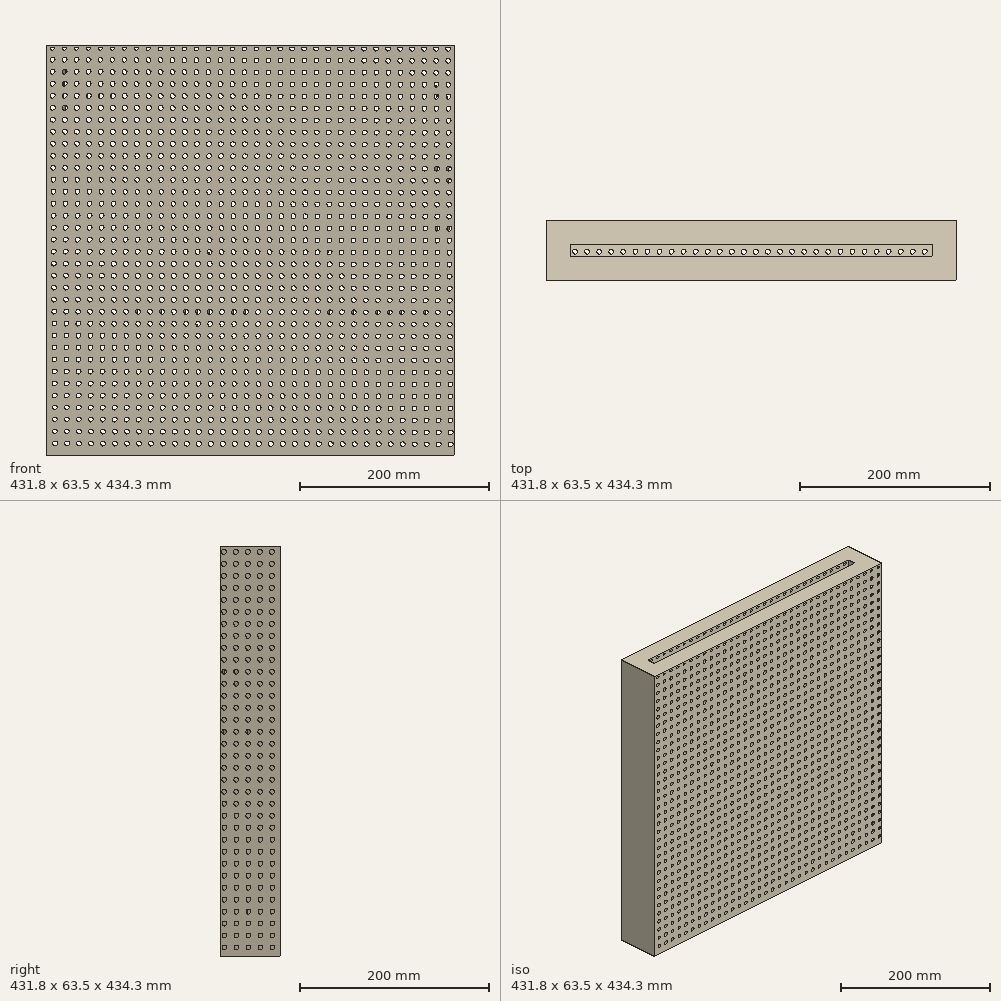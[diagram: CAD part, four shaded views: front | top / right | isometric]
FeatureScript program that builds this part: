
annotation { "Feature Type Name" : "Feature", "Feature Type Description" : "" }
export const myFeature = defineFeature(function(context is Context, id is Id, definition is map)
    precondition{}
    {
        {
            var Q0;
            Q0=qCreatedBy(makeId("Top.planeOp"),FACE);
            var sketch = newSketch(context, id + "F0", { "sketchPlane" : qUnion([Q0])});
            skLineSegment(sketch, "E0", {"start": v(-190.5, 6.35) * mm, "end": v(0, 6.35) * mm});
            skLineSegment(sketch, "E1", {"start": v(0, 6.35) * mm, "end": v(190.5, 6.35) * mm});
            skLineSegment(sketch, "E2", {"start": v(190.5, 6.35) * mm, "end": v(190.5, 0) * mm});
            skLineSegment(sketch, "E3", {"start": v(190.5, 0) * mm, "end": v(190.5, -6.35) * mm});
            skLineSegment(sketch, "E4", {"start": v(190.5, -6.35) * mm, "end": v(-190.5, -6.35) * mm});
            skLineSegment(sketch, "E5", {"start": v(-190.5, -6.35) * mm, "end": v(-190.5, 6.35) * mm});
            skLineSegment(sketch, "E6.0", {"start": v(-215.9, -31.75) * mm, "end": v(-215.9, 31.75) * mm});
            skLineSegment(sketch, "E6.1", {"start": v(0, 31.75) * mm, "end": v(215.9, 31.75) * mm});
            skLineSegment(sketch, "E6.2", {"start": v(215.9, 31.75) * mm, "end": v(215.9, -10.38) * mm});
            skLineSegment(sketch, "E6.3", {"start": v(-215.9, 31.75) * mm, "end": v(0, 31.75) * mm});
            skLineSegment(sketch, "E6.4", {"start": v(215.9, -10.38) * mm, "end": v(215.9, -31.75) * mm});
            skLineSegment(sketch, "E6.5", {"start": v(215.9, -31.75) * mm, "end": v(-215.9, -31.75) * mm});
            skSolve(sketch);
        }
        {
            var Q0;
            Q0 = qSketchRegion(id + "F0", true);
            extrude(context, id + "F1", {"entities" : qUnion([Q0]), "depth" : 431.8 * mm, "offsetDistance" : 25.4 * mm});
        }
        {
            var Q0;
            Q0=makeQuery(id+"F1.opExtrude","SWEPT_FACE",FACE,{"disambiguationData":[OSD([sQuery(id+"F0.wireOp",EDGE,"E6.1"),sQuery(id+"F0.wireOp",EDGE,"E6.3")])]});
            var sketch = newSketch(context, id + "F2", { "sketchPlane" : qUnion([Q0])});
            skCircle(sketch, "E7", {"center": v(209.68, 431.8) * mm, "radius": 2.54 * mm});
            skCircle(sketch, "E8.0.1.0", {"center": v(209.6, 419.1) * mm, "radius": 2.54 * mm});
            skCircle(sketch, "E8.0.2.0", {"center": v(209.51, 406.4) * mm, "radius": 2.54 * mm});
            skCircle(sketch, "E8.0.3.0", {"center": v(209.43, 393.7) * mm, "radius": 2.54 * mm});
            skCircle(sketch, "E8.0.4.0", {"center": v(209.34, 381) * mm, "radius": 2.54 * mm});
            skCircle(sketch, "E8.0.5.0", {"center": v(209.26, 368.3) * mm, "radius": 2.54 * mm});
            skCircle(sketch, "E8.0.6.0", {"center": v(209.17, 355.6) * mm, "radius": 2.54 * mm});
            skCircle(sketch, "E8.0.7.0", {"center": v(209.1, 342.9) * mm, "radius": 2.54 * mm});
            skCircle(sketch, "E8.0.8.0", {"center": v(209, 330.2) * mm, "radius": 2.54 * mm});
            skCircle(sketch, "E8.0.9.0", {"center": v(208.92, 317.5) * mm, "radius": 2.54 * mm});
            skCircle(sketch, "E8.0.10.0", {"center": v(208.84, 304.8) * mm, "radius": 2.54 * mm});
            skCircle(sketch, "E8.0.11.0", {"center": v(208.75, 292.1) * mm, "radius": 2.54 * mm});
            skCircle(sketch, "E8.0.12.0", {"center": v(208.67, 279.4) * mm, "radius": 2.54 * mm});
            skCircle(sketch, "E8.0.13.0", {"center": v(208.59, 266.7) * mm, "radius": 2.54 * mm});
            skCircle(sketch, "E8.0.14.0", {"center": v(208.5, 254) * mm, "radius": 2.54 * mm});
            skCircle(sketch, "E8.0.15.0", {"center": v(208.42, 241.3) * mm, "radius": 2.54 * mm});
            skCircle(sketch, "E8.0.16.0", {"center": v(208.33, 228.6) * mm, "radius": 2.54 * mm});
            skCircle(sketch, "E8.0.17.0", {"center": v(208.25, 215.9) * mm, "radius": 2.54 * mm});
            skCircle(sketch, "E8.0.18.0", {"center": v(208.17, 203.2) * mm, "radius": 2.54 * mm});
            skCircle(sketch, "E8.0.19.0", {"center": v(208.08, 190.5) * mm, "radius": 2.54 * mm});
            skCircle(sketch, "E8.0.20.0", {"center": v(208, 177.8) * mm, "radius": 2.54 * mm});
            skCircle(sketch, "E8.0.21.0", {"center": v(207.91, 165.1) * mm, "radius": 2.54 * mm});
            skCircle(sketch, "E8.0.22.0", {"center": v(207.83, 152.4) * mm, "radius": 2.54 * mm});
            skCircle(sketch, "E8.0.23.0", {"center": v(207.75, 139.7) * mm, "radius": 2.54 * mm});
            skCircle(sketch, "E8.0.24.0", {"center": v(207.66, 127) * mm, "radius": 2.54 * mm});
            skCircle(sketch, "E8.0.25.0", {"center": v(207.58, 114.3) * mm, "radius": 2.54 * mm});
            skCircle(sketch, "E8.0.26.0", {"center": v(207.5, 101.6) * mm, "radius": 2.54 * mm});
            skCircle(sketch, "E8.0.27.0", {"center": v(207.4, 88.9) * mm, "radius": 2.54 * mm});
            skCircle(sketch, "E8.0.28.0", {"center": v(207.33, 76.2) * mm, "radius": 2.54 * mm});
            skCircle(sketch, "E8.0.29.0", {"center": v(207.24, 63.5) * mm, "radius": 2.54 * mm});
            skCircle(sketch, "E8.0.30.0", {"center": v(207.16, 50.8) * mm, "radius": 2.54 * mm});
            skCircle(sketch, "E8.0.31.0", {"center": v(207.07, 38.1) * mm, "radius": 2.54 * mm});
            skCircle(sketch, "E8.0.32.0", {"center": v(206.99, 25.4) * mm, "radius": 2.54 * mm});
            skCircle(sketch, "E8.1.0.0", {"center": v(196.98, 431.77) * mm, "radius": 2.54 * mm});
            skCircle(sketch, "E8.1.1.0", {"center": v(196.9, 419.07) * mm, "radius": 2.54 * mm});
            skCircle(sketch, "E8.1.2.0", {"center": v(196.81, 406.37) * mm, "radius": 2.54 * mm});
            skCircle(sketch, "E8.1.3.0", {"center": v(196.73, 393.67) * mm, "radius": 2.54 * mm});
            skCircle(sketch, "E8.1.4.0", {"center": v(196.64, 380.97) * mm, "radius": 2.54 * mm});
            skCircle(sketch, "E8.1.5.0", {"center": v(196.56, 368.27) * mm, "radius": 2.54 * mm});
            skCircle(sketch, "E8.1.6.0", {"center": v(196.47, 355.57) * mm, "radius": 2.54 * mm});
            skCircle(sketch, "E8.1.7.0", {"center": v(196.4, 342.87) * mm, "radius": 2.54 * mm});
            skCircle(sketch, "E8.1.8.0", {"center": v(196.3, 330.17) * mm, "radius": 2.54 * mm});
            skCircle(sketch, "E8.1.9.0", {"center": v(196.22, 317.47) * mm, "radius": 2.54 * mm});
            skCircle(sketch, "E8.1.10.0", {"center": v(196.14, 304.77) * mm, "radius": 2.54 * mm});
            skCircle(sketch, "E8.1.11.0", {"center": v(196.05, 292.07) * mm, "radius": 2.54 * mm});
            skCircle(sketch, "E8.1.12.0", {"center": v(195.97, 279.37) * mm, "radius": 2.54 * mm});
            skCircle(sketch, "E8.1.13.0", {"center": v(195.89, 266.67) * mm, "radius": 2.54 * mm});
            skCircle(sketch, "E8.1.14.0", {"center": v(195.8, 253.97) * mm, "radius": 2.54 * mm});
            skCircle(sketch, "E8.1.15.0", {"center": v(195.72, 241.27) * mm, "radius": 2.54 * mm});
            skCircle(sketch, "E8.1.16.0", {"center": v(195.63, 228.57) * mm, "radius": 2.54 * mm});
            skCircle(sketch, "E8.1.17.0", {"center": v(195.55, 215.87) * mm, "radius": 2.54 * mm});
            skCircle(sketch, "E8.1.18.0", {"center": v(195.47, 203.17) * mm, "radius": 2.54 * mm});
            skCircle(sketch, "E8.1.19.0", {"center": v(195.38, 190.47) * mm, "radius": 2.54 * mm});
            skCircle(sketch, "E8.1.20.0", {"center": v(195.3, 177.77) * mm, "radius": 2.54 * mm});
            skCircle(sketch, "E8.1.21.0", {"center": v(195.21, 165.07) * mm, "radius": 2.54 * mm});
            skCircle(sketch, "E8.1.22.0", {"center": v(195.13, 152.37) * mm, "radius": 2.54 * mm});
            skCircle(sketch, "E8.1.23.0", {"center": v(195.05, 139.67) * mm, "radius": 2.54 * mm});
            skCircle(sketch, "E8.1.24.0", {"center": v(194.96, 126.98) * mm, "radius": 2.54 * mm});
            skCircle(sketch, "E8.1.25.0", {"center": v(194.88, 114.28) * mm, "radius": 2.54 * mm});
            skCircle(sketch, "E8.1.26.0", {"center": v(194.8, 101.58) * mm, "radius": 2.54 * mm});
            skCircle(sketch, "E8.1.27.0", {"center": v(194.7, 88.88) * mm, "radius": 2.54 * mm});
            skCircle(sketch, "E8.1.28.0", {"center": v(194.63, 76.18) * mm, "radius": 2.54 * mm});
            skCircle(sketch, "E8.1.29.0", {"center": v(194.54, 63.48) * mm, "radius": 2.54 * mm});
            skCircle(sketch, "E8.1.30.0", {"center": v(194.46, 50.78) * mm, "radius": 2.54 * mm});
            skCircle(sketch, "E8.1.31.0", {"center": v(194.37, 38.08) * mm, "radius": 2.54 * mm});
            skCircle(sketch, "E8.1.32.0", {"center": v(194.29, 25.38) * mm, "radius": 2.54 * mm});
            skCircle(sketch, "E8.2.0.0", {"center": v(184.28, 431.74) * mm, "radius": 2.54 * mm});
            skCircle(sketch, "E8.2.1.0", {"center": v(184.2, 419.04) * mm, "radius": 2.54 * mm});
            skCircle(sketch, "E8.2.2.0", {"center": v(184.11, 406.34) * mm, "radius": 2.54 * mm});
            skCircle(sketch, "E8.2.3.0", {"center": v(184.03, 393.64) * mm, "radius": 2.54 * mm});
            skCircle(sketch, "E8.2.4.0", {"center": v(183.94, 380.94) * mm, "radius": 2.54 * mm});
            skCircle(sketch, "E8.2.5.0", {"center": v(183.86, 368.24) * mm, "radius": 2.54 * mm});
            skCircle(sketch, "E8.2.6.0", {"center": v(183.77, 355.54) * mm, "radius": 2.54 * mm});
            skCircle(sketch, "E8.2.7.0", {"center": v(183.7, 342.84) * mm, "radius": 2.54 * mm});
            skCircle(sketch, "E8.2.8.0", {"center": v(183.6, 330.14) * mm, "radius": 2.54 * mm});
            skCircle(sketch, "E8.2.9.0", {"center": v(183.52, 317.44) * mm, "radius": 2.54 * mm});
            skCircle(sketch, "E8.2.10.0", {"center": v(183.44, 304.74) * mm, "radius": 2.54 * mm});
            skCircle(sketch, "E8.2.11.0", {"center": v(183.35, 292.04) * mm, "radius": 2.54 * mm});
            skCircle(sketch, "E8.2.12.0", {"center": v(183.27, 279.34) * mm, "radius": 2.54 * mm});
            skCircle(sketch, "E8.2.13.0", {"center": v(183.19, 266.64) * mm, "radius": 2.54 * mm});
            skCircle(sketch, "E8.2.14.0", {"center": v(183.1, 253.94) * mm, "radius": 2.54 * mm});
            skCircle(sketch, "E8.2.15.0", {"center": v(183.02, 241.24) * mm, "radius": 2.54 * mm});
            skCircle(sketch, "E8.2.16.0", {"center": v(182.93, 228.54) * mm, "radius": 2.54 * mm});
            skCircle(sketch, "E8.2.17.0", {"center": v(182.85, 215.84) * mm, "radius": 2.54 * mm});
            skCircle(sketch, "E8.2.18.0", {"center": v(182.77, 203.14) * mm, "radius": 2.54 * mm});
            skCircle(sketch, "E8.2.19.0", {"center": v(182.68, 190.44) * mm, "radius": 2.54 * mm});
            skCircle(sketch, "E8.2.20.0", {"center": v(182.6, 177.74) * mm, "radius": 2.54 * mm});
            skCircle(sketch, "E8.2.21.0", {"center": v(182.51, 165.04) * mm, "radius": 2.54 * mm});
            skCircle(sketch, "E8.2.22.0", {"center": v(182.43, 152.34) * mm, "radius": 2.54 * mm});
            skCircle(sketch, "E8.2.23.0", {"center": v(182.35, 139.64) * mm, "radius": 2.54 * mm});
            skCircle(sketch, "E8.2.24.0", {"center": v(182.26, 126.94) * mm, "radius": 2.54 * mm});
            skCircle(sketch, "E8.2.25.0", {"center": v(182.18, 114.24) * mm, "radius": 2.54 * mm});
            skCircle(sketch, "E8.2.26.0", {"center": v(182.1, 101.54) * mm, "radius": 2.54 * mm});
            skCircle(sketch, "E8.2.27.0", {"center": v(182, 88.84) * mm, "radius": 2.54 * mm});
            skCircle(sketch, "E8.2.28.0", {"center": v(181.93, 76.14) * mm, "radius": 2.54 * mm});
            skCircle(sketch, "E8.2.29.0", {"center": v(181.84, 63.45) * mm, "radius": 2.54 * mm});
            skCircle(sketch, "E8.2.30.0", {"center": v(181.76, 50.75) * mm, "radius": 2.54 * mm});
            skCircle(sketch, "E8.2.31.0", {"center": v(181.67, 38.05) * mm, "radius": 2.54 * mm});
            skCircle(sketch, "E8.2.32.0", {"center": v(181.59, 25.35) * mm, "radius": 2.54 * mm});
            skCircle(sketch, "E8.3.0.0", {"center": v(171.58, 431.7) * mm, "radius": 2.54 * mm});
            skCircle(sketch, "E8.3.1.0", {"center": v(171.5, 419) * mm, "radius": 2.54 * mm});
            skCircle(sketch, "E8.3.2.0", {"center": v(171.41, 406.3) * mm, "radius": 2.54 * mm});
            skCircle(sketch, "E8.3.3.0", {"center": v(171.33, 393.6) * mm, "radius": 2.54 * mm});
            skCircle(sketch, "E8.3.4.0", {"center": v(171.24, 380.9) * mm, "radius": 2.54 * mm});
            skCircle(sketch, "E8.3.5.0", {"center": v(171.16, 368.2) * mm, "radius": 2.54 * mm});
            skCircle(sketch, "E8.3.6.0", {"center": v(171.07, 355.5) * mm, "radius": 2.54 * mm});
            skCircle(sketch, "E8.3.7.0", {"center": v(171, 342.8) * mm, "radius": 2.54 * mm});
            skCircle(sketch, "E8.3.8.0", {"center": v(170.9, 330.1) * mm, "radius": 2.54 * mm});
            skCircle(sketch, "E8.3.9.0", {"center": v(170.82, 317.4) * mm, "radius": 2.54 * mm});
            skCircle(sketch, "E8.3.10.0", {"center": v(170.74, 304.7) * mm, "radius": 2.54 * mm});
            skCircle(sketch, "E8.3.11.0", {"center": v(170.65, 292) * mm, "radius": 2.54 * mm});
            skCircle(sketch, "E8.3.12.0", {"center": v(170.57, 279.3) * mm, "radius": 2.54 * mm});
            skCircle(sketch, "E8.3.13.0", {"center": v(170.49, 266.6) * mm, "radius": 2.54 * mm});
            skCircle(sketch, "E8.3.14.0", {"center": v(170.4, 253.9) * mm, "radius": 2.54 * mm});
            skCircle(sketch, "E8.3.15.0", {"center": v(170.32, 241.2) * mm, "radius": 2.54 * mm});
            skCircle(sketch, "E8.3.16.0", {"center": v(170.23, 228.51) * mm, "radius": 2.54 * mm});
            skCircle(sketch, "E8.3.17.0", {"center": v(170.15, 215.81) * mm, "radius": 2.54 * mm});
            skCircle(sketch, "E8.3.18.0", {"center": v(170.07, 203.11) * mm, "radius": 2.54 * mm});
            skCircle(sketch, "E8.3.19.0", {"center": v(169.98, 190.41) * mm, "radius": 2.54 * mm});
            skCircle(sketch, "E8.3.20.0", {"center": v(169.9, 177.71) * mm, "radius": 2.54 * mm});
            skCircle(sketch, "E8.3.21.0", {"center": v(169.81, 165.01) * mm, "radius": 2.54 * mm});
            skCircle(sketch, "E8.3.22.0", {"center": v(169.73, 152.31) * mm, "radius": 2.54 * mm});
            skCircle(sketch, "E8.3.23.0", {"center": v(169.65, 139.61) * mm, "radius": 2.54 * mm});
            skCircle(sketch, "E8.3.24.0", {"center": v(169.56, 126.91) * mm, "radius": 2.54 * mm});
            skCircle(sketch, "E8.3.25.0", {"center": v(169.48, 114.21) * mm, "radius": 2.54 * mm});
            skCircle(sketch, "E8.3.26.0", {"center": v(169.4, 101.51) * mm, "radius": 2.54 * mm});
            skCircle(sketch, "E8.3.27.0", {"center": v(169.3, 88.81) * mm, "radius": 2.54 * mm});
            skCircle(sketch, "E8.3.28.0", {"center": v(169.23, 76.11) * mm, "radius": 2.54 * mm});
            skCircle(sketch, "E8.3.29.0", {"center": v(169.14, 63.41) * mm, "radius": 2.54 * mm});
            skCircle(sketch, "E8.3.30.0", {"center": v(169.06, 50.71) * mm, "radius": 2.54 * mm});
            skCircle(sketch, "E8.3.31.0", {"center": v(168.97, 38.01) * mm, "radius": 2.54 * mm});
            skCircle(sketch, "E8.3.32.0", {"center": v(168.89, 25.31) * mm, "radius": 2.54 * mm});
            skCircle(sketch, "E8.4.0.0", {"center": v(158.88, 431.67) * mm, "radius": 2.54 * mm});
            skCircle(sketch, "E8.4.1.0", {"center": v(158.8, 418.97) * mm, "radius": 2.54 * mm});
            skCircle(sketch, "E8.4.2.0", {"center": v(158.71, 406.27) * mm, "radius": 2.54 * mm});
            skCircle(sketch, "E8.4.3.0", {"center": v(158.63, 393.58) * mm, "radius": 2.54 * mm});
            skCircle(sketch, "E8.4.4.0", {"center": v(158.54, 380.88) * mm, "radius": 2.54 * mm});
            skCircle(sketch, "E8.4.5.0", {"center": v(158.46, 368.18) * mm, "radius": 2.54 * mm});
            skCircle(sketch, "E8.4.6.0", {"center": v(158.37, 355.48) * mm, "radius": 2.54 * mm});
            skCircle(sketch, "E8.4.7.0", {"center": v(158.3, 342.78) * mm, "radius": 2.54 * mm});
            skCircle(sketch, "E8.4.8.0", {"center": v(158.2, 330.08) * mm, "radius": 2.54 * mm});
            skCircle(sketch, "E8.4.9.0", {"center": v(158.12, 317.38) * mm, "radius": 2.54 * mm});
            skCircle(sketch, "E8.4.10.0", {"center": v(158.04, 304.68) * mm, "radius": 2.54 * mm});
            skCircle(sketch, "E8.4.11.0", {"center": v(157.95, 291.98) * mm, "radius": 2.54 * mm});
            skCircle(sketch, "E8.4.12.0", {"center": v(157.87, 279.28) * mm, "radius": 2.54 * mm});
            skCircle(sketch, "E8.4.13.0", {"center": v(157.79, 266.58) * mm, "radius": 2.54 * mm});
            skCircle(sketch, "E8.4.14.0", {"center": v(157.7, 253.88) * mm, "radius": 2.54 * mm});
            skCircle(sketch, "E8.4.15.0", {"center": v(157.62, 241.18) * mm, "radius": 2.54 * mm});
            skCircle(sketch, "E8.4.16.0", {"center": v(157.53, 228.48) * mm, "radius": 2.54 * mm});
            skCircle(sketch, "E8.4.17.0", {"center": v(157.45, 215.78) * mm, "radius": 2.54 * mm});
            skCircle(sketch, "E8.4.18.0", {"center": v(157.37, 203.08) * mm, "radius": 2.54 * mm});
            skCircle(sketch, "E8.4.19.0", {"center": v(157.28, 190.38) * mm, "radius": 2.54 * mm});
            skCircle(sketch, "E8.4.20.0", {"center": v(157.2, 177.68) * mm, "radius": 2.54 * mm});
            skCircle(sketch, "E8.4.21.0", {"center": v(157.11, 164.98) * mm, "radius": 2.54 * mm});
            skCircle(sketch, "E8.4.22.0", {"center": v(157.03, 152.28) * mm, "radius": 2.54 * mm});
            skCircle(sketch, "E8.4.23.0", {"center": v(156.95, 139.58) * mm, "radius": 2.54 * mm});
            skCircle(sketch, "E8.4.24.0", {"center": v(156.86, 126.88) * mm, "radius": 2.54 * mm});
            skCircle(sketch, "E8.4.25.0", {"center": v(156.78, 114.18) * mm, "radius": 2.54 * mm});
            skCircle(sketch, "E8.4.26.0", {"center": v(156.7, 101.48) * mm, "radius": 2.54 * mm});
            skCircle(sketch, "E8.4.27.0", {"center": v(156.6, 88.78) * mm, "radius": 2.54 * mm});
            skCircle(sketch, "E8.4.28.0", {"center": v(156.53, 76.08) * mm, "radius": 2.54 * mm});
            skCircle(sketch, "E8.4.29.0", {"center": v(156.44, 63.38) * mm, "radius": 2.54 * mm});
            skCircle(sketch, "E8.4.30.0", {"center": v(156.36, 50.68) * mm, "radius": 2.54 * mm});
            skCircle(sketch, "E8.4.31.0", {"center": v(156.27, 37.98) * mm, "radius": 2.54 * mm});
            skCircle(sketch, "E8.4.32.0", {"center": v(156.19, 25.28) * mm, "radius": 2.54 * mm});
            skCircle(sketch, "E8.5.0.0", {"center": v(146.18, 431.64) * mm, "radius": 2.54 * mm});
            skCircle(sketch, "E8.5.1.0", {"center": v(146.1, 418.94) * mm, "radius": 2.54 * mm});
            skCircle(sketch, "E8.5.2.0", {"center": v(146.01, 406.24) * mm, "radius": 2.54 * mm});
            skCircle(sketch, "E8.5.3.0", {"center": v(145.93, 393.54) * mm, "radius": 2.54 * mm});
            skCircle(sketch, "E8.5.4.0", {"center": v(145.84, 380.84) * mm, "radius": 2.54 * mm});
            skCircle(sketch, "E8.5.5.0", {"center": v(145.76, 368.14) * mm, "radius": 2.54 * mm});
            skCircle(sketch, "E8.5.6.0", {"center": v(145.67, 355.44) * mm, "radius": 2.54 * mm});
            skCircle(sketch, "E8.5.7.0", {"center": v(145.6, 342.74) * mm, "radius": 2.54 * mm});
            skCircle(sketch, "E8.5.8.0", {"center": v(145.5, 330.05) * mm, "radius": 2.54 * mm});
            skCircle(sketch, "E8.5.9.0", {"center": v(145.42, 317.35) * mm, "radius": 2.54 * mm});
            skCircle(sketch, "E8.5.10.0", {"center": v(145.34, 304.65) * mm, "radius": 2.54 * mm});
            skCircle(sketch, "E8.5.11.0", {"center": v(145.25, 291.95) * mm, "radius": 2.54 * mm});
            skCircle(sketch, "E8.5.12.0", {"center": v(145.17, 279.25) * mm, "radius": 2.54 * mm});
            skCircle(sketch, "E8.5.13.0", {"center": v(145.09, 266.55) * mm, "radius": 2.54 * mm});
            skCircle(sketch, "E8.5.14.0", {"center": v(145, 253.85) * mm, "radius": 2.54 * mm});
            skCircle(sketch, "E8.5.15.0", {"center": v(144.92, 241.15) * mm, "radius": 2.54 * mm});
            skCircle(sketch, "E8.5.16.0", {"center": v(144.83, 228.45) * mm, "radius": 2.54 * mm});
            skCircle(sketch, "E8.5.17.0", {"center": v(144.75, 215.75) * mm, "radius": 2.54 * mm});
            skCircle(sketch, "E8.5.18.0", {"center": v(144.67, 203.05) * mm, "radius": 2.54 * mm});
            skCircle(sketch, "E8.5.19.0", {"center": v(144.58, 190.35) * mm, "radius": 2.54 * mm});
            skCircle(sketch, "E8.5.20.0", {"center": v(144.5, 177.65) * mm, "radius": 2.54 * mm});
            skCircle(sketch, "E8.5.21.0", {"center": v(144.41, 164.95) * mm, "radius": 2.54 * mm});
            skCircle(sketch, "E8.5.22.0", {"center": v(144.33, 152.25) * mm, "radius": 2.54 * mm});
            skCircle(sketch, "E8.5.23.0", {"center": v(144.25, 139.55) * mm, "radius": 2.54 * mm});
            skCircle(sketch, "E8.5.24.0", {"center": v(144.16, 126.85) * mm, "radius": 2.54 * mm});
            skCircle(sketch, "E8.5.25.0", {"center": v(144.08, 114.15) * mm, "radius": 2.54 * mm});
            skCircle(sketch, "E8.5.26.0", {"center": v(144, 101.45) * mm, "radius": 2.54 * mm});
            skCircle(sketch, "E8.5.27.0", {"center": v(143.9, 88.75) * mm, "radius": 2.54 * mm});
            skCircle(sketch, "E8.5.28.0", {"center": v(143.83, 76.05) * mm, "radius": 2.54 * mm});
            skCircle(sketch, "E8.5.29.0", {"center": v(143.74, 63.35) * mm, "radius": 2.54 * mm});
            skCircle(sketch, "E8.5.30.0", {"center": v(143.66, 50.65) * mm, "radius": 2.54 * mm});
            skCircle(sketch, "E8.5.31.0", {"center": v(143.57, 37.95) * mm, "radius": 2.54 * mm});
            skCircle(sketch, "E8.5.32.0", {"center": v(143.49, 25.25) * mm, "radius": 2.54 * mm});
            skCircle(sketch, "E8.6.0.0", {"center": v(133.48, 431.61) * mm, "radius": 2.54 * mm});
            skCircle(sketch, "E8.6.1.0", {"center": v(133.4, 418.91) * mm, "radius": 2.54 * mm});
            skCircle(sketch, "E8.6.2.0", {"center": v(133.31, 406.21) * mm, "radius": 2.54 * mm});
            skCircle(sketch, "E8.6.3.0", {"center": v(133.23, 393.51) * mm, "radius": 2.54 * mm});
            skCircle(sketch, "E8.6.4.0", {"center": v(133.14, 380.81) * mm, "radius": 2.54 * mm});
            skCircle(sketch, "E8.6.5.0", {"center": v(133.06, 368.11) * mm, "radius": 2.54 * mm});
            skCircle(sketch, "E8.6.6.0", {"center": v(132.97, 355.41) * mm, "radius": 2.54 * mm});
            skCircle(sketch, "E8.6.7.0", {"center": v(132.9, 342.71) * mm, "radius": 2.54 * mm});
            skCircle(sketch, "E8.6.8.0", {"center": v(132.8, 330.01) * mm, "radius": 2.54 * mm});
            skCircle(sketch, "E8.6.9.0", {"center": v(132.72, 317.31) * mm, "radius": 2.54 * mm});
            skCircle(sketch, "E8.6.10.0", {"center": v(132.64, 304.61) * mm, "radius": 2.54 * mm});
            skCircle(sketch, "E8.6.11.0", {"center": v(132.55, 291.91) * mm, "radius": 2.54 * mm});
            skCircle(sketch, "E8.6.12.0", {"center": v(132.47, 279.21) * mm, "radius": 2.54 * mm});
            skCircle(sketch, "E8.6.13.0", {"center": v(132.39, 266.52) * mm, "radius": 2.54 * mm});
            skCircle(sketch, "E8.6.14.0", {"center": v(132.3, 253.82) * mm, "radius": 2.54 * mm});
            skCircle(sketch, "E8.6.15.0", {"center": v(132.22, 241.12) * mm, "radius": 2.54 * mm});
            skCircle(sketch, "E8.6.16.0", {"center": v(132.13, 228.42) * mm, "radius": 2.54 * mm});
            skCircle(sketch, "E8.6.17.0", {"center": v(132.05, 215.72) * mm, "radius": 2.54 * mm});
            skCircle(sketch, "E8.6.18.0", {"center": v(131.97, 203.02) * mm, "radius": 2.54 * mm});
            skCircle(sketch, "E8.6.19.0", {"center": v(131.88, 190.32) * mm, "radius": 2.54 * mm});
            skCircle(sketch, "E8.6.20.0", {"center": v(131.8, 177.62) * mm, "radius": 2.54 * mm});
            skCircle(sketch, "E8.6.21.0", {"center": v(131.71, 164.92) * mm, "radius": 2.54 * mm});
            skCircle(sketch, "E8.6.22.0", {"center": v(131.63, 152.22) * mm, "radius": 2.54 * mm});
            skCircle(sketch, "E8.6.23.0", {"center": v(131.55, 139.52) * mm, "radius": 2.54 * mm});
            skCircle(sketch, "E8.6.24.0", {"center": v(131.46, 126.82) * mm, "radius": 2.54 * mm});
            skCircle(sketch, "E8.6.25.0", {"center": v(131.38, 114.12) * mm, "radius": 2.54 * mm});
            skCircle(sketch, "E8.6.26.0", {"center": v(131.3, 101.42) * mm, "radius": 2.54 * mm});
            skCircle(sketch, "E8.6.27.0", {"center": v(131.2, 88.72) * mm, "radius": 2.54 * mm});
            skCircle(sketch, "E8.6.28.0", {"center": v(131.13, 76.02) * mm, "radius": 2.54 * mm});
            skCircle(sketch, "E8.6.29.0", {"center": v(131.04, 63.32) * mm, "radius": 2.54 * mm});
            skCircle(sketch, "E8.6.30.0", {"center": v(130.96, 50.62) * mm, "radius": 2.54 * mm});
            skCircle(sketch, "E8.6.31.0", {"center": v(130.87, 37.92) * mm, "radius": 2.54 * mm});
            skCircle(sketch, "E8.6.32.0", {"center": v(130.79, 25.22) * mm, "radius": 2.54 * mm});
            skCircle(sketch, "E8.7.0.0", {"center": v(120.78, 431.58) * mm, "radius": 2.54 * mm});
            skCircle(sketch, "E8.7.1.0", {"center": v(120.7, 418.88) * mm, "radius": 2.54 * mm});
            skCircle(sketch, "E8.7.2.0", {"center": v(120.61, 406.18) * mm, "radius": 2.54 * mm});
            skCircle(sketch, "E8.7.3.0", {"center": v(120.53, 393.48) * mm, "radius": 2.54 * mm});
            skCircle(sketch, "E8.7.4.0", {"center": v(120.44, 380.78) * mm, "radius": 2.54 * mm});
            skCircle(sketch, "E8.7.5.0", {"center": v(120.36, 368.08) * mm, "radius": 2.54 * mm});
            skCircle(sketch, "E8.7.6.0", {"center": v(120.27, 355.38) * mm, "radius": 2.54 * mm});
            skCircle(sketch, "E8.7.7.0", {"center": v(120.2, 342.68) * mm, "radius": 2.54 * mm});
            skCircle(sketch, "E8.7.8.0", {"center": v(120.1, 329.98) * mm, "radius": 2.54 * mm});
            skCircle(sketch, "E8.7.9.0", {"center": v(120.02, 317.28) * mm, "radius": 2.54 * mm});
            skCircle(sketch, "E8.7.10.0", {"center": v(119.94, 304.58) * mm, "radius": 2.54 * mm});
            skCircle(sketch, "E8.7.11.0", {"center": v(119.85, 291.88) * mm, "radius": 2.54 * mm});
            skCircle(sketch, "E8.7.12.0", {"center": v(119.77, 279.18) * mm, "radius": 2.54 * mm});
            skCircle(sketch, "E8.7.13.0", {"center": v(119.69, 266.48) * mm, "radius": 2.54 * mm});
            skCircle(sketch, "E8.7.14.0", {"center": v(119.6, 253.78) * mm, "radius": 2.54 * mm});
            skCircle(sketch, "E8.7.15.0", {"center": v(119.52, 241.08) * mm, "radius": 2.54 * mm});
            skCircle(sketch, "E8.7.16.0", {"center": v(119.43, 228.38) * mm, "radius": 2.54 * mm});
            skCircle(sketch, "E8.7.17.0", {"center": v(119.35, 215.68) * mm, "radius": 2.54 * mm});
            skCircle(sketch, "E8.7.18.0", {"center": v(119.27, 202.99) * mm, "radius": 2.54 * mm});
            skCircle(sketch, "E8.7.19.0", {"center": v(119.18, 190.29) * mm, "radius": 2.54 * mm});
            skCircle(sketch, "E8.7.20.0", {"center": v(119.1, 177.59) * mm, "radius": 2.54 * mm});
            skCircle(sketch, "E8.7.21.0", {"center": v(119.01, 164.89) * mm, "radius": 2.54 * mm});
            skCircle(sketch, "E8.7.22.0", {"center": v(118.93, 152.19) * mm, "radius": 2.54 * mm});
            skCircle(sketch, "E8.7.23.0", {"center": v(118.85, 139.49) * mm, "radius": 2.54 * mm});
            skCircle(sketch, "E8.7.24.0", {"center": v(118.76, 126.79) * mm, "radius": 2.54 * mm});
            skCircle(sketch, "E8.7.25.0", {"center": v(118.68, 114.09) * mm, "radius": 2.54 * mm});
            skCircle(sketch, "E8.7.26.0", {"center": v(118.6, 101.39) * mm, "radius": 2.54 * mm});
            skCircle(sketch, "E8.7.27.0", {"center": v(118.5, 88.69) * mm, "radius": 2.54 * mm});
            skCircle(sketch, "E8.7.28.0", {"center": v(118.43, 75.99) * mm, "radius": 2.54 * mm});
            skCircle(sketch, "E8.7.29.0", {"center": v(118.34, 63.29) * mm, "radius": 2.54 * mm});
            skCircle(sketch, "E8.7.30.0", {"center": v(118.26, 50.59) * mm, "radius": 2.54 * mm});
            skCircle(sketch, "E8.7.31.0", {"center": v(118.17, 37.89) * mm, "radius": 2.54 * mm});
            skCircle(sketch, "E8.7.32.0", {"center": v(118.09, 25.19) * mm, "radius": 2.54 * mm});
            skCircle(sketch, "E8.8.0.0", {"center": v(108.08, 431.55) * mm, "radius": 2.54 * mm});
            skCircle(sketch, "E8.8.1.0", {"center": v(108, 418.85) * mm, "radius": 2.54 * mm});
            skCircle(sketch, "E8.8.2.0", {"center": v(107.91, 406.15) * mm, "radius": 2.54 * mm});
            skCircle(sketch, "E8.8.3.0", {"center": v(107.83, 393.45) * mm, "radius": 2.54 * mm});
            skCircle(sketch, "E8.8.4.0", {"center": v(107.74, 380.75) * mm, "radius": 2.54 * mm});
            skCircle(sketch, "E8.8.5.0", {"center": v(107.66, 368.05) * mm, "radius": 2.54 * mm});
            skCircle(sketch, "E8.8.6.0", {"center": v(107.57, 355.35) * mm, "radius": 2.54 * mm});
            skCircle(sketch, "E8.8.7.0", {"center": v(107.5, 342.65) * mm, "radius": 2.54 * mm});
            skCircle(sketch, "E8.8.8.0", {"center": v(107.4, 329.95) * mm, "radius": 2.54 * mm});
            skCircle(sketch, "E8.8.9.0", {"center": v(107.32, 317.25) * mm, "radius": 2.54 * mm});
            skCircle(sketch, "E8.8.10.0", {"center": v(107.24, 304.55) * mm, "radius": 2.54 * mm});
            skCircle(sketch, "E8.8.11.0", {"center": v(107.15, 291.85) * mm, "radius": 2.54 * mm});
            skCircle(sketch, "E8.8.12.0", {"center": v(107.07, 279.15) * mm, "radius": 2.54 * mm});
            skCircle(sketch, "E8.8.13.0", {"center": v(106.99, 266.45) * mm, "radius": 2.54 * mm});
            skCircle(sketch, "E8.8.14.0", {"center": v(106.9, 253.75) * mm, "radius": 2.54 * mm});
            skCircle(sketch, "E8.8.15.0", {"center": v(106.82, 241.05) * mm, "radius": 2.54 * mm});
            skCircle(sketch, "E8.8.16.0", {"center": v(106.73, 228.35) * mm, "radius": 2.54 * mm});
            skCircle(sketch, "E8.8.17.0", {"center": v(106.65, 215.65) * mm, "radius": 2.54 * mm});
            skCircle(sketch, "E8.8.18.0", {"center": v(106.57, 202.95) * mm, "radius": 2.54 * mm});
            skCircle(sketch, "E8.8.19.0", {"center": v(106.48, 190.25) * mm, "radius": 2.54 * mm});
            skCircle(sketch, "E8.8.20.0", {"center": v(106.4, 177.55) * mm, "radius": 2.54 * mm});
            skCircle(sketch, "E8.8.21.0", {"center": v(106.31, 164.85) * mm, "radius": 2.54 * mm});
            skCircle(sketch, "E8.8.22.0", {"center": v(106.23, 152.15) * mm, "radius": 2.54 * mm});
            skCircle(sketch, "E8.8.23.0", {"center": v(106.15, 139.46) * mm, "radius": 2.54 * mm});
            skCircle(sketch, "E8.8.24.0", {"center": v(106.06, 126.76) * mm, "radius": 2.54 * mm});
            skCircle(sketch, "E8.8.25.0", {"center": v(105.98, 114.06) * mm, "radius": 2.54 * mm});
            skCircle(sketch, "E8.8.26.0", {"center": v(105.9, 101.36) * mm, "radius": 2.54 * mm});
            skCircle(sketch, "E8.8.27.0", {"center": v(105.8, 88.66) * mm, "radius": 2.54 * mm});
            skCircle(sketch, "E8.8.28.0", {"center": v(105.73, 75.96) * mm, "radius": 2.54 * mm});
            skCircle(sketch, "E8.8.29.0", {"center": v(105.64, 63.26) * mm, "radius": 2.54 * mm});
            skCircle(sketch, "E8.8.30.0", {"center": v(105.56, 50.56) * mm, "radius": 2.54 * mm});
            skCircle(sketch, "E8.8.31.0", {"center": v(105.47, 37.86) * mm, "radius": 2.54 * mm});
            skCircle(sketch, "E8.8.32.0", {"center": v(105.39, 25.16) * mm, "radius": 2.54 * mm});
            skCircle(sketch, "E8.9.0.0", {"center": v(95.38, 431.52) * mm, "radius": 2.54 * mm});
            skCircle(sketch, "E8.9.1.0", {"center": v(95.3, 418.82) * mm, "radius": 2.54 * mm});
            skCircle(sketch, "E8.9.2.0", {"center": v(95.21, 406.12) * mm, "radius": 2.54 * mm});
            skCircle(sketch, "E8.9.3.0", {"center": v(95.13, 393.42) * mm, "radius": 2.54 * mm});
            skCircle(sketch, "E8.9.4.0", {"center": v(95.04, 380.72) * mm, "radius": 2.54 * mm});
            skCircle(sketch, "E8.9.5.0", {"center": v(94.96, 368.02) * mm, "radius": 2.54 * mm});
            skCircle(sketch, "E8.9.6.0", {"center": v(94.87, 355.32) * mm, "radius": 2.54 * mm});
            skCircle(sketch, "E8.9.7.0", {"center": v(94.8, 342.62) * mm, "radius": 2.54 * mm});
            skCircle(sketch, "E8.9.8.0", {"center": v(94.7, 329.92) * mm, "radius": 2.54 * mm});
            skCircle(sketch, "E8.9.9.0", {"center": v(94.62, 317.22) * mm, "radius": 2.54 * mm});
            skCircle(sketch, "E8.9.10.0", {"center": v(94.54, 304.52) * mm, "radius": 2.54 * mm});
            skCircle(sketch, "E8.9.11.0", {"center": v(94.45, 291.82) * mm, "radius": 2.54 * mm});
            skCircle(sketch, "E8.9.12.0", {"center": v(94.37, 279.12) * mm, "radius": 2.54 * mm});
            skCircle(sketch, "E8.9.13.0", {"center": v(94.29, 266.42) * mm, "radius": 2.54 * mm});
            skCircle(sketch, "E8.9.14.0", {"center": v(94.2, 253.72) * mm, "radius": 2.54 * mm});
            skCircle(sketch, "E8.9.15.0", {"center": v(94.12, 241.02) * mm, "radius": 2.54 * mm});
            skCircle(sketch, "E8.9.16.0", {"center": v(94.03, 228.32) * mm, "radius": 2.54 * mm});
            skCircle(sketch, "E8.9.17.0", {"center": v(93.95, 215.62) * mm, "radius": 2.54 * mm});
            skCircle(sketch, "E8.9.18.0", {"center": v(93.87, 202.92) * mm, "radius": 2.54 * mm});
            skCircle(sketch, "E8.9.19.0", {"center": v(93.78, 190.22) * mm, "radius": 2.54 * mm});
            skCircle(sketch, "E8.9.20.0", {"center": v(93.7, 177.52) * mm, "radius": 2.54 * mm});
            skCircle(sketch, "E8.9.21.0", {"center": v(93.61, 164.82) * mm, "radius": 2.54 * mm});
            skCircle(sketch, "E8.9.22.0", {"center": v(93.53, 152.12) * mm, "radius": 2.54 * mm});
            skCircle(sketch, "E8.9.23.0", {"center": v(93.45, 139.42) * mm, "radius": 2.54 * mm});
            skCircle(sketch, "E8.9.24.0", {"center": v(93.36, 126.72) * mm, "radius": 2.54 * mm});
            skCircle(sketch, "E8.9.25.0", {"center": v(93.28, 114.02) * mm, "radius": 2.54 * mm});
            skCircle(sketch, "E8.9.26.0", {"center": v(93.2, 101.32) * mm, "radius": 2.54 * mm});
            skCircle(sketch, "E8.9.27.0", {"center": v(93.1, 88.62) * mm, "radius": 2.54 * mm});
            skCircle(sketch, "E8.9.28.0", {"center": v(93.03, 75.93) * mm, "radius": 2.54 * mm});
            skCircle(sketch, "E8.9.29.0", {"center": v(92.94, 63.23) * mm, "radius": 2.54 * mm});
            skCircle(sketch, "E8.9.30.0", {"center": v(92.86, 50.53) * mm, "radius": 2.54 * mm});
            skCircle(sketch, "E8.9.31.0", {"center": v(92.77, 37.83) * mm, "radius": 2.54 * mm});
            skCircle(sketch, "E8.9.32.0", {"center": v(92.69, 25.13) * mm, "radius": 2.54 * mm});
            skCircle(sketch, "E8.10.0.0", {"center": v(82.68, 431.49) * mm, "radius": 2.54 * mm});
            skCircle(sketch, "E8.10.1.0", {"center": v(82.6, 418.79) * mm, "radius": 2.54 * mm});
            skCircle(sketch, "E8.10.2.0", {"center": v(82.51, 406.09) * mm, "radius": 2.54 * mm});
            skCircle(sketch, "E8.10.3.0", {"center": v(82.43, 393.39) * mm, "radius": 2.54 * mm});
            skCircle(sketch, "E8.10.4.0", {"center": v(82.34, 380.69) * mm, "radius": 2.54 * mm});
            skCircle(sketch, "E8.10.5.0", {"center": v(82.26, 367.99) * mm, "radius": 2.54 * mm});
            skCircle(sketch, "E8.10.6.0", {"center": v(82.17, 355.29) * mm, "radius": 2.54 * mm});
            skCircle(sketch, "E8.10.7.0", {"center": v(82.1, 342.59) * mm, "radius": 2.54 * mm});
            skCircle(sketch, "E8.10.8.0", {"center": v(82, 329.89) * mm, "radius": 2.54 * mm});
            skCircle(sketch, "E8.10.9.0", {"center": v(81.92, 317.19) * mm, "radius": 2.54 * mm});
            skCircle(sketch, "E8.10.10.0", {"center": v(81.84, 304.49) * mm, "radius": 2.54 * mm});
            skCircle(sketch, "E8.10.11.0", {"center": v(81.75, 291.79) * mm, "radius": 2.54 * mm});
            skCircle(sketch, "E8.10.12.0", {"center": v(81.67, 279.09) * mm, "radius": 2.54 * mm});
            skCircle(sketch, "E8.10.13.0", {"center": v(81.59, 266.39) * mm, "radius": 2.54 * mm});
            skCircle(sketch, "E8.10.14.0", {"center": v(81.5, 253.69) * mm, "radius": 2.54 * mm});
            skCircle(sketch, "E8.10.15.0", {"center": v(81.42, 241) * mm, "radius": 2.54 * mm});
            skCircle(sketch, "E8.10.16.0", {"center": v(81.33, 228.3) * mm, "radius": 2.54 * mm});
            skCircle(sketch, "E8.10.17.0", {"center": v(81.25, 215.6) * mm, "radius": 2.54 * mm});
            skCircle(sketch, "E8.10.18.0", {"center": v(81.17, 202.9) * mm, "radius": 2.54 * mm});
            skCircle(sketch, "E8.10.19.0", {"center": v(81.08, 190.2) * mm, "radius": 2.54 * mm});
            skCircle(sketch, "E8.10.20.0", {"center": v(81, 177.5) * mm, "radius": 2.54 * mm});
            skCircle(sketch, "E8.10.21.0", {"center": v(80.91, 164.8) * mm, "radius": 2.54 * mm});
            skCircle(sketch, "E8.10.22.0", {"center": v(80.83, 152.1) * mm, "radius": 2.54 * mm});
            skCircle(sketch, "E8.10.23.0", {"center": v(80.75, 139.4) * mm, "radius": 2.54 * mm});
            skCircle(sketch, "E8.10.24.0", {"center": v(80.66, 126.7) * mm, "radius": 2.54 * mm});
            skCircle(sketch, "E8.10.25.0", {"center": v(80.58, 114) * mm, "radius": 2.54 * mm});
            skCircle(sketch, "E8.10.26.0", {"center": v(80.5, 101.3) * mm, "radius": 2.54 * mm});
            skCircle(sketch, "E8.10.27.0", {"center": v(80.4, 88.6) * mm, "radius": 2.54 * mm});
            skCircle(sketch, "E8.10.28.0", {"center": v(80.33, 75.9) * mm, "radius": 2.54 * mm});
            skCircle(sketch, "E8.10.29.0", {"center": v(80.24, 63.2) * mm, "radius": 2.54 * mm});
            skCircle(sketch, "E8.10.30.0", {"center": v(80.16, 50.5) * mm, "radius": 2.54 * mm});
            skCircle(sketch, "E8.10.31.0", {"center": v(80.07, 37.8) * mm, "radius": 2.54 * mm});
            skCircle(sketch, "E8.10.32.0", {"center": v(79.99, 25.1) * mm, "radius": 2.54 * mm});
            skCircle(sketch, "E8.11.0.0", {"center": v(69.98, 431.45) * mm, "radius": 2.54 * mm});
            skCircle(sketch, "E8.11.1.0", {"center": v(69.9, 418.75) * mm, "radius": 2.54 * mm});
            skCircle(sketch, "E8.11.2.0", {"center": v(69.81, 406.06) * mm, "radius": 2.54 * mm});
            skCircle(sketch, "E8.11.3.0", {"center": v(69.73, 393.36) * mm, "radius": 2.54 * mm});
            skCircle(sketch, "E8.11.4.0", {"center": v(69.64, 380.66) * mm, "radius": 2.54 * mm});
            skCircle(sketch, "E8.11.5.0", {"center": v(69.56, 367.96) * mm, "radius": 2.54 * mm});
            skCircle(sketch, "E8.11.6.0", {"center": v(69.47, 355.26) * mm, "radius": 2.54 * mm});
            skCircle(sketch, "E8.11.7.0", {"center": v(69.4, 342.56) * mm, "radius": 2.54 * mm});
            skCircle(sketch, "E8.11.8.0", {"center": v(69.3, 329.86) * mm, "radius": 2.54 * mm});
            skCircle(sketch, "E8.11.9.0", {"center": v(69.22, 317.16) * mm, "radius": 2.54 * mm});
            skCircle(sketch, "E8.11.10.0", {"center": v(69.14, 304.46) * mm, "radius": 2.54 * mm});
            skCircle(sketch, "E8.11.11.0", {"center": v(69.05, 291.76) * mm, "radius": 2.54 * mm});
            skCircle(sketch, "E8.11.12.0", {"center": v(68.97, 279.06) * mm, "radius": 2.54 * mm});
            skCircle(sketch, "E8.11.13.0", {"center": v(68.89, 266.36) * mm, "radius": 2.54 * mm});
            skCircle(sketch, "E8.11.14.0", {"center": v(68.8, 253.66) * mm, "radius": 2.54 * mm});
            skCircle(sketch, "E8.11.15.0", {"center": v(68.72, 240.96) * mm, "radius": 2.54 * mm});
            skCircle(sketch, "E8.11.16.0", {"center": v(68.63, 228.26) * mm, "radius": 2.54 * mm});
            skCircle(sketch, "E8.11.17.0", {"center": v(68.55, 215.56) * mm, "radius": 2.54 * mm});
            skCircle(sketch, "E8.11.18.0", {"center": v(68.47, 202.86) * mm, "radius": 2.54 * mm});
            skCircle(sketch, "E8.11.19.0", {"center": v(68.38, 190.16) * mm, "radius": 2.54 * mm});
            skCircle(sketch, "E8.11.20.0", {"center": v(68.3, 177.46) * mm, "radius": 2.54 * mm});
            skCircle(sketch, "E8.11.21.0", {"center": v(68.21, 164.76) * mm, "radius": 2.54 * mm});
            skCircle(sketch, "E8.11.22.0", {"center": v(68.13, 152.06) * mm, "radius": 2.54 * mm});
            skCircle(sketch, "E8.11.23.0", {"center": v(68.05, 139.36) * mm, "radius": 2.54 * mm});
            skCircle(sketch, "E8.11.24.0", {"center": v(67.96, 126.66) * mm, "radius": 2.54 * mm});
            skCircle(sketch, "E8.11.25.0", {"center": v(67.88, 113.96) * mm, "radius": 2.54 * mm});
            skCircle(sketch, "E8.11.26.0", {"center": v(67.8, 101.26) * mm, "radius": 2.54 * mm});
            skCircle(sketch, "E8.11.27.0", {"center": v(67.7, 88.56) * mm, "radius": 2.54 * mm});
            skCircle(sketch, "E8.11.28.0", {"center": v(67.63, 75.86) * mm, "radius": 2.54 * mm});
            skCircle(sketch, "E8.11.29.0", {"center": v(67.54, 63.16) * mm, "radius": 2.54 * mm});
            skCircle(sketch, "E8.11.30.0", {"center": v(67.46, 50.46) * mm, "radius": 2.54 * mm});
            skCircle(sketch, "E8.11.31.0", {"center": v(67.37, 37.76) * mm, "radius": 2.54 * mm});
            skCircle(sketch, "E8.11.32.0", {"center": v(67.29, 25.06) * mm, "radius": 2.54 * mm});
            skCircle(sketch, "E8.12.0.0", {"center": v(57.28, 431.42) * mm, "radius": 2.54 * mm});
            skCircle(sketch, "E8.12.1.0", {"center": v(57.2, 418.72) * mm, "radius": 2.54 * mm});
            skCircle(sketch, "E8.12.2.0", {"center": v(57.11, 406.02) * mm, "radius": 2.54 * mm});
            skCircle(sketch, "E8.12.3.0", {"center": v(57.03, 393.32) * mm, "radius": 2.54 * mm});
            skCircle(sketch, "E8.12.4.0", {"center": v(56.94, 380.62) * mm, "radius": 2.54 * mm});
            skCircle(sketch, "E8.12.5.0", {"center": v(56.86, 367.92) * mm, "radius": 2.54 * mm});
            skCircle(sketch, "E8.12.6.0", {"center": v(56.77, 355.22) * mm, "radius": 2.54 * mm});
            skCircle(sketch, "E8.12.7.0", {"center": v(56.7, 342.53) * mm, "radius": 2.54 * mm});
            skCircle(sketch, "E8.12.8.0", {"center": v(56.6, 329.83) * mm, "radius": 2.54 * mm});
            skCircle(sketch, "E8.12.9.0", {"center": v(56.52, 317.13) * mm, "radius": 2.54 * mm});
            skCircle(sketch, "E8.12.10.0", {"center": v(56.44, 304.43) * mm, "radius": 2.54 * mm});
            skCircle(sketch, "E8.12.11.0", {"center": v(56.35, 291.73) * mm, "radius": 2.54 * mm});
            skCircle(sketch, "E8.12.12.0", {"center": v(56.27, 279.03) * mm, "radius": 2.54 * mm});
            skCircle(sketch, "E8.12.13.0", {"center": v(56.19, 266.33) * mm, "radius": 2.54 * mm});
            skCircle(sketch, "E8.12.14.0", {"center": v(56.1, 253.63) * mm, "radius": 2.54 * mm});
            skCircle(sketch, "E8.12.15.0", {"center": v(56.02, 240.93) * mm, "radius": 2.54 * mm});
            skCircle(sketch, "E8.12.16.0", {"center": v(55.93, 228.23) * mm, "radius": 2.54 * mm});
            skCircle(sketch, "E8.12.17.0", {"center": v(55.85, 215.53) * mm, "radius": 2.54 * mm});
            skCircle(sketch, "E8.12.18.0", {"center": v(55.77, 202.83) * mm, "radius": 2.54 * mm});
            skCircle(sketch, "E8.12.19.0", {"center": v(55.68, 190.13) * mm, "radius": 2.54 * mm});
            skCircle(sketch, "E8.12.20.0", {"center": v(55.6, 177.43) * mm, "radius": 2.54 * mm});
            skCircle(sketch, "E8.12.21.0", {"center": v(55.51, 164.73) * mm, "radius": 2.54 * mm});
            skCircle(sketch, "E8.12.22.0", {"center": v(55.43, 152.03) * mm, "radius": 2.54 * mm});
            skCircle(sketch, "E8.12.23.0", {"center": v(55.35, 139.33) * mm, "radius": 2.54 * mm});
            skCircle(sketch, "E8.12.24.0", {"center": v(55.26, 126.63) * mm, "radius": 2.54 * mm});
            skCircle(sketch, "E8.12.25.0", {"center": v(55.18, 113.93) * mm, "radius": 2.54 * mm});
            skCircle(sketch, "E8.12.26.0", {"center": v(55.1, 101.23) * mm, "radius": 2.54 * mm});
            skCircle(sketch, "E8.12.27.0", {"center": v(55.01, 88.53) * mm, "radius": 2.54 * mm});
            skCircle(sketch, "E8.12.28.0", {"center": v(54.93, 75.83) * mm, "radius": 2.54 * mm});
            skCircle(sketch, "E8.12.29.0", {"center": v(54.84, 63.13) * mm, "radius": 2.54 * mm});
            skCircle(sketch, "E8.12.30.0", {"center": v(54.76, 50.43) * mm, "radius": 2.54 * mm});
            skCircle(sketch, "E8.12.31.0", {"center": v(54.67, 37.73) * mm, "radius": 2.54 * mm});
            skCircle(sketch, "E8.12.32.0", {"center": v(54.59, 25.03) * mm, "radius": 2.54 * mm});
            skCircle(sketch, "E8.13.0.0", {"center": v(44.58, 431.4) * mm, "radius": 2.54 * mm});
            skCircle(sketch, "E8.13.1.0", {"center": v(44.5, 418.7) * mm, "radius": 2.54 * mm});
            skCircle(sketch, "E8.13.2.0", {"center": v(44.41, 406) * mm, "radius": 2.54 * mm});
            skCircle(sketch, "E8.13.3.0", {"center": v(44.33, 393.3) * mm, "radius": 2.54 * mm});
            skCircle(sketch, "E8.13.4.0", {"center": v(44.24, 380.6) * mm, "radius": 2.54 * mm});
            skCircle(sketch, "E8.13.5.0", {"center": v(44.16, 367.9) * mm, "radius": 2.54 * mm});
            skCircle(sketch, "E8.13.6.0", {"center": v(44.07, 355.2) * mm, "radius": 2.54 * mm});
            skCircle(sketch, "E8.13.7.0", {"center": v(44, 342.5) * mm, "radius": 2.54 * mm});
            skCircle(sketch, "E8.13.8.0", {"center": v(43.9, 329.8) * mm, "radius": 2.54 * mm});
            skCircle(sketch, "E8.13.9.0", {"center": v(43.82, 317.1) * mm, "radius": 2.54 * mm});
            skCircle(sketch, "E8.13.10.0", {"center": v(43.74, 304.4) * mm, "radius": 2.54 * mm});
            skCircle(sketch, "E8.13.11.0", {"center": v(43.65, 291.7) * mm, "radius": 2.54 * mm});
            skCircle(sketch, "E8.13.12.0", {"center": v(43.57, 279) * mm, "radius": 2.54 * mm});
            skCircle(sketch, "E8.13.13.0", {"center": v(43.49, 266.3) * mm, "radius": 2.54 * mm});
            skCircle(sketch, "E8.13.14.0", {"center": v(43.4, 253.6) * mm, "radius": 2.54 * mm});
            skCircle(sketch, "E8.13.15.0", {"center": v(43.32, 240.9) * mm, "radius": 2.54 * mm});
            skCircle(sketch, "E8.13.16.0", {"center": v(43.23, 228.2) * mm, "radius": 2.54 * mm});
            skCircle(sketch, "E8.13.17.0", {"center": v(43.15, 215.5) * mm, "radius": 2.54 * mm});
            skCircle(sketch, "E8.13.18.0", {"center": v(43.07, 202.8) * mm, "radius": 2.54 * mm});
            skCircle(sketch, "E8.13.19.0", {"center": v(42.98, 190.1) * mm, "radius": 2.54 * mm});
            skCircle(sketch, "E8.13.20.0", {"center": v(42.9, 177.4) * mm, "radius": 2.54 * mm});
            skCircle(sketch, "E8.13.21.0", {"center": v(42.81, 164.7) * mm, "radius": 2.54 * mm});
            skCircle(sketch, "E8.13.22.0", {"center": v(42.73, 152) * mm, "radius": 2.54 * mm});
            skCircle(sketch, "E8.13.23.0", {"center": v(42.65, 139.3) * mm, "radius": 2.54 * mm});
            skCircle(sketch, "E8.13.24.0", {"center": v(42.56, 126.6) * mm, "radius": 2.54 * mm});
            skCircle(sketch, "E8.13.25.0", {"center": v(42.48, 113.9) * mm, "radius": 2.54 * mm});
            skCircle(sketch, "E8.13.26.0", {"center": v(42.4, 101.2) * mm, "radius": 2.54 * mm});
            skCircle(sketch, "E8.13.27.0", {"center": v(42.31, 88.5) * mm, "radius": 2.54 * mm});
            skCircle(sketch, "E8.13.28.0", {"center": v(42.23, 75.8) * mm, "radius": 2.54 * mm});
            skCircle(sketch, "E8.13.29.0", {"center": v(42.14, 63.1) * mm, "radius": 2.54 * mm});
            skCircle(sketch, "E8.13.30.0", {"center": v(42.06, 50.4) * mm, "radius": 2.54 * mm});
            skCircle(sketch, "E8.13.31.0", {"center": v(41.97, 37.7) * mm, "radius": 2.54 * mm});
            skCircle(sketch, "E8.13.32.0", {"center": v(41.89, 25) * mm, "radius": 2.54 * mm});
            skCircle(sketch, "E8.14.0.0", {"center": v(31.88, 431.36) * mm, "radius": 2.54 * mm});
            skCircle(sketch, "E8.14.1.0", {"center": v(31.8, 418.66) * mm, "radius": 2.54 * mm});
            skCircle(sketch, "E8.14.2.0", {"center": v(31.71, 405.96) * mm, "radius": 2.54 * mm});
            skCircle(sketch, "E8.14.3.0", {"center": v(31.63, 393.26) * mm, "radius": 2.54 * mm});
            skCircle(sketch, "E8.14.4.0", {"center": v(31.54, 380.56) * mm, "radius": 2.54 * mm});
            skCircle(sketch, "E8.14.5.0", {"center": v(31.46, 367.86) * mm, "radius": 2.54 * mm});
            skCircle(sketch, "E8.14.6.0", {"center": v(31.37, 355.16) * mm, "radius": 2.54 * mm});
            skCircle(sketch, "E8.14.7.0", {"center": v(31.3, 342.46) * mm, "radius": 2.54 * mm});
            skCircle(sketch, "E8.14.8.0", {"center": v(31.2, 329.76) * mm, "radius": 2.54 * mm});
            skCircle(sketch, "E8.14.9.0", {"center": v(31.12, 317.06) * mm, "radius": 2.54 * mm});
            skCircle(sketch, "E8.14.10.0", {"center": v(31.04, 304.36) * mm, "radius": 2.54 * mm});
            skCircle(sketch, "E8.14.11.0", {"center": v(30.95, 291.66) * mm, "radius": 2.54 * mm});
            skCircle(sketch, "E8.14.12.0", {"center": v(30.87, 278.96) * mm, "radius": 2.54 * mm});
            skCircle(sketch, "E8.14.13.0", {"center": v(30.79, 266.26) * mm, "radius": 2.54 * mm});
            skCircle(sketch, "E8.14.14.0", {"center": v(30.7, 253.56) * mm, "radius": 2.54 * mm});
            skCircle(sketch, "E8.14.15.0", {"center": v(30.62, 240.86) * mm, "radius": 2.54 * mm});
            skCircle(sketch, "E8.14.16.0", {"center": v(30.53, 228.16) * mm, "radius": 2.54 * mm});
            skCircle(sketch, "E8.14.17.0", {"center": v(30.45, 215.47) * mm, "radius": 2.54 * mm});
            skCircle(sketch, "E8.14.18.0", {"center": v(30.37, 202.77) * mm, "radius": 2.54 * mm});
            skCircle(sketch, "E8.14.19.0", {"center": v(30.28, 190.07) * mm, "radius": 2.54 * mm});
            skCircle(sketch, "E8.14.20.0", {"center": v(30.2, 177.37) * mm, "radius": 2.54 * mm});
            skCircle(sketch, "E8.14.21.0", {"center": v(30.11, 164.67) * mm, "radius": 2.54 * mm});
            skCircle(sketch, "E8.14.22.0", {"center": v(30.03, 151.97) * mm, "radius": 2.54 * mm});
            skCircle(sketch, "E8.14.23.0", {"center": v(29.95, 139.27) * mm, "radius": 2.54 * mm});
            skCircle(sketch, "E8.14.24.0", {"center": v(29.86, 126.57) * mm, "radius": 2.54 * mm});
            skCircle(sketch, "E8.14.25.0", {"center": v(29.78, 113.87) * mm, "radius": 2.54 * mm});
            skCircle(sketch, "E8.14.26.0", {"center": v(29.7, 101.17) * mm, "radius": 2.54 * mm});
            skCircle(sketch, "E8.14.27.0", {"center": v(29.61, 88.47) * mm, "radius": 2.54 * mm});
            skCircle(sketch, "E8.14.28.0", {"center": v(29.53, 75.77) * mm, "radius": 2.54 * mm});
            skCircle(sketch, "E8.14.29.0", {"center": v(29.44, 63.07) * mm, "radius": 2.54 * mm});
            skCircle(sketch, "E8.14.30.0", {"center": v(29.36, 50.37) * mm, "radius": 2.54 * mm});
            skCircle(sketch, "E8.14.31.0", {"center": v(29.27, 37.67) * mm, "radius": 2.54 * mm});
            skCircle(sketch, "E8.14.32.0", {"center": v(29.19, 24.97) * mm, "radius": 2.54 * mm});
            skCircle(sketch, "E8.15.0.0", {"center": v(19.18, 431.33) * mm, "radius": 2.54 * mm});
            skCircle(sketch, "E8.15.1.0", {"center": v(19.1, 418.63) * mm, "radius": 2.54 * mm});
            skCircle(sketch, "E8.15.2.0", {"center": v(19.01, 405.93) * mm, "radius": 2.54 * mm});
            skCircle(sketch, "E8.15.3.0", {"center": v(18.93, 393.23) * mm, "radius": 2.54 * mm});
            skCircle(sketch, "E8.15.4.0", {"center": v(18.84, 380.53) * mm, "radius": 2.54 * mm});
            skCircle(sketch, "E8.15.5.0", {"center": v(18.76, 367.83) * mm, "radius": 2.54 * mm});
            skCircle(sketch, "E8.15.6.0", {"center": v(18.67, 355.13) * mm, "radius": 2.54 * mm});
            skCircle(sketch, "E8.15.7.0", {"center": v(18.6, 342.43) * mm, "radius": 2.54 * mm});
            skCircle(sketch, "E8.15.8.0", {"center": v(18.5, 329.73) * mm, "radius": 2.54 * mm});
            skCircle(sketch, "E8.15.9.0", {"center": v(18.42, 317.03) * mm, "radius": 2.54 * mm});
            skCircle(sketch, "E8.15.10.0", {"center": v(18.34, 304.33) * mm, "radius": 2.54 * mm});
            skCircle(sketch, "E8.15.11.0", {"center": v(18.25, 291.63) * mm, "radius": 2.54 * mm});
            skCircle(sketch, "E8.15.12.0", {"center": v(18.17, 278.93) * mm, "radius": 2.54 * mm});
            skCircle(sketch, "E8.15.13.0", {"center": v(18.09, 266.23) * mm, "radius": 2.54 * mm});
            skCircle(sketch, "E8.15.14.0", {"center": v(18, 253.53) * mm, "radius": 2.54 * mm});
            skCircle(sketch, "E8.15.15.0", {"center": v(17.92, 240.83) * mm, "radius": 2.54 * mm});
            skCircle(sketch, "E8.15.16.0", {"center": v(17.83, 228.13) * mm, "radius": 2.54 * mm});
            skCircle(sketch, "E8.15.17.0", {"center": v(17.75, 215.43) * mm, "radius": 2.54 * mm});
            skCircle(sketch, "E8.15.18.0", {"center": v(17.67, 202.73) * mm, "radius": 2.54 * mm});
            skCircle(sketch, "E8.15.19.0", {"center": v(17.58, 190.03) * mm, "radius": 2.54 * mm});
            skCircle(sketch, "E8.15.20.0", {"center": v(17.5, 177.33) * mm, "radius": 2.54 * mm});
            skCircle(sketch, "E8.15.21.0", {"center": v(17.41, 164.63) * mm, "radius": 2.54 * mm});
            skCircle(sketch, "E8.15.22.0", {"center": v(17.33, 151.94) * mm, "radius": 2.54 * mm});
            skCircle(sketch, "E8.15.23.0", {"center": v(17.25, 139.24) * mm, "radius": 2.54 * mm});
            skCircle(sketch, "E8.15.24.0", {"center": v(17.16, 126.54) * mm, "radius": 2.54 * mm});
            skCircle(sketch, "E8.15.25.0", {"center": v(17.08, 113.84) * mm, "radius": 2.54 * mm});
            skCircle(sketch, "E8.15.26.0", {"center": v(17, 101.14) * mm, "radius": 2.54 * mm});
            skCircle(sketch, "E8.15.27.0", {"center": v(16.91, 88.44) * mm, "radius": 2.54 * mm});
            skCircle(sketch, "E8.15.28.0", {"center": v(16.83, 75.74) * mm, "radius": 2.54 * mm});
            skCircle(sketch, "E8.15.29.0", {"center": v(16.74, 63.04) * mm, "radius": 2.54 * mm});
            skCircle(sketch, "E8.15.30.0", {"center": v(16.66, 50.34) * mm, "radius": 2.54 * mm});
            skCircle(sketch, "E8.15.31.0", {"center": v(16.57, 37.64) * mm, "radius": 2.54 * mm});
            skCircle(sketch, "E8.15.32.0", {"center": v(16.49, 24.94) * mm, "radius": 2.54 * mm});
            skCircle(sketch, "E8.16.0.0", {"center": v(6.48, 431.3) * mm, "radius": 2.54 * mm});
            skCircle(sketch, "E8.16.1.0", {"center": v(6.4, 418.6) * mm, "radius": 2.54 * mm});
            skCircle(sketch, "E8.16.2.0", {"center": v(6.31, 405.9) * mm, "radius": 2.54 * mm});
            skCircle(sketch, "E8.16.3.0", {"center": v(6.23, 393.2) * mm, "radius": 2.54 * mm});
            skCircle(sketch, "E8.16.4.0", {"center": v(6.14, 380.5) * mm, "radius": 2.54 * mm});
            skCircle(sketch, "E8.16.5.0", {"center": v(6.06, 367.8) * mm, "radius": 2.54 * mm});
            skCircle(sketch, "E8.16.6.0", {"center": v(5.97, 355.1) * mm, "radius": 2.54 * mm});
            skCircle(sketch, "E8.16.7.0", {"center": v(5.9, 342.4) * mm, "radius": 2.54 * mm});
            skCircle(sketch, "E8.16.8.0", {"center": v(5.8, 329.7) * mm, "radius": 2.54 * mm});
            skCircle(sketch, "E8.16.9.0", {"center": v(5.72, 317) * mm, "radius": 2.54 * mm});
            skCircle(sketch, "E8.16.10.0", {"center": v(5.64, 304.3) * mm, "radius": 2.54 * mm});
            skCircle(sketch, "E8.16.11.0", {"center": v(5.55, 291.6) * mm, "radius": 2.54 * mm});
            skCircle(sketch, "E8.16.12.0", {"center": v(5.47, 278.9) * mm, "radius": 2.54 * mm});
            skCircle(sketch, "E8.16.13.0", {"center": v(5.39, 266.2) * mm, "radius": 2.54 * mm});
            skCircle(sketch, "E8.16.14.0", {"center": v(5.3, 253.5) * mm, "radius": 2.54 * mm});
            skCircle(sketch, "E8.16.15.0", {"center": v(5.22, 240.8) * mm, "radius": 2.54 * mm});
            skCircle(sketch, "E8.16.16.0", {"center": v(5.13, 228.1) * mm, "radius": 2.54 * mm});
            skCircle(sketch, "E8.16.17.0", {"center": v(5.05, 215.4) * mm, "radius": 2.54 * mm});
            skCircle(sketch, "E8.16.18.0", {"center": v(4.97, 202.7) * mm, "radius": 2.54 * mm});
            skCircle(sketch, "E8.16.19.0", {"center": v(4.88, 190) * mm, "radius": 2.54 * mm});
            skCircle(sketch, "E8.16.20.0", {"center": v(4.8, 177.3) * mm, "radius": 2.54 * mm});
            skCircle(sketch, "E8.16.21.0", {"center": v(4.71, 164.6) * mm, "radius": 2.54 * mm});
            skCircle(sketch, "E8.16.22.0", {"center": v(4.63, 151.9) * mm, "radius": 2.54 * mm});
            skCircle(sketch, "E8.16.23.0", {"center": v(4.55, 139.2) * mm, "radius": 2.54 * mm});
            skCircle(sketch, "E8.16.24.0", {"center": v(4.46, 126.5) * mm, "radius": 2.54 * mm});
            skCircle(sketch, "E8.16.25.0", {"center": v(4.38, 113.8) * mm, "radius": 2.54 * mm});
            skCircle(sketch, "E8.16.26.0", {"center": v(4.3, 101.1) * mm, "radius": 2.54 * mm});
            skCircle(sketch, "E8.16.27.0", {"center": v(4.21, 88.4) * mm, "radius": 2.54 * mm});
            skCircle(sketch, "E8.16.28.0", {"center": v(4.13, 75.7) * mm, "radius": 2.54 * mm});
            skCircle(sketch, "E8.16.29.0", {"center": v(4.04, 63) * mm, "radius": 2.54 * mm});
            skCircle(sketch, "E8.16.30.0", {"center": v(3.96, 50.3) * mm, "radius": 2.54 * mm});
            skCircle(sketch, "E8.16.31.0", {"center": v(3.87, 37.6) * mm, "radius": 2.54 * mm});
            skCircle(sketch, "E8.16.32.0", {"center": v(3.79, 24.9) * mm, "radius": 2.54 * mm});
            skCircle(sketch, "E8.17.0.0", {"center": v(-6.22, 431.27) * mm, "radius": 2.54 * mm});
            skCircle(sketch, "E8.17.1.0", {"center": v(-6.3, 418.57) * mm, "radius": 2.54 * mm});
            skCircle(sketch, "E8.17.2.0", {"center": v(-6.39, 405.87) * mm, "radius": 2.54 * mm});
            skCircle(sketch, "E8.17.3.0", {"center": v(-6.47, 393.17) * mm, "radius": 2.54 * mm});
            skCircle(sketch, "E8.17.4.0", {"center": v(-6.56, 380.47) * mm, "radius": 2.54 * mm});
            skCircle(sketch, "E8.17.5.0", {"center": v(-6.64, 367.77) * mm, "radius": 2.54 * mm});
            skCircle(sketch, "E8.17.6.0", {"center": v(-6.73, 355.07) * mm, "radius": 2.54 * mm});
            skCircle(sketch, "E8.17.7.0", {"center": v(-6.8, 342.37) * mm, "radius": 2.54 * mm});
            skCircle(sketch, "E8.17.8.0", {"center": v(-6.9, 329.67) * mm, "radius": 2.54 * mm});
            skCircle(sketch, "E8.17.9.0", {"center": v(-6.98, 316.97) * mm, "radius": 2.54 * mm});
            skCircle(sketch, "E8.17.10.0", {"center": v(-7.06, 304.27) * mm, "radius": 2.54 * mm});
            skCircle(sketch, "E8.17.11.0", {"center": v(-7.15, 291.57) * mm, "radius": 2.54 * mm});
            skCircle(sketch, "E8.17.12.0", {"center": v(-7.23, 278.87) * mm, "radius": 2.54 * mm});
            skCircle(sketch, "E8.17.13.0", {"center": v(-7.31, 266.17) * mm, "radius": 2.54 * mm});
            skCircle(sketch, "E8.17.14.0", {"center": v(-7.4, 253.47) * mm, "radius": 2.54 * mm});
            skCircle(sketch, "E8.17.15.0", {"center": v(-7.48, 240.77) * mm, "radius": 2.54 * mm});
            skCircle(sketch, "E8.17.16.0", {"center": v(-7.57, 228.07) * mm, "radius": 2.54 * mm});
            skCircle(sketch, "E8.17.17.0", {"center": v(-7.65, 215.37) * mm, "radius": 2.54 * mm});
            skCircle(sketch, "E8.17.18.0", {"center": v(-7.73, 202.67) * mm, "radius": 2.54 * mm});
            skCircle(sketch, "E8.17.19.0", {"center": v(-7.82, 189.97) * mm, "radius": 2.54 * mm});
            skCircle(sketch, "E8.17.20.0", {"center": v(-7.9, 177.27) * mm, "radius": 2.54 * mm});
            skCircle(sketch, "E8.17.21.0", {"center": v(-7.99, 164.57) * mm, "radius": 2.54 * mm});
            skCircle(sketch, "E8.17.22.0", {"center": v(-8.07, 151.87) * mm, "radius": 2.54 * mm});
            skCircle(sketch, "E8.17.23.0", {"center": v(-8.15, 139.17) * mm, "radius": 2.54 * mm});
            skCircle(sketch, "E8.17.24.0", {"center": v(-8.24, 126.47) * mm, "radius": 2.54 * mm});
            skCircle(sketch, "E8.17.25.0", {"center": v(-8.32, 113.77) * mm, "radius": 2.54 * mm});
            skCircle(sketch, "E8.17.26.0", {"center": v(-8.4, 101.07) * mm, "radius": 2.54 * mm});
            skCircle(sketch, "E8.17.27.0", {"center": v(-8.49, 88.37) * mm, "radius": 2.54 * mm});
            skCircle(sketch, "E8.17.28.0", {"center": v(-8.57, 75.67) * mm, "radius": 2.54 * mm});
            skCircle(sketch, "E8.17.29.0", {"center": v(-8.66, 62.97) * mm, "radius": 2.54 * mm});
            skCircle(sketch, "E8.17.30.0", {"center": v(-8.74, 50.27) * mm, "radius": 2.54 * mm});
            skCircle(sketch, "E8.17.31.0", {"center": v(-8.83, 37.57) * mm, "radius": 2.54 * mm});
            skCircle(sketch, "E8.17.32.0", {"center": v(-8.9, 24.88) * mm, "radius": 2.54 * mm});
            skCircle(sketch, "E8.18.0.0", {"center": v(-18.92, 431.23) * mm, "radius": 2.54 * mm});
            skCircle(sketch, "E8.18.1.0", {"center": v(-19, 418.54) * mm, "radius": 2.54 * mm});
            skCircle(sketch, "E8.18.2.0", {"center": v(-19.09, 405.84) * mm, "radius": 2.54 * mm});
            skCircle(sketch, "E8.18.3.0", {"center": v(-19.17, 393.14) * mm, "radius": 2.54 * mm});
            skCircle(sketch, "E8.18.4.0", {"center": v(-19.26, 380.44) * mm, "radius": 2.54 * mm});
            skCircle(sketch, "E8.18.5.0", {"center": v(-19.34, 367.74) * mm, "radius": 2.54 * mm});
            skCircle(sketch, "E8.18.6.0", {"center": v(-19.42, 355.04) * mm, "radius": 2.54 * mm});
            skCircle(sketch, "E8.18.7.0", {"center": v(-19.5, 342.34) * mm, "radius": 2.54 * mm});
            skCircle(sketch, "E8.18.8.0", {"center": v(-19.6, 329.64) * mm, "radius": 2.54 * mm});
            skCircle(sketch, "E8.18.9.0", {"center": v(-19.68, 316.94) * mm, "radius": 2.54 * mm});
            skCircle(sketch, "E8.18.10.0", {"center": v(-19.76, 304.24) * mm, "radius": 2.54 * mm});
            skCircle(sketch, "E8.18.11.0", {"center": v(-19.85, 291.54) * mm, "radius": 2.54 * mm});
            skCircle(sketch, "E8.18.12.0", {"center": v(-19.93, 278.84) * mm, "radius": 2.54 * mm});
            skCircle(sketch, "E8.18.13.0", {"center": v(-20.01, 266.14) * mm, "radius": 2.54 * mm});
            skCircle(sketch, "E8.18.14.0", {"center": v(-20.1, 253.44) * mm, "radius": 2.54 * mm});
            skCircle(sketch, "E8.18.15.0", {"center": v(-20.18, 240.74) * mm, "radius": 2.54 * mm});
            skCircle(sketch, "E8.18.16.0", {"center": v(-20.27, 228.04) * mm, "radius": 2.54 * mm});
            skCircle(sketch, "E8.18.17.0", {"center": v(-20.35, 215.34) * mm, "radius": 2.54 * mm});
            skCircle(sketch, "E8.18.18.0", {"center": v(-20.43, 202.64) * mm, "radius": 2.54 * mm});
            skCircle(sketch, "E8.18.19.0", {"center": v(-20.52, 189.94) * mm, "radius": 2.54 * mm});
            skCircle(sketch, "E8.18.20.0", {"center": v(-20.6, 177.24) * mm, "radius": 2.54 * mm});
            skCircle(sketch, "E8.18.21.0", {"center": v(-20.69, 164.54) * mm, "radius": 2.54 * mm});
            skCircle(sketch, "E8.18.22.0", {"center": v(-20.77, 151.84) * mm, "radius": 2.54 * mm});
            skCircle(sketch, "E8.18.23.0", {"center": v(-20.85, 139.14) * mm, "radius": 2.54 * mm});
            skCircle(sketch, "E8.18.24.0", {"center": v(-20.94, 126.44) * mm, "radius": 2.54 * mm});
            skCircle(sketch, "E8.18.25.0", {"center": v(-21.02, 113.74) * mm, "radius": 2.54 * mm});
            skCircle(sketch, "E8.18.26.0", {"center": v(-21.1, 101.04) * mm, "radius": 2.54 * mm});
            skCircle(sketch, "E8.18.27.0", {"center": v(-21.19, 88.34) * mm, "radius": 2.54 * mm});
            skCircle(sketch, "E8.18.28.0", {"center": v(-21.27, 75.64) * mm, "radius": 2.54 * mm});
            skCircle(sketch, "E8.18.29.0", {"center": v(-21.36, 62.94) * mm, "radius": 2.54 * mm});
            skCircle(sketch, "E8.18.30.0", {"center": v(-21.44, 50.24) * mm, "radius": 2.54 * mm});
            skCircle(sketch, "E8.18.31.0", {"center": v(-21.53, 37.54) * mm, "radius": 2.54 * mm});
            skCircle(sketch, "E8.18.32.0", {"center": v(-21.6, 24.84) * mm, "radius": 2.54 * mm});
            skCircle(sketch, "E8.19.0.0", {"center": v(-31.62, 431.2) * mm, "radius": 2.54 * mm});
            skCircle(sketch, "E8.19.1.0", {"center": v(-31.7, 418.5) * mm, "radius": 2.54 * mm});
            skCircle(sketch, "E8.19.2.0", {"center": v(-31.79, 405.8) * mm, "radius": 2.54 * mm});
            skCircle(sketch, "E8.19.3.0", {"center": v(-31.87, 393.1) * mm, "radius": 2.54 * mm});
            skCircle(sketch, "E8.19.4.0", {"center": v(-31.96, 380.4) * mm, "radius": 2.54 * mm});
            skCircle(sketch, "E8.19.5.0", {"center": v(-32.04, 367.7) * mm, "radius": 2.54 * mm});
            skCircle(sketch, "E8.19.6.0", {"center": v(-32.12, 355) * mm, "radius": 2.54 * mm});
            skCircle(sketch, "E8.19.7.0", {"center": v(-32.2, 342.3) * mm, "radius": 2.54 * mm});
            skCircle(sketch, "E8.19.8.0", {"center": v(-32.3, 329.6) * mm, "radius": 2.54 * mm});
            skCircle(sketch, "E8.19.9.0", {"center": v(-32.38, 316.9) * mm, "radius": 2.54 * mm});
            skCircle(sketch, "E8.19.10.0", {"center": v(-32.46, 304.2) * mm, "radius": 2.54 * mm});
            skCircle(sketch, "E8.19.11.0", {"center": v(-32.55, 291.5) * mm, "radius": 2.54 * mm});
            skCircle(sketch, "E8.19.12.0", {"center": v(-32.63, 278.8) * mm, "radius": 2.54 * mm});
            skCircle(sketch, "E8.19.13.0", {"center": v(-32.71, 266.1) * mm, "radius": 2.54 * mm});
            skCircle(sketch, "E8.19.14.0", {"center": v(-32.8, 253.4) * mm, "radius": 2.54 * mm});
            skCircle(sketch, "E8.19.15.0", {"center": v(-32.88, 240.7) * mm, "radius": 2.54 * mm});
            skCircle(sketch, "E8.19.16.0", {"center": v(-32.97, 228) * mm, "radius": 2.54 * mm});
            skCircle(sketch, "E8.19.17.0", {"center": v(-33.05, 215.3) * mm, "radius": 2.54 * mm});
            skCircle(sketch, "E8.19.18.0", {"center": v(-33.13, 202.6) * mm, "radius": 2.54 * mm});
            skCircle(sketch, "E8.19.19.0", {"center": v(-33.22, 189.9) * mm, "radius": 2.54 * mm});
            skCircle(sketch, "E8.19.20.0", {"center": v(-33.3, 177.2) * mm, "radius": 2.54 * mm});
            skCircle(sketch, "E8.19.21.0", {"center": v(-33.39, 164.5) * mm, "radius": 2.54 * mm});
            skCircle(sketch, "E8.19.22.0", {"center": v(-33.47, 151.8) * mm, "radius": 2.54 * mm});
            skCircle(sketch, "E8.19.23.0", {"center": v(-33.55, 139.1) * mm, "radius": 2.54 * mm});
            skCircle(sketch, "E8.19.24.0", {"center": v(-33.64, 126.41) * mm, "radius": 2.54 * mm});
            skCircle(sketch, "E8.19.25.0", {"center": v(-33.72, 113.71) * mm, "radius": 2.54 * mm});
            skCircle(sketch, "E8.19.26.0", {"center": v(-33.8, 101.01) * mm, "radius": 2.54 * mm});
            skCircle(sketch, "E8.19.27.0", {"center": v(-33.89, 88.31) * mm, "radius": 2.54 * mm});
            skCircle(sketch, "E8.19.28.0", {"center": v(-33.97, 75.61) * mm, "radius": 2.54 * mm});
            skCircle(sketch, "E8.19.29.0", {"center": v(-34.06, 62.91) * mm, "radius": 2.54 * mm});
            skCircle(sketch, "E8.19.30.0", {"center": v(-34.14, 50.21) * mm, "radius": 2.54 * mm});
            skCircle(sketch, "E8.19.31.0", {"center": v(-34.23, 37.51) * mm, "radius": 2.54 * mm});
            skCircle(sketch, "E8.19.32.0", {"center": v(-34.3, 24.81) * mm, "radius": 2.54 * mm});
            skCircle(sketch, "E8.20.0.0", {"center": v(-44.32, 431.17) * mm, "radius": 2.54 * mm});
            skCircle(sketch, "E8.20.1.0", {"center": v(-44.4, 418.47) * mm, "radius": 2.54 * mm});
            skCircle(sketch, "E8.20.2.0", {"center": v(-44.49, 405.77) * mm, "radius": 2.54 * mm});
            skCircle(sketch, "E8.20.3.0", {"center": v(-44.57, 393.07) * mm, "radius": 2.54 * mm});
            skCircle(sketch, "E8.20.4.0", {"center": v(-44.66, 380.37) * mm, "radius": 2.54 * mm});
            skCircle(sketch, "E8.20.5.0", {"center": v(-44.74, 367.67) * mm, "radius": 2.54 * mm});
            skCircle(sketch, "E8.20.6.0", {"center": v(-44.82, 354.97) * mm, "radius": 2.54 * mm});
            skCircle(sketch, "E8.20.7.0", {"center": v(-44.9, 342.27) * mm, "radius": 2.54 * mm});
            skCircle(sketch, "E8.20.8.0", {"center": v(-45, 329.57) * mm, "radius": 2.54 * mm});
            skCircle(sketch, "E8.20.9.0", {"center": v(-45.08, 316.87) * mm, "radius": 2.54 * mm});
            skCircle(sketch, "E8.20.10.0", {"center": v(-45.16, 304.17) * mm, "radius": 2.54 * mm});
            skCircle(sketch, "E8.20.11.0", {"center": v(-45.25, 291.48) * mm, "radius": 2.54 * mm});
            skCircle(sketch, "E8.20.12.0", {"center": v(-45.33, 278.78) * mm, "radius": 2.54 * mm});
            skCircle(sketch, "E8.20.13.0", {"center": v(-45.41, 266.08) * mm, "radius": 2.54 * mm});
            skCircle(sketch, "E8.20.14.0", {"center": v(-45.5, 253.38) * mm, "radius": 2.54 * mm});
            skCircle(sketch, "E8.20.15.0", {"center": v(-45.58, 240.68) * mm, "radius": 2.54 * mm});
            skCircle(sketch, "E8.20.16.0", {"center": v(-45.67, 227.98) * mm, "radius": 2.54 * mm});
            skCircle(sketch, "E8.20.17.0", {"center": v(-45.75, 215.28) * mm, "radius": 2.54 * mm});
            skCircle(sketch, "E8.20.18.0", {"center": v(-45.83, 202.58) * mm, "radius": 2.54 * mm});
            skCircle(sketch, "E8.20.19.0", {"center": v(-45.92, 189.88) * mm, "radius": 2.54 * mm});
            skCircle(sketch, "E8.20.20.0", {"center": v(-46, 177.18) * mm, "radius": 2.54 * mm});
            skCircle(sketch, "E8.20.21.0", {"center": v(-46.09, 164.48) * mm, "radius": 2.54 * mm});
            skCircle(sketch, "E8.20.22.0", {"center": v(-46.17, 151.78) * mm, "radius": 2.54 * mm});
            skCircle(sketch, "E8.20.23.0", {"center": v(-46.25, 139.08) * mm, "radius": 2.54 * mm});
            skCircle(sketch, "E8.20.24.0", {"center": v(-46.34, 126.38) * mm, "radius": 2.54 * mm});
            skCircle(sketch, "E8.20.25.0", {"center": v(-46.42, 113.68) * mm, "radius": 2.54 * mm});
            skCircle(sketch, "E8.20.26.0", {"center": v(-46.5, 100.98) * mm, "radius": 2.54 * mm});
            skCircle(sketch, "E8.20.27.0", {"center": v(-46.59, 88.28) * mm, "radius": 2.54 * mm});
            skCircle(sketch, "E8.20.28.0", {"center": v(-46.67, 75.58) * mm, "radius": 2.54 * mm});
            skCircle(sketch, "E8.20.29.0", {"center": v(-46.76, 62.88) * mm, "radius": 2.54 * mm});
            skCircle(sketch, "E8.20.30.0", {"center": v(-46.84, 50.18) * mm, "radius": 2.54 * mm});
            skCircle(sketch, "E8.20.31.0", {"center": v(-46.93, 37.48) * mm, "radius": 2.54 * mm});
            skCircle(sketch, "E8.20.32.0", {"center": v(-47, 24.78) * mm, "radius": 2.54 * mm});
            skCircle(sketch, "E8.21.0.0", {"center": v(-57.02, 431.14) * mm, "radius": 2.54 * mm});
            skCircle(sketch, "E8.21.1.0", {"center": v(-57.1, 418.44) * mm, "radius": 2.54 * mm});
            skCircle(sketch, "E8.21.2.0", {"center": v(-57.19, 405.74) * mm, "radius": 2.54 * mm});
            skCircle(sketch, "E8.21.3.0", {"center": v(-57.27, 393.04) * mm, "radius": 2.54 * mm});
            skCircle(sketch, "E8.21.4.0", {"center": v(-57.36, 380.34) * mm, "radius": 2.54 * mm});
            skCircle(sketch, "E8.21.5.0", {"center": v(-57.44, 367.64) * mm, "radius": 2.54 * mm});
            skCircle(sketch, "E8.21.6.0", {"center": v(-57.52, 354.94) * mm, "radius": 2.54 * mm});
            skCircle(sketch, "E8.21.7.0", {"center": v(-57.6, 342.24) * mm, "radius": 2.54 * mm});
            skCircle(sketch, "E8.21.8.0", {"center": v(-57.7, 329.54) * mm, "radius": 2.54 * mm});
            skCircle(sketch, "E8.21.9.0", {"center": v(-57.78, 316.84) * mm, "radius": 2.54 * mm});
            skCircle(sketch, "E8.21.10.0", {"center": v(-57.86, 304.14) * mm, "radius": 2.54 * mm});
            skCircle(sketch, "E8.21.11.0", {"center": v(-57.95, 291.44) * mm, "radius": 2.54 * mm});
            skCircle(sketch, "E8.21.12.0", {"center": v(-58.03, 278.74) * mm, "radius": 2.54 * mm});
            skCircle(sketch, "E8.21.13.0", {"center": v(-58.11, 266.04) * mm, "radius": 2.54 * mm});
            skCircle(sketch, "E8.21.14.0", {"center": v(-58.2, 253.34) * mm, "radius": 2.54 * mm});
            skCircle(sketch, "E8.21.15.0", {"center": v(-58.28, 240.64) * mm, "radius": 2.54 * mm});
            skCircle(sketch, "E8.21.16.0", {"center": v(-58.37, 227.95) * mm, "radius": 2.54 * mm});
            skCircle(sketch, "E8.21.17.0", {"center": v(-58.45, 215.25) * mm, "radius": 2.54 * mm});
            skCircle(sketch, "E8.21.18.0", {"center": v(-58.53, 202.55) * mm, "radius": 2.54 * mm});
            skCircle(sketch, "E8.21.19.0", {"center": v(-58.62, 189.85) * mm, "radius": 2.54 * mm});
            skCircle(sketch, "E8.21.20.0", {"center": v(-58.7, 177.15) * mm, "radius": 2.54 * mm});
            skCircle(sketch, "E8.21.21.0", {"center": v(-58.79, 164.45) * mm, "radius": 2.54 * mm});
            skCircle(sketch, "E8.21.22.0", {"center": v(-58.87, 151.75) * mm, "radius": 2.54 * mm});
            skCircle(sketch, "E8.21.23.0", {"center": v(-58.95, 139.05) * mm, "radius": 2.54 * mm});
            skCircle(sketch, "E8.21.24.0", {"center": v(-59.04, 126.35) * mm, "radius": 2.54 * mm});
            skCircle(sketch, "E8.21.25.0", {"center": v(-59.12, 113.65) * mm, "radius": 2.54 * mm});
            skCircle(sketch, "E8.21.26.0", {"center": v(-59.2, 100.95) * mm, "radius": 2.54 * mm});
            skCircle(sketch, "E8.21.27.0", {"center": v(-59.29, 88.25) * mm, "radius": 2.54 * mm});
            skCircle(sketch, "E8.21.28.0", {"center": v(-59.37, 75.55) * mm, "radius": 2.54 * mm});
            skCircle(sketch, "E8.21.29.0", {"center": v(-59.46, 62.85) * mm, "radius": 2.54 * mm});
            skCircle(sketch, "E8.21.30.0", {"center": v(-59.54, 50.15) * mm, "radius": 2.54 * mm});
            skCircle(sketch, "E8.21.31.0", {"center": v(-59.63, 37.45) * mm, "radius": 2.54 * mm});
            skCircle(sketch, "E8.21.32.0", {"center": v(-59.7, 24.75) * mm, "radius": 2.54 * mm});
            skCircle(sketch, "E8.22.0.0", {"center": v(-69.72, 431.1) * mm, "radius": 2.54 * mm});
            skCircle(sketch, "E8.22.1.0", {"center": v(-69.8, 418.4) * mm, "radius": 2.54 * mm});
            skCircle(sketch, "E8.22.2.0", {"center": v(-69.89, 405.7) * mm, "radius": 2.54 * mm});
            skCircle(sketch, "E8.22.3.0", {"center": v(-69.97, 393) * mm, "radius": 2.54 * mm});
            skCircle(sketch, "E8.22.4.0", {"center": v(-70.06, 380.31) * mm, "radius": 2.54 * mm});
            skCircle(sketch, "E8.22.5.0", {"center": v(-70.14, 367.61) * mm, "radius": 2.54 * mm});
            skCircle(sketch, "E8.22.6.0", {"center": v(-70.22, 354.91) * mm, "radius": 2.54 * mm});
            skCircle(sketch, "E8.22.7.0", {"center": v(-70.3, 342.21) * mm, "radius": 2.54 * mm});
            skCircle(sketch, "E8.22.8.0", {"center": v(-70.4, 329.51) * mm, "radius": 2.54 * mm});
            skCircle(sketch, "E8.22.9.0", {"center": v(-70.48, 316.81) * mm, "radius": 2.54 * mm});
            skCircle(sketch, "E8.22.10.0", {"center": v(-70.56, 304.11) * mm, "radius": 2.54 * mm});
            skCircle(sketch, "E8.22.11.0", {"center": v(-70.65, 291.41) * mm, "radius": 2.54 * mm});
            skCircle(sketch, "E8.22.12.0", {"center": v(-70.73, 278.71) * mm, "radius": 2.54 * mm});
            skCircle(sketch, "E8.22.13.0", {"center": v(-70.81, 266.01) * mm, "radius": 2.54 * mm});
            skCircle(sketch, "E8.22.14.0", {"center": v(-70.9, 253.31) * mm, "radius": 2.54 * mm});
            skCircle(sketch, "E8.22.15.0", {"center": v(-70.98, 240.61) * mm, "radius": 2.54 * mm});
            skCircle(sketch, "E8.22.16.0", {"center": v(-71.07, 227.91) * mm, "radius": 2.54 * mm});
            skCircle(sketch, "E8.22.17.0", {"center": v(-71.15, 215.21) * mm, "radius": 2.54 * mm});
            skCircle(sketch, "E8.22.18.0", {"center": v(-71.23, 202.51) * mm, "radius": 2.54 * mm});
            skCircle(sketch, "E8.22.19.0", {"center": v(-71.32, 189.81) * mm, "radius": 2.54 * mm});
            skCircle(sketch, "E8.22.20.0", {"center": v(-71.4, 177.11) * mm, "radius": 2.54 * mm});
            skCircle(sketch, "E8.22.21.0", {"center": v(-71.49, 164.41) * mm, "radius": 2.54 * mm});
            skCircle(sketch, "E8.22.22.0", {"center": v(-71.57, 151.72) * mm, "radius": 2.54 * mm});
            skCircle(sketch, "E8.22.23.0", {"center": v(-71.65, 139.02) * mm, "radius": 2.54 * mm});
            skCircle(sketch, "E8.22.24.0", {"center": v(-71.74, 126.32) * mm, "radius": 2.54 * mm});
            skCircle(sketch, "E8.22.25.0", {"center": v(-71.82, 113.62) * mm, "radius": 2.54 * mm});
            skCircle(sketch, "E8.22.26.0", {"center": v(-71.9, 100.92) * mm, "radius": 2.54 * mm});
            skCircle(sketch, "E8.22.27.0", {"center": v(-71.99, 88.22) * mm, "radius": 2.54 * mm});
            skCircle(sketch, "E8.22.28.0", {"center": v(-72.07, 75.52) * mm, "radius": 2.54 * mm});
            skCircle(sketch, "E8.22.29.0", {"center": v(-72.16, 62.82) * mm, "radius": 2.54 * mm});
            skCircle(sketch, "E8.22.30.0", {"center": v(-72.24, 50.12) * mm, "radius": 2.54 * mm});
            skCircle(sketch, "E8.22.31.0", {"center": v(-72.33, 37.42) * mm, "radius": 2.54 * mm});
            skCircle(sketch, "E8.22.32.0", {"center": v(-72.4, 24.72) * mm, "radius": 2.54 * mm});
            skCircle(sketch, "E8.23.0.0", {"center": v(-82.42, 431.08) * mm, "radius": 2.54 * mm});
            skCircle(sketch, "E8.23.1.0", {"center": v(-82.5, 418.38) * mm, "radius": 2.54 * mm});
            skCircle(sketch, "E8.23.2.0", {"center": v(-82.59, 405.68) * mm, "radius": 2.54 * mm});
            skCircle(sketch, "E8.23.3.0", {"center": v(-82.67, 392.98) * mm, "radius": 2.54 * mm});
            skCircle(sketch, "E8.23.4.0", {"center": v(-82.76, 380.28) * mm, "radius": 2.54 * mm});
            skCircle(sketch, "E8.23.5.0", {"center": v(-82.84, 367.58) * mm, "radius": 2.54 * mm});
            skCircle(sketch, "E8.23.6.0", {"center": v(-82.92, 354.88) * mm, "radius": 2.54 * mm});
            skCircle(sketch, "E8.23.7.0", {"center": v(-83, 342.18) * mm, "radius": 2.54 * mm});
            skCircle(sketch, "E8.23.8.0", {"center": v(-83.1, 329.48) * mm, "radius": 2.54 * mm});
            skCircle(sketch, "E8.23.9.0", {"center": v(-83.18, 316.78) * mm, "radius": 2.54 * mm});
            skCircle(sketch, "E8.23.10.0", {"center": v(-83.26, 304.08) * mm, "radius": 2.54 * mm});
            skCircle(sketch, "E8.23.11.0", {"center": v(-83.34, 291.38) * mm, "radius": 2.54 * mm});
            skCircle(sketch, "E8.23.12.0", {"center": v(-83.43, 278.68) * mm, "radius": 2.54 * mm});
            skCircle(sketch, "E8.23.13.0", {"center": v(-83.51, 265.98) * mm, "radius": 2.54 * mm});
            skCircle(sketch, "E8.23.14.0", {"center": v(-83.6, 253.28) * mm, "radius": 2.54 * mm});
            skCircle(sketch, "E8.23.15.0", {"center": v(-83.68, 240.58) * mm, "radius": 2.54 * mm});
            skCircle(sketch, "E8.23.16.0", {"center": v(-83.77, 227.88) * mm, "radius": 2.54 * mm});
            skCircle(sketch, "E8.23.17.0", {"center": v(-83.85, 215.18) * mm, "radius": 2.54 * mm});
            skCircle(sketch, "E8.23.18.0", {"center": v(-83.93, 202.48) * mm, "radius": 2.54 * mm});
            skCircle(sketch, "E8.23.19.0", {"center": v(-84.02, 189.78) * mm, "radius": 2.54 * mm});
            skCircle(sketch, "E8.23.20.0", {"center": v(-84.1, 177.08) * mm, "radius": 2.54 * mm});
            skCircle(sketch, "E8.23.21.0", {"center": v(-84.19, 164.38) * mm, "radius": 2.54 * mm});
            skCircle(sketch, "E8.23.22.0", {"center": v(-84.27, 151.68) * mm, "radius": 2.54 * mm});
            skCircle(sketch, "E8.23.23.0", {"center": v(-84.35, 138.98) * mm, "radius": 2.54 * mm});
            skCircle(sketch, "E8.23.24.0", {"center": v(-84.44, 126.28) * mm, "radius": 2.54 * mm});
            skCircle(sketch, "E8.23.25.0", {"center": v(-84.52, 113.58) * mm, "radius": 2.54 * mm});
            skCircle(sketch, "E8.23.26.0", {"center": v(-84.6, 100.88) * mm, "radius": 2.54 * mm});
            skCircle(sketch, "E8.23.27.0", {"center": v(-84.69, 88.19) * mm, "radius": 2.54 * mm});
            skCircle(sketch, "E8.23.28.0", {"center": v(-84.77, 75.49) * mm, "radius": 2.54 * mm});
            skCircle(sketch, "E8.23.29.0", {"center": v(-84.86, 62.79) * mm, "radius": 2.54 * mm});
            skCircle(sketch, "E8.23.30.0", {"center": v(-84.94, 50.09) * mm, "radius": 2.54 * mm});
            skCircle(sketch, "E8.23.31.0", {"center": v(-85.03, 37.39) * mm, "radius": 2.54 * mm});
            skCircle(sketch, "E8.23.32.0", {"center": v(-85.1, 24.69) * mm, "radius": 2.54 * mm});
            skCircle(sketch, "E8.24.0.0", {"center": v(-95.12, 431.05) * mm, "radius": 2.54 * mm});
            skCircle(sketch, "E8.24.1.0", {"center": v(-95.2, 418.35) * mm, "radius": 2.54 * mm});
            skCircle(sketch, "E8.24.2.0", {"center": v(-95.29, 405.65) * mm, "radius": 2.54 * mm});
            skCircle(sketch, "E8.24.3.0", {"center": v(-95.37, 392.95) * mm, "radius": 2.54 * mm});
            skCircle(sketch, "E8.24.4.0", {"center": v(-95.46, 380.25) * mm, "radius": 2.54 * mm});
            skCircle(sketch, "E8.24.5.0", {"center": v(-95.54, 367.55) * mm, "radius": 2.54 * mm});
            skCircle(sketch, "E8.24.6.0", {"center": v(-95.62, 354.85) * mm, "radius": 2.54 * mm});
            skCircle(sketch, "E8.24.7.0", {"center": v(-95.7, 342.15) * mm, "radius": 2.54 * mm});
            skCircle(sketch, "E8.24.8.0", {"center": v(-95.8, 329.45) * mm, "radius": 2.54 * mm});
            skCircle(sketch, "E8.24.9.0", {"center": v(-95.88, 316.75) * mm, "radius": 2.54 * mm});
            skCircle(sketch, "E8.24.10.0", {"center": v(-95.96, 304.05) * mm, "radius": 2.54 * mm});
            skCircle(sketch, "E8.24.11.0", {"center": v(-96.04, 291.35) * mm, "radius": 2.54 * mm});
            skCircle(sketch, "E8.24.12.0", {"center": v(-96.13, 278.65) * mm, "radius": 2.54 * mm});
            skCircle(sketch, "E8.24.13.0", {"center": v(-96.21, 265.95) * mm, "radius": 2.54 * mm});
            skCircle(sketch, "E8.24.14.0", {"center": v(-96.3, 253.25) * mm, "radius": 2.54 * mm});
            skCircle(sketch, "E8.24.15.0", {"center": v(-96.38, 240.55) * mm, "radius": 2.54 * mm});
            skCircle(sketch, "E8.24.16.0", {"center": v(-96.47, 227.85) * mm, "radius": 2.54 * mm});
            skCircle(sketch, "E8.24.17.0", {"center": v(-96.55, 215.15) * mm, "radius": 2.54 * mm});
            skCircle(sketch, "E8.24.18.0", {"center": v(-96.63, 202.45) * mm, "radius": 2.54 * mm});
            skCircle(sketch, "E8.24.19.0", {"center": v(-96.72, 189.75) * mm, "radius": 2.54 * mm});
            skCircle(sketch, "E8.24.20.0", {"center": v(-96.8, 177.05) * mm, "radius": 2.54 * mm});
            skCircle(sketch, "E8.24.21.0", {"center": v(-96.89, 164.35) * mm, "radius": 2.54 * mm});
            skCircle(sketch, "E8.24.22.0", {"center": v(-96.97, 151.65) * mm, "radius": 2.54 * mm});
            skCircle(sketch, "E8.24.23.0", {"center": v(-97.05, 138.95) * mm, "radius": 2.54 * mm});
            skCircle(sketch, "E8.24.24.0", {"center": v(-97.14, 126.25) * mm, "radius": 2.54 * mm});
            skCircle(sketch, "E8.24.25.0", {"center": v(-97.22, 113.55) * mm, "radius": 2.54 * mm});
            skCircle(sketch, "E8.24.26.0", {"center": v(-97.3, 100.85) * mm, "radius": 2.54 * mm});
            skCircle(sketch, "E8.24.27.0", {"center": v(-97.39, 88.15) * mm, "radius": 2.54 * mm});
            skCircle(sketch, "E8.24.28.0", {"center": v(-97.47, 75.45) * mm, "radius": 2.54 * mm});
            skCircle(sketch, "E8.24.29.0", {"center": v(-97.56, 62.75) * mm, "radius": 2.54 * mm});
            skCircle(sketch, "E8.24.30.0", {"center": v(-97.64, 50.05) * mm, "radius": 2.54 * mm});
            skCircle(sketch, "E8.24.31.0", {"center": v(-97.73, 37.35) * mm, "radius": 2.54 * mm});
            skCircle(sketch, "E8.24.32.0", {"center": v(-97.8, 24.66) * mm, "radius": 2.54 * mm});
            skCircle(sketch, "E8.25.0.0", {"center": v(-107.82, 431.01) * mm, "radius": 2.54 * mm});
            skCircle(sketch, "E8.25.1.0", {"center": v(-107.9, 418.32) * mm, "radius": 2.54 * mm});
            skCircle(sketch, "E8.25.2.0", {"center": v(-107.99, 405.62) * mm, "radius": 2.54 * mm});
            skCircle(sketch, "E8.25.3.0", {"center": v(-108.07, 392.92) * mm, "radius": 2.54 * mm});
            skCircle(sketch, "E8.25.4.0", {"center": v(-108.16, 380.22) * mm, "radius": 2.54 * mm});
            skCircle(sketch, "E8.25.5.0", {"center": v(-108.24, 367.52) * mm, "radius": 2.54 * mm});
            skCircle(sketch, "E8.25.6.0", {"center": v(-108.32, 354.82) * mm, "radius": 2.54 * mm});
            skCircle(sketch, "E8.25.7.0", {"center": v(-108.4, 342.12) * mm, "radius": 2.54 * mm});
            skCircle(sketch, "E8.25.8.0", {"center": v(-108.5, 329.42) * mm, "radius": 2.54 * mm});
            skCircle(sketch, "E8.25.9.0", {"center": v(-108.58, 316.72) * mm, "radius": 2.54 * mm});
            skCircle(sketch, "E8.25.10.0", {"center": v(-108.66, 304.02) * mm, "radius": 2.54 * mm});
            skCircle(sketch, "E8.25.11.0", {"center": v(-108.74, 291.32) * mm, "radius": 2.54 * mm});
            skCircle(sketch, "E8.25.12.0", {"center": v(-108.83, 278.62) * mm, "radius": 2.54 * mm});
            skCircle(sketch, "E8.25.13.0", {"center": v(-108.91, 265.92) * mm, "radius": 2.54 * mm});
            skCircle(sketch, "E8.25.14.0", {"center": v(-109, 253.22) * mm, "radius": 2.54 * mm});
            skCircle(sketch, "E8.25.15.0", {"center": v(-109.08, 240.52) * mm, "radius": 2.54 * mm});
            skCircle(sketch, "E8.25.16.0", {"center": v(-109.17, 227.82) * mm, "radius": 2.54 * mm});
            skCircle(sketch, "E8.25.17.0", {"center": v(-109.25, 215.12) * mm, "radius": 2.54 * mm});
            skCircle(sketch, "E8.25.18.0", {"center": v(-109.33, 202.42) * mm, "radius": 2.54 * mm});
            skCircle(sketch, "E8.25.19.0", {"center": v(-109.42, 189.72) * mm, "radius": 2.54 * mm});
            skCircle(sketch, "E8.25.20.0", {"center": v(-109.5, 177.02) * mm, "radius": 2.54 * mm});
            skCircle(sketch, "E8.25.21.0", {"center": v(-109.59, 164.32) * mm, "radius": 2.54 * mm});
            skCircle(sketch, "E8.25.22.0", {"center": v(-109.67, 151.62) * mm, "radius": 2.54 * mm});
            skCircle(sketch, "E8.25.23.0", {"center": v(-109.75, 138.92) * mm, "radius": 2.54 * mm});
            skCircle(sketch, "E8.25.24.0", {"center": v(-109.84, 126.22) * mm, "radius": 2.54 * mm});
            skCircle(sketch, "E8.25.25.0", {"center": v(-109.92, 113.52) * mm, "radius": 2.54 * mm});
            skCircle(sketch, "E8.25.26.0", {"center": v(-110, 100.82) * mm, "radius": 2.54 * mm});
            skCircle(sketch, "E8.25.27.0", {"center": v(-110.09, 88.12) * mm, "radius": 2.54 * mm});
            skCircle(sketch, "E8.25.28.0", {"center": v(-110.17, 75.42) * mm, "radius": 2.54 * mm});
            skCircle(sketch, "E8.25.29.0", {"center": v(-110.26, 62.72) * mm, "radius": 2.54 * mm});
            skCircle(sketch, "E8.25.30.0", {"center": v(-110.34, 50.02) * mm, "radius": 2.54 * mm});
            skCircle(sketch, "E8.25.31.0", {"center": v(-110.43, 37.32) * mm, "radius": 2.54 * mm});
            skCircle(sketch, "E8.25.32.0", {"center": v(-110.5, 24.62) * mm, "radius": 2.54 * mm});
            skCircle(sketch, "E8.26.0.0", {"center": v(-120.52, 430.98) * mm, "radius": 2.54 * mm});
            skCircle(sketch, "E8.26.1.0", {"center": v(-120.6, 418.28) * mm, "radius": 2.54 * mm});
            skCircle(sketch, "E8.26.2.0", {"center": v(-120.69, 405.58) * mm, "radius": 2.54 * mm});
            skCircle(sketch, "E8.26.3.0", {"center": v(-120.77, 392.88) * mm, "radius": 2.54 * mm});
            skCircle(sketch, "E8.26.4.0", {"center": v(-120.86, 380.18) * mm, "radius": 2.54 * mm});
            skCircle(sketch, "E8.26.5.0", {"center": v(-120.94, 367.48) * mm, "radius": 2.54 * mm});
            skCircle(sketch, "E8.26.6.0", {"center": v(-121.02, 354.79) * mm, "radius": 2.54 * mm});
            skCircle(sketch, "E8.26.7.0", {"center": v(-121.1, 342.09) * mm, "radius": 2.54 * mm});
            skCircle(sketch, "E8.26.8.0", {"center": v(-121.2, 329.39) * mm, "radius": 2.54 * mm});
            skCircle(sketch, "E8.26.9.0", {"center": v(-121.28, 316.69) * mm, "radius": 2.54 * mm});
            skCircle(sketch, "E8.26.10.0", {"center": v(-121.36, 303.99) * mm, "radius": 2.54 * mm});
            skCircle(sketch, "E8.26.11.0", {"center": v(-121.44, 291.29) * mm, "radius": 2.54 * mm});
            skCircle(sketch, "E8.26.12.0", {"center": v(-121.53, 278.59) * mm, "radius": 2.54 * mm});
            skCircle(sketch, "E8.26.13.0", {"center": v(-121.61, 265.89) * mm, "radius": 2.54 * mm});
            skCircle(sketch, "E8.26.14.0", {"center": v(-121.7, 253.19) * mm, "radius": 2.54 * mm});
            skCircle(sketch, "E8.26.15.0", {"center": v(-121.78, 240.49) * mm, "radius": 2.54 * mm});
            skCircle(sketch, "E8.26.16.0", {"center": v(-121.87, 227.79) * mm, "radius": 2.54 * mm});
            skCircle(sketch, "E8.26.17.0", {"center": v(-121.95, 215.09) * mm, "radius": 2.54 * mm});
            skCircle(sketch, "E8.26.18.0", {"center": v(-122.03, 202.39) * mm, "radius": 2.54 * mm});
            skCircle(sketch, "E8.26.19.0", {"center": v(-122.12, 189.69) * mm, "radius": 2.54 * mm});
            skCircle(sketch, "E8.26.20.0", {"center": v(-122.2, 176.99) * mm, "radius": 2.54 * mm});
            skCircle(sketch, "E8.26.21.0", {"center": v(-122.29, 164.29) * mm, "radius": 2.54 * mm});
            skCircle(sketch, "E8.26.22.0", {"center": v(-122.37, 151.59) * mm, "radius": 2.54 * mm});
            skCircle(sketch, "E8.26.23.0", {"center": v(-122.45, 138.89) * mm, "radius": 2.54 * mm});
            skCircle(sketch, "E8.26.24.0", {"center": v(-122.54, 126.2) * mm, "radius": 2.54 * mm});
            skCircle(sketch, "E8.26.25.0", {"center": v(-122.62, 113.5) * mm, "radius": 2.54 * mm});
            skCircle(sketch, "E8.26.26.0", {"center": v(-122.7, 100.8) * mm, "radius": 2.54 * mm});
            skCircle(sketch, "E8.26.27.0", {"center": v(-122.79, 88.1) * mm, "radius": 2.54 * mm});
            skCircle(sketch, "E8.26.28.0", {"center": v(-122.87, 75.4) * mm, "radius": 2.54 * mm});
            skCircle(sketch, "E8.26.29.0", {"center": v(-122.96, 62.7) * mm, "radius": 2.54 * mm});
            skCircle(sketch, "E8.26.30.0", {"center": v(-123.04, 50) * mm, "radius": 2.54 * mm});
            skCircle(sketch, "E8.26.31.0", {"center": v(-123.13, 37.3) * mm, "radius": 2.54 * mm});
            skCircle(sketch, "E8.26.32.0", {"center": v(-123.2, 24.6) * mm, "radius": 2.54 * mm});
            skCircle(sketch, "E8.27.0.0", {"center": v(-133.22, 430.95) * mm, "radius": 2.54 * mm});
            skCircle(sketch, "E8.27.1.0", {"center": v(-133.3, 418.25) * mm, "radius": 2.54 * mm});
            skCircle(sketch, "E8.27.2.0", {"center": v(-133.39, 405.55) * mm, "radius": 2.54 * mm});
            skCircle(sketch, "E8.27.3.0", {"center": v(-133.47, 392.85) * mm, "radius": 2.54 * mm});
            skCircle(sketch, "E8.27.4.0", {"center": v(-133.56, 380.15) * mm, "radius": 2.54 * mm});
            skCircle(sketch, "E8.27.5.0", {"center": v(-133.64, 367.45) * mm, "radius": 2.54 * mm});
            skCircle(sketch, "E8.27.6.0", {"center": v(-133.72, 354.75) * mm, "radius": 2.54 * mm});
            skCircle(sketch, "E8.27.7.0", {"center": v(-133.8, 342.05) * mm, "radius": 2.54 * mm});
            skCircle(sketch, "E8.27.8.0", {"center": v(-133.9, 329.35) * mm, "radius": 2.54 * mm});
            skCircle(sketch, "E8.27.9.0", {"center": v(-133.98, 316.65) * mm, "radius": 2.54 * mm});
            skCircle(sketch, "E8.27.10.0", {"center": v(-134.06, 303.95) * mm, "radius": 2.54 * mm});
            skCircle(sketch, "E8.27.11.0", {"center": v(-134.14, 291.26) * mm, "radius": 2.54 * mm});
            skCircle(sketch, "E8.27.12.0", {"center": v(-134.23, 278.56) * mm, "radius": 2.54 * mm});
            skCircle(sketch, "E8.27.13.0", {"center": v(-134.31, 265.86) * mm, "radius": 2.54 * mm});
            skCircle(sketch, "E8.27.14.0", {"center": v(-134.4, 253.16) * mm, "radius": 2.54 * mm});
            skCircle(sketch, "E8.27.15.0", {"center": v(-134.48, 240.46) * mm, "radius": 2.54 * mm});
            skCircle(sketch, "E8.27.16.0", {"center": v(-134.56, 227.76) * mm, "radius": 2.54 * mm});
            skCircle(sketch, "E8.27.17.0", {"center": v(-134.65, 215.06) * mm, "radius": 2.54 * mm});
            skCircle(sketch, "E8.27.18.0", {"center": v(-134.73, 202.36) * mm, "radius": 2.54 * mm});
            skCircle(sketch, "E8.27.19.0", {"center": v(-134.82, 189.66) * mm, "radius": 2.54 * mm});
            skCircle(sketch, "E8.27.20.0", {"center": v(-134.9, 176.96) * mm, "radius": 2.54 * mm});
            skCircle(sketch, "E8.27.21.0", {"center": v(-134.99, 164.26) * mm, "radius": 2.54 * mm});
            skCircle(sketch, "E8.27.22.0", {"center": v(-135.07, 151.56) * mm, "radius": 2.54 * mm});
            skCircle(sketch, "E8.27.23.0", {"center": v(-135.15, 138.86) * mm, "radius": 2.54 * mm});
            skCircle(sketch, "E8.27.24.0", {"center": v(-135.24, 126.16) * mm, "radius": 2.54 * mm});
            skCircle(sketch, "E8.27.25.0", {"center": v(-135.32, 113.46) * mm, "radius": 2.54 * mm});
            skCircle(sketch, "E8.27.26.0", {"center": v(-135.4, 100.76) * mm, "radius": 2.54 * mm});
            skCircle(sketch, "E8.27.27.0", {"center": v(-135.49, 88.06) * mm, "radius": 2.54 * mm});
            skCircle(sketch, "E8.27.28.0", {"center": v(-135.57, 75.36) * mm, "radius": 2.54 * mm});
            skCircle(sketch, "E8.27.29.0", {"center": v(-135.66, 62.66) * mm, "radius": 2.54 * mm});
            skCircle(sketch, "E8.27.30.0", {"center": v(-135.74, 49.96) * mm, "radius": 2.54 * mm});
            skCircle(sketch, "E8.27.31.0", {"center": v(-135.83, 37.26) * mm, "radius": 2.54 * mm});
            skCircle(sketch, "E8.27.32.0", {"center": v(-135.9, 24.56) * mm, "radius": 2.54 * mm});
            skCircle(sketch, "E8.28.0.0", {"center": v(-145.92, 430.92) * mm, "radius": 2.54 * mm});
            skCircle(sketch, "E8.28.1.0", {"center": v(-146, 418.22) * mm, "radius": 2.54 * mm});
            skCircle(sketch, "E8.28.2.0", {"center": v(-146.09, 405.52) * mm, "radius": 2.54 * mm});
            skCircle(sketch, "E8.28.3.0", {"center": v(-146.17, 392.82) * mm, "radius": 2.54 * mm});
            skCircle(sketch, "E8.28.4.0", {"center": v(-146.26, 380.12) * mm, "radius": 2.54 * mm});
            skCircle(sketch, "E8.28.5.0", {"center": v(-146.34, 367.42) * mm, "radius": 2.54 * mm});
            skCircle(sketch, "E8.28.6.0", {"center": v(-146.42, 354.72) * mm, "radius": 2.54 * mm});
            skCircle(sketch, "E8.28.7.0", {"center": v(-146.5, 342.02) * mm, "radius": 2.54 * mm});
            skCircle(sketch, "E8.28.8.0", {"center": v(-146.6, 329.32) * mm, "radius": 2.54 * mm});
            skCircle(sketch, "E8.28.9.0", {"center": v(-146.68, 316.62) * mm, "radius": 2.54 * mm});
            skCircle(sketch, "E8.28.10.0", {"center": v(-146.76, 303.92) * mm, "radius": 2.54 * mm});
            skCircle(sketch, "E8.28.11.0", {"center": v(-146.84, 291.22) * mm, "radius": 2.54 * mm});
            skCircle(sketch, "E8.28.12.0", {"center": v(-146.93, 278.52) * mm, "radius": 2.54 * mm});
            skCircle(sketch, "E8.28.13.0", {"center": v(-147.01, 265.82) * mm, "radius": 2.54 * mm});
            skCircle(sketch, "E8.28.14.0", {"center": v(-147.1, 253.12) * mm, "radius": 2.54 * mm});
            skCircle(sketch, "E8.28.15.0", {"center": v(-147.18, 240.42) * mm, "radius": 2.54 * mm});
            skCircle(sketch, "E8.28.16.0", {"center": v(-147.26, 227.73) * mm, "radius": 2.54 * mm});
            skCircle(sketch, "E8.28.17.0", {"center": v(-147.35, 215.03) * mm, "radius": 2.54 * mm});
            skCircle(sketch, "E8.28.18.0", {"center": v(-147.43, 202.33) * mm, "radius": 2.54 * mm});
            skCircle(sketch, "E8.28.19.0", {"center": v(-147.52, 189.63) * mm, "radius": 2.54 * mm});
            skCircle(sketch, "E8.28.20.0", {"center": v(-147.6, 176.93) * mm, "radius": 2.54 * mm});
            skCircle(sketch, "E8.28.21.0", {"center": v(-147.69, 164.23) * mm, "radius": 2.54 * mm});
            skCircle(sketch, "E8.28.22.0", {"center": v(-147.77, 151.53) * mm, "radius": 2.54 * mm});
            skCircle(sketch, "E8.28.23.0", {"center": v(-147.85, 138.83) * mm, "radius": 2.54 * mm});
            skCircle(sketch, "E8.28.24.0", {"center": v(-147.94, 126.13) * mm, "radius": 2.54 * mm});
            skCircle(sketch, "E8.28.25.0", {"center": v(-148.02, 113.43) * mm, "radius": 2.54 * mm});
            skCircle(sketch, "E8.28.26.0", {"center": v(-148.1, 100.73) * mm, "radius": 2.54 * mm});
            skCircle(sketch, "E8.28.27.0", {"center": v(-148.19, 88.03) * mm, "radius": 2.54 * mm});
            skCircle(sketch, "E8.28.28.0", {"center": v(-148.27, 75.33) * mm, "radius": 2.54 * mm});
            skCircle(sketch, "E8.28.29.0", {"center": v(-148.36, 62.63) * mm, "radius": 2.54 * mm});
            skCircle(sketch, "E8.28.30.0", {"center": v(-148.44, 49.93) * mm, "radius": 2.54 * mm});
            skCircle(sketch, "E8.28.31.0", {"center": v(-148.53, 37.23) * mm, "radius": 2.54 * mm});
            skCircle(sketch, "E8.28.32.0", {"center": v(-148.6, 24.53) * mm, "radius": 2.54 * mm});
            skCircle(sketch, "E8.29.0.0", {"center": v(-158.62, 430.89) * mm, "radius": 2.54 * mm});
            skCircle(sketch, "E8.29.1.0", {"center": v(-158.7, 418.19) * mm, "radius": 2.54 * mm});
            skCircle(sketch, "E8.29.2.0", {"center": v(-158.79, 405.49) * mm, "radius": 2.54 * mm});
            skCircle(sketch, "E8.29.3.0", {"center": v(-158.87, 392.8) * mm, "radius": 2.54 * mm});
            skCircle(sketch, "E8.29.4.0", {"center": v(-158.96, 380.1) * mm, "radius": 2.54 * mm});
            skCircle(sketch, "E8.29.5.0", {"center": v(-159.04, 367.4) * mm, "radius": 2.54 * mm});
            skCircle(sketch, "E8.29.6.0", {"center": v(-159.12, 354.7) * mm, "radius": 2.54 * mm});
            skCircle(sketch, "E8.29.7.0", {"center": v(-159.2, 342) * mm, "radius": 2.54 * mm});
            skCircle(sketch, "E8.29.8.0", {"center": v(-159.3, 329.3) * mm, "radius": 2.54 * mm});
            skCircle(sketch, "E8.29.9.0", {"center": v(-159.38, 316.6) * mm, "radius": 2.54 * mm});
            skCircle(sketch, "E8.29.10.0", {"center": v(-159.46, 303.9) * mm, "radius": 2.54 * mm});
            skCircle(sketch, "E8.29.11.0", {"center": v(-159.54, 291.2) * mm, "radius": 2.54 * mm});
            skCircle(sketch, "E8.29.12.0", {"center": v(-159.63, 278.5) * mm, "radius": 2.54 * mm});
            skCircle(sketch, "E8.29.13.0", {"center": v(-159.71, 265.8) * mm, "radius": 2.54 * mm});
            skCircle(sketch, "E8.29.14.0", {"center": v(-159.8, 253.1) * mm, "radius": 2.54 * mm});
            skCircle(sketch, "E8.29.15.0", {"center": v(-159.88, 240.4) * mm, "radius": 2.54 * mm});
            skCircle(sketch, "E8.29.16.0", {"center": v(-159.96, 227.7) * mm, "radius": 2.54 * mm});
            skCircle(sketch, "E8.29.17.0", {"center": v(-160.05, 215) * mm, "radius": 2.54 * mm});
            skCircle(sketch, "E8.29.18.0", {"center": v(-160.13, 202.3) * mm, "radius": 2.54 * mm});
            skCircle(sketch, "E8.29.19.0", {"center": v(-160.22, 189.6) * mm, "radius": 2.54 * mm});
            skCircle(sketch, "E8.29.20.0", {"center": v(-160.3, 176.9) * mm, "radius": 2.54 * mm});
            skCircle(sketch, "E8.29.21.0", {"center": v(-160.39, 164.2) * mm, "radius": 2.54 * mm});
            skCircle(sketch, "E8.29.22.0", {"center": v(-160.47, 151.5) * mm, "radius": 2.54 * mm});
            skCircle(sketch, "E8.29.23.0", {"center": v(-160.55, 138.8) * mm, "radius": 2.54 * mm});
            skCircle(sketch, "E8.29.24.0", {"center": v(-160.64, 126.1) * mm, "radius": 2.54 * mm});
            skCircle(sketch, "E8.29.25.0", {"center": v(-160.72, 113.4) * mm, "radius": 2.54 * mm});
            skCircle(sketch, "E8.29.26.0", {"center": v(-160.8, 100.7) * mm, "radius": 2.54 * mm});
            skCircle(sketch, "E8.29.27.0", {"center": v(-160.89, 88) * mm, "radius": 2.54 * mm});
            skCircle(sketch, "E8.29.28.0", {"center": v(-160.97, 75.3) * mm, "radius": 2.54 * mm});
            skCircle(sketch, "E8.29.29.0", {"center": v(-161.06, 62.6) * mm, "radius": 2.54 * mm});
            skCircle(sketch, "E8.29.30.0", {"center": v(-161.14, 49.9) * mm, "radius": 2.54 * mm});
            skCircle(sketch, "E8.29.31.0", {"center": v(-161.23, 37.2) * mm, "radius": 2.54 * mm});
            skCircle(sketch, "E8.29.32.0", {"center": v(-161.3, 24.5) * mm, "radius": 2.54 * mm});
            skCircle(sketch, "E8.30.0.0", {"center": v(-171.32, 430.86) * mm, "radius": 2.54 * mm});
            skCircle(sketch, "E8.30.1.0", {"center": v(-171.4, 418.16) * mm, "radius": 2.54 * mm});
            skCircle(sketch, "E8.30.2.0", {"center": v(-171.49, 405.46) * mm, "radius": 2.54 * mm});
            skCircle(sketch, "E8.30.3.0", {"center": v(-171.57, 392.76) * mm, "radius": 2.54 * mm});
            skCircle(sketch, "E8.30.4.0", {"center": v(-171.66, 380.06) * mm, "radius": 2.54 * mm});
            skCircle(sketch, "E8.30.5.0", {"center": v(-171.74, 367.36) * mm, "radius": 2.54 * mm});
            skCircle(sketch, "E8.30.6.0", {"center": v(-171.82, 354.66) * mm, "radius": 2.54 * mm});
            skCircle(sketch, "E8.30.7.0", {"center": v(-171.9, 341.96) * mm, "radius": 2.54 * mm});
            skCircle(sketch, "E8.30.8.0", {"center": v(-172, 329.26) * mm, "radius": 2.54 * mm});
            skCircle(sketch, "E8.30.9.0", {"center": v(-172.08, 316.56) * mm, "radius": 2.54 * mm});
            skCircle(sketch, "E8.30.10.0", {"center": v(-172.16, 303.86) * mm, "radius": 2.54 * mm});
            skCircle(sketch, "E8.30.11.0", {"center": v(-172.24, 291.16) * mm, "radius": 2.54 * mm});
            skCircle(sketch, "E8.30.12.0", {"center": v(-172.33, 278.46) * mm, "radius": 2.54 * mm});
            skCircle(sketch, "E8.30.13.0", {"center": v(-172.41, 265.76) * mm, "radius": 2.54 * mm});
            skCircle(sketch, "E8.30.14.0", {"center": v(-172.5, 253.06) * mm, "radius": 2.54 * mm});
            skCircle(sketch, "E8.30.15.0", {"center": v(-172.58, 240.36) * mm, "radius": 2.54 * mm});
            skCircle(sketch, "E8.30.16.0", {"center": v(-172.66, 227.66) * mm, "radius": 2.54 * mm});
            skCircle(sketch, "E8.30.17.0", {"center": v(-172.75, 214.96) * mm, "radius": 2.54 * mm});
            skCircle(sketch, "E8.30.18.0", {"center": v(-172.83, 202.26) * mm, "radius": 2.54 * mm});
            skCircle(sketch, "E8.30.19.0", {"center": v(-172.92, 189.56) * mm, "radius": 2.54 * mm});
            skCircle(sketch, "E8.30.20.0", {"center": v(-173, 176.86) * mm, "radius": 2.54 * mm});
            skCircle(sketch, "E8.30.21.0", {"center": v(-173.09, 164.16) * mm, "radius": 2.54 * mm});
            skCircle(sketch, "E8.30.22.0", {"center": v(-173.17, 151.46) * mm, "radius": 2.54 * mm});
            skCircle(sketch, "E8.30.23.0", {"center": v(-173.25, 138.76) * mm, "radius": 2.54 * mm});
            skCircle(sketch, "E8.30.24.0", {"center": v(-173.34, 126.06) * mm, "radius": 2.54 * mm});
            skCircle(sketch, "E8.30.25.0", {"center": v(-173.42, 113.36) * mm, "radius": 2.54 * mm});
            skCircle(sketch, "E8.30.26.0", {"center": v(-173.5, 100.67) * mm, "radius": 2.54 * mm});
            skCircle(sketch, "E8.30.27.0", {"center": v(-173.59, 87.97) * mm, "radius": 2.54 * mm});
            skCircle(sketch, "E8.30.28.0", {"center": v(-173.67, 75.27) * mm, "radius": 2.54 * mm});
            skCircle(sketch, "E8.30.29.0", {"center": v(-173.76, 62.57) * mm, "radius": 2.54 * mm});
            skCircle(sketch, "E8.30.30.0", {"center": v(-173.84, 49.87) * mm, "radius": 2.54 * mm});
            skCircle(sketch, "E8.30.31.0", {"center": v(-173.93, 37.17) * mm, "radius": 2.54 * mm});
            skCircle(sketch, "E8.30.32.0", {"center": v(-174, 24.47) * mm, "radius": 2.54 * mm});
            skCircle(sketch, "E8.31.0.0", {"center": v(-184.02, 430.83) * mm, "radius": 2.54 * mm});
            skCircle(sketch, "E8.31.1.0", {"center": v(-184.1, 418.13) * mm, "radius": 2.54 * mm});
            skCircle(sketch, "E8.31.2.0", {"center": v(-184.19, 405.43) * mm, "radius": 2.54 * mm});
            skCircle(sketch, "E8.31.3.0", {"center": v(-184.27, 392.73) * mm, "radius": 2.54 * mm});
            skCircle(sketch, "E8.31.4.0", {"center": v(-184.36, 380.03) * mm, "radius": 2.54 * mm});
            skCircle(sketch, "E8.31.5.0", {"center": v(-184.44, 367.33) * mm, "radius": 2.54 * mm});
            skCircle(sketch, "E8.31.6.0", {"center": v(-184.52, 354.63) * mm, "radius": 2.54 * mm});
            skCircle(sketch, "E8.31.7.0", {"center": v(-184.6, 341.93) * mm, "radius": 2.54 * mm});
            skCircle(sketch, "E8.31.8.0", {"center": v(-184.7, 329.23) * mm, "radius": 2.54 * mm});
            skCircle(sketch, "E8.31.9.0", {"center": v(-184.78, 316.53) * mm, "radius": 2.54 * mm});
            skCircle(sketch, "E8.31.10.0", {"center": v(-184.86, 303.83) * mm, "radius": 2.54 * mm});
            skCircle(sketch, "E8.31.11.0", {"center": v(-184.94, 291.13) * mm, "radius": 2.54 * mm});
            skCircle(sketch, "E8.31.12.0", {"center": v(-185.03, 278.43) * mm, "radius": 2.54 * mm});
            skCircle(sketch, "E8.31.13.0", {"center": v(-185.11, 265.73) * mm, "radius": 2.54 * mm});
            skCircle(sketch, "E8.31.14.0", {"center": v(-185.2, 253.03) * mm, "radius": 2.54 * mm});
            skCircle(sketch, "E8.31.15.0", {"center": v(-185.28, 240.33) * mm, "radius": 2.54 * mm});
            skCircle(sketch, "E8.31.16.0", {"center": v(-185.36, 227.63) * mm, "radius": 2.54 * mm});
            skCircle(sketch, "E8.31.17.0", {"center": v(-185.45, 214.93) * mm, "radius": 2.54 * mm});
            skCircle(sketch, "E8.31.18.0", {"center": v(-185.53, 202.23) * mm, "radius": 2.54 * mm});
            skCircle(sketch, "E8.31.19.0", {"center": v(-185.62, 189.53) * mm, "radius": 2.54 * mm});
            skCircle(sketch, "E8.31.20.0", {"center": v(-185.7, 176.83) * mm, "radius": 2.54 * mm});
            skCircle(sketch, "E8.31.21.0", {"center": v(-185.79, 164.13) * mm, "radius": 2.54 * mm});
            skCircle(sketch, "E8.31.22.0", {"center": v(-185.87, 151.43) * mm, "radius": 2.54 * mm});
            skCircle(sketch, "E8.31.23.0", {"center": v(-185.95, 138.73) * mm, "radius": 2.54 * mm});
            skCircle(sketch, "E8.31.24.0", {"center": v(-186.04, 126.03) * mm, "radius": 2.54 * mm});
            skCircle(sketch, "E8.31.25.0", {"center": v(-186.12, 113.33) * mm, "radius": 2.54 * mm});
            skCircle(sketch, "E8.31.26.0", {"center": v(-186.2, 100.63) * mm, "radius": 2.54 * mm});
            skCircle(sketch, "E8.31.27.0", {"center": v(-186.29, 87.93) * mm, "radius": 2.54 * mm});
            skCircle(sketch, "E8.31.28.0", {"center": v(-186.37, 75.23) * mm, "radius": 2.54 * mm});
            skCircle(sketch, "E8.31.29.0", {"center": v(-186.46, 62.53) * mm, "radius": 2.54 * mm});
            skCircle(sketch, "E8.31.30.0", {"center": v(-186.54, 49.83) * mm, "radius": 2.54 * mm});
            skCircle(sketch, "E8.31.31.0", {"center": v(-186.63, 37.14) * mm, "radius": 2.54 * mm});
            skCircle(sketch, "E8.31.32.0", {"center": v(-186.7, 24.44) * mm, "radius": 2.54 * mm});
            skCircle(sketch, "E8.32.0.0", {"center": v(-196.72, 430.8) * mm, "radius": 2.54 * mm});
            skCircle(sketch, "E8.32.1.0", {"center": v(-196.8, 418.1) * mm, "radius": 2.54 * mm});
            skCircle(sketch, "E8.32.2.0", {"center": v(-196.89, 405.4) * mm, "radius": 2.54 * mm});
            skCircle(sketch, "E8.32.3.0", {"center": v(-196.97, 392.7) * mm, "radius": 2.54 * mm});
            skCircle(sketch, "E8.32.4.0", {"center": v(-197.06, 380) * mm, "radius": 2.54 * mm});
            skCircle(sketch, "E8.32.5.0", {"center": v(-197.14, 367.3) * mm, "radius": 2.54 * mm});
            skCircle(sketch, "E8.32.6.0", {"center": v(-197.22, 354.6) * mm, "radius": 2.54 * mm});
            skCircle(sketch, "E8.32.7.0", {"center": v(-197.3, 341.9) * mm, "radius": 2.54 * mm});
            skCircle(sketch, "E8.32.8.0", {"center": v(-197.4, 329.2) * mm, "radius": 2.54 * mm});
            skCircle(sketch, "E8.32.9.0", {"center": v(-197.48, 316.5) * mm, "radius": 2.54 * mm});
            skCircle(sketch, "E8.32.10.0", {"center": v(-197.56, 303.8) * mm, "radius": 2.54 * mm});
            skCircle(sketch, "E8.32.11.0", {"center": v(-197.64, 291.1) * mm, "radius": 2.54 * mm});
            skCircle(sketch, "E8.32.12.0", {"center": v(-197.73, 278.4) * mm, "radius": 2.54 * mm});
            skCircle(sketch, "E8.32.13.0", {"center": v(-197.81, 265.7) * mm, "radius": 2.54 * mm});
            skCircle(sketch, "E8.32.14.0", {"center": v(-197.9, 253) * mm, "radius": 2.54 * mm});
            skCircle(sketch, "E8.32.15.0", {"center": v(-197.98, 240.3) * mm, "radius": 2.54 * mm});
            skCircle(sketch, "E8.32.16.0", {"center": v(-198.06, 227.6) * mm, "radius": 2.54 * mm});
            skCircle(sketch, "E8.32.17.0", {"center": v(-198.15, 214.9) * mm, "radius": 2.54 * mm});
            skCircle(sketch, "E8.32.18.0", {"center": v(-198.23, 202.2) * mm, "radius": 2.54 * mm});
            skCircle(sketch, "E8.32.19.0", {"center": v(-198.32, 189.5) * mm, "radius": 2.54 * mm});
            skCircle(sketch, "E8.32.20.0", {"center": v(-198.4, 176.8) * mm, "radius": 2.54 * mm});
            skCircle(sketch, "E8.32.21.0", {"center": v(-198.48, 164.1) * mm, "radius": 2.54 * mm});
            skCircle(sketch, "E8.32.22.0", {"center": v(-198.57, 151.4) * mm, "radius": 2.54 * mm});
            skCircle(sketch, "E8.32.23.0", {"center": v(-198.65, 138.7) * mm, "radius": 2.54 * mm});
            skCircle(sketch, "E8.32.24.0", {"center": v(-198.74, 126) * mm, "radius": 2.54 * mm});
            skCircle(sketch, "E8.32.25.0", {"center": v(-198.82, 113.3) * mm, "radius": 2.54 * mm});
            skCircle(sketch, "E8.32.26.0", {"center": v(-198.9, 100.6) * mm, "radius": 2.54 * mm});
            skCircle(sketch, "E8.32.27.0", {"center": v(-198.99, 87.9) * mm, "radius": 2.54 * mm});
            skCircle(sketch, "E8.32.28.0", {"center": v(-199.07, 75.2) * mm, "radius": 2.54 * mm});
            skCircle(sketch, "E8.32.29.0", {"center": v(-199.16, 62.5) * mm, "radius": 2.54 * mm});
            skCircle(sketch, "E8.32.30.0", {"center": v(-199.24, 49.8) * mm, "radius": 2.54 * mm});
            skCircle(sketch, "E8.32.31.0", {"center": v(-199.33, 37.1) * mm, "radius": 2.54 * mm});
            skCircle(sketch, "E8.32.32.0", {"center": v(-199.4, 24.4) * mm, "radius": 2.54 * mm});
            skLineSegment(sketch, "E8.direction1", {"start": v(209.68, 431.8) * mm, "end": v(196.98, 431.77) * mm, "construction": true});
            skLineSegment(sketch, "E8.direction2", {"start": v(209.68, 431.8) * mm, "end": v(209.6, 419.1) * mm, "construction": true});
            skCircle(sketch, "E9.0.33.0", {"center": v(-209.42, 430.76) * mm, "radius": 2.54 * mm});
            skCircle(sketch, "E9.0.33.1", {"center": v(-209.5, 418.06) * mm, "radius": 2.54 * mm});
            skCircle(sketch, "E9.0.33.2", {"center": v(-209.59, 405.36) * mm, "radius": 2.54 * mm});
            skCircle(sketch, "E9.0.33.3", {"center": v(-209.67, 392.66) * mm, "radius": 2.54 * mm});
            skCircle(sketch, "E9.0.33.4", {"center": v(-209.76, 379.96) * mm, "radius": 2.54 * mm});
            skCircle(sketch, "E9.0.33.5", {"center": v(-209.84, 367.27) * mm, "radius": 2.54 * mm});
            skCircle(sketch, "E9.0.33.6", {"center": v(-209.92, 354.57) * mm, "radius": 2.54 * mm});
            skCircle(sketch, "E9.0.33.7", {"center": v(-210, 341.87) * mm, "radius": 2.54 * mm});
            skCircle(sketch, "E9.0.33.8", {"center": v(-210.1, 329.17) * mm, "radius": 2.54 * mm});
            skCircle(sketch, "E9.0.33.9", {"center": v(-210.18, 316.47) * mm, "radius": 2.54 * mm});
            skCircle(sketch, "E9.0.33.10", {"center": v(-210.26, 303.77) * mm, "radius": 2.54 * mm});
            skCircle(sketch, "E9.0.33.11", {"center": v(-210.34, 291.07) * mm, "radius": 2.54 * mm});
            skCircle(sketch, "E9.0.33.12", {"center": v(-210.43, 278.37) * mm, "radius": 2.54 * mm});
            skCircle(sketch, "E9.0.33.13", {"center": v(-210.51, 265.67) * mm, "radius": 2.54 * mm});
            skCircle(sketch, "E9.0.33.14", {"center": v(-210.6, 252.97) * mm, "radius": 2.54 * mm});
            skCircle(sketch, "E9.0.33.15", {"center": v(-210.68, 240.27) * mm, "radius": 2.54 * mm});
            skCircle(sketch, "E9.0.33.16", {"center": v(-210.76, 227.57) * mm, "radius": 2.54 * mm});
            skCircle(sketch, "E9.0.33.17", {"center": v(-210.85, 214.87) * mm, "radius": 2.54 * mm});
            skCircle(sketch, "E9.0.33.18", {"center": v(-210.93, 202.17) * mm, "radius": 2.54 * mm});
            skCircle(sketch, "E9.0.33.19", {"center": v(-211.02, 189.47) * mm, "radius": 2.54 * mm});
            skCircle(sketch, "E9.0.33.20", {"center": v(-211.1, 176.77) * mm, "radius": 2.54 * mm});
            skCircle(sketch, "E9.0.33.21", {"center": v(-211.18, 164.07) * mm, "radius": 2.54 * mm});
            skCircle(sketch, "E9.0.33.22", {"center": v(-211.27, 151.37) * mm, "radius": 2.54 * mm});
            skCircle(sketch, "E9.0.33.23", {"center": v(-211.35, 138.67) * mm, "radius": 2.54 * mm});
            skCircle(sketch, "E9.0.33.24", {"center": v(-211.44, 125.97) * mm, "radius": 2.54 * mm});
            skCircle(sketch, "E9.0.33.25", {"center": v(-211.52, 113.27) * mm, "radius": 2.54 * mm});
            skCircle(sketch, "E9.0.33.26", {"center": v(-211.6, 100.57) * mm, "radius": 2.54 * mm});
            skCircle(sketch, "E9.0.33.27", {"center": v(-211.69, 87.87) * mm, "radius": 2.54 * mm});
            skCircle(sketch, "E9.0.33.28", {"center": v(-211.77, 75.17) * mm, "radius": 2.54 * mm});
            skCircle(sketch, "E9.0.33.29", {"center": v(-211.86, 62.47) * mm, "radius": 2.54 * mm});
            skCircle(sketch, "E9.0.33.30", {"center": v(-211.94, 49.77) * mm, "radius": 2.54 * mm});
            skCircle(sketch, "E9.0.33.31", {"center": v(-212.03, 37.07) * mm, "radius": 2.54 * mm});
            skCircle(sketch, "E9.0.33.32", {"center": v(-212.1, 24.37) * mm, "radius": 2.54 * mm});
            skCircle(sketch, "E10.0.0.33", {"center": v(206.9, 12.7) * mm, "radius": 2.54 * mm});
            skCircle(sketch, "E10.0.1.33", {"center": v(194.2, 12.68) * mm, "radius": 2.54 * mm});
            skCircle(sketch, "E10.0.2.33", {"center": v(181.5, 12.65) * mm, "radius": 2.54 * mm});
            skCircle(sketch, "E10.0.3.33", {"center": v(168.8, 12.61) * mm, "radius": 2.54 * mm});
            skCircle(sketch, "E10.0.4.33", {"center": v(156.1, 12.58) * mm, "radius": 2.54 * mm});
            skCircle(sketch, "E10.0.5.33", {"center": v(143.4, 12.55) * mm, "radius": 2.54 * mm});
            skCircle(sketch, "E10.0.6.33", {"center": v(130.7, 12.52) * mm, "radius": 2.54 * mm});
            skCircle(sketch, "E10.0.7.33", {"center": v(118, 12.49) * mm, "radius": 2.54 * mm});
            skCircle(sketch, "E10.0.8.33", {"center": v(105.3, 12.46) * mm, "radius": 2.54 * mm});
            skCircle(sketch, "E10.0.9.33", {"center": v(92.6, 12.43) * mm, "radius": 2.54 * mm});
            skCircle(sketch, "E10.0.10.33", {"center": v(79.9, 12.4) * mm, "radius": 2.54 * mm});
            skCircle(sketch, "E10.0.11.33", {"center": v(67.2, 12.36) * mm, "radius": 2.54 * mm});
            skCircle(sketch, "E10.0.12.33", {"center": v(54.5, 12.33) * mm, "radius": 2.54 * mm});
            skCircle(sketch, "E10.0.13.33", {"center": v(41.8, 12.3) * mm, "radius": 2.54 * mm});
            skCircle(sketch, "E10.0.14.33", {"center": v(29.1, 12.27) * mm, "radius": 2.54 * mm});
            skCircle(sketch, "E10.0.15.33", {"center": v(16.4, 12.24) * mm, "radius": 2.54 * mm});
            skCircle(sketch, "E10.0.16.33", {"center": v(3.7, 12.2) * mm, "radius": 2.54 * mm});
            skCircle(sketch, "E10.0.17.33", {"center": v(-9, 12.18) * mm, "radius": 2.54 * mm});
            skCircle(sketch, "E10.0.18.33", {"center": v(-21.7, 12.14) * mm, "radius": 2.54 * mm});
            skCircle(sketch, "E10.0.19.33", {"center": v(-34.4, 12.11) * mm, "radius": 2.54 * mm});
            skCircle(sketch, "E10.0.20.33", {"center": v(-47.1, 12.08) * mm, "radius": 2.54 * mm});
            skCircle(sketch, "E10.0.21.33", {"center": v(-59.8, 12.05) * mm, "radius": 2.54 * mm});
            skCircle(sketch, "E10.0.22.33", {"center": v(-72.5, 12.02) * mm, "radius": 2.54 * mm});
            skCircle(sketch, "E10.0.23.33", {"center": v(-85.2, 11.99) * mm, "radius": 2.54 * mm});
            skCircle(sketch, "E10.0.24.33", {"center": v(-97.9, 11.96) * mm, "radius": 2.54 * mm});
            skCircle(sketch, "E10.0.25.33", {"center": v(-110.6, 11.92) * mm, "radius": 2.54 * mm});
            skCircle(sketch, "E10.0.26.33", {"center": v(-123.3, 11.9) * mm, "radius": 2.54 * mm});
            skCircle(sketch, "E10.0.27.33", {"center": v(-136, 11.86) * mm, "radius": 2.54 * mm});
            skCircle(sketch, "E10.0.28.33", {"center": v(-148.7, 11.83) * mm, "radius": 2.54 * mm});
            skCircle(sketch, "E10.0.29.33", {"center": v(-161.4, 11.8) * mm, "radius": 2.54 * mm});
            skCircle(sketch, "E10.0.30.33", {"center": v(-174.1, 11.77) * mm, "radius": 2.54 * mm});
            skCircle(sketch, "E10.0.31.33", {"center": v(-186.8, 11.74) * mm, "radius": 2.54 * mm});
            skCircle(sketch, "E10.0.32.33", {"center": v(-199.5, 11.7) * mm, "radius": 2.54 * mm});
            skCircle(sketch, "E10.0.33.33", {"center": v(-212.2, 11.67) * mm, "radius": 2.54 * mm});
            skSolve(sketch);
        }
        {
            var Q0;
            Q0 = qSketchRegion(id + "F2", true);
            extrude(context, id + "F3", {"entities" : qUnion([Q0]), "operationType" : NewBodyOperationType.REMOVE, "endBound" : BoundingType.THROUGH_ALL, "oppositeDirection" : true, "depth" : 25.4 * mm, "offsetDistance" : 25.4 * mm});
        }
        {
            var Q0;
            Q0=makeQuery(id+"F1.opExtrude","CAP_FACE",FACE,{"disambiguationData":[OSD([sQuery(id+"F0.wireOp",EDGE,"E0"),sQuery(id+"F0.wireOp",EDGE,"E1"),sQuery(id+"F0.wireOp",EDGE,"E2"),sQuery(id+"F0.wireOp",EDGE,"E3"),sQuery(id+"F0.wireOp",EDGE,"E4"),sQuery(id+"F0.wireOp",EDGE,"E5"),sQuery(id+"F0.wireOp",EDGE,"E6.0"),sQuery(id+"F0.wireOp",EDGE,"E6.1"),sQuery(id+"F0.wireOp",EDGE,"E6.2"),sQuery(id+"F0.wireOp",EDGE,"E6.3"),sQuery(id+"F0.wireOp",EDGE,"E6.4"),sQuery(id+"F0.wireOp",EDGE,"E6.5")])],"isStart":true});
            var sketch = newSketch(context, id + "F4", { "sketchPlane" : qUnion([Q0])});
            skLineSegment(sketch, "E11.bottom", {"start": v(-215.9, 31.75) * mm, "end": v(215.9, 31.75) * mm});
            skLineSegment(sketch, "E11.top", {"start": v(-215.9, -31.75) * mm, "end": v(215.9, -31.75) * mm});
            skLineSegment(sketch, "E11.left", {"start": v(-215.9, 31.75) * mm, "end": v(-215.9, -31.75) * mm});
            skLineSegment(sketch, "E11.right", {"start": v(215.9, 31.75) * mm, "end": v(215.9, -31.75) * mm});
            skSolve(sketch);
        }
        {
            var Q0;
            Q0 = qSketchRegion(id + "F4", true);
            extrude(context, id + "F5", {"entities" : qUnion([Q0]), "operationType" : NewBodyOperationType.ADD, "oppositeDirection" : true, "depth" : 5.08 * mm, "offsetDistance" : 25.4 * mm});
        }
        {
            var Q0;
            Q0=makeQuery(id+"F5.boolean.opBoolean","MERGE",FACE,{"derivedFrom":[makeQuery(id+"F1.opExtrude","CAP_FACE",FACE,{"disambiguationData":[OSD([sQuery(id+"F0.wireOp",EDGE,"E0"),sQuery(id+"F0.wireOp",EDGE,"E1"),sQuery(id+"F0.wireOp",EDGE,"E2"),sQuery(id+"F0.wireOp",EDGE,"E3"),sQuery(id+"F0.wireOp",EDGE,"E4"),sQuery(id+"F0.wireOp",EDGE,"E5"),sQuery(id+"F0.wireOp",EDGE,"E6.0"),sQuery(id+"F0.wireOp",EDGE,"E6.1"),sQuery(id+"F0.wireOp",EDGE,"E6.2"),sQuery(id+"F0.wireOp",EDGE,"E6.3"),sQuery(id+"F0.wireOp",EDGE,"E6.4"),sQuery(id+"F0.wireOp",EDGE,"E6.5")])],"isStart":true}),makeQuery(id+"F5.opExtrude","CAP_FACE",FACE,{"disambiguationData":[OSD([sQuery(id+"F4.wireOp",EDGE,"E11.bottom"),sQuery(id+"F4.wireOp",EDGE,"E11.top"),sQuery(id+"F4.wireOp",EDGE,"E11.left"),sQuery(id+"F4.wireOp",EDGE,"E11.right")])],"isStart":true})]});
            var sketch = newSketch(context, id + "F6", { "sketchPlane" : qUnion([Q0])});
            skCircle(sketch, "E12", {"center": v(-210.7, 26.8) * mm, "radius": 2.54 * mm});
            skCircle(sketch, "E13.0.1.0", {"center": v(-210.9, 14.1) * mm, "radius": 2.54 * mm});
            skCircle(sketch, "E13.0.2.0", {"center": v(-211.12, 1.4) * mm, "radius": 2.54 * mm});
            skCircle(sketch, "E13.0.3.0", {"center": v(-211.33, -11.3) * mm, "radius": 2.54 * mm});
            skCircle(sketch, "E13.0.4.0", {"center": v(-211.54, -24) * mm, "radius": 2.54 * mm});
            skLineSegment(sketch, "E13.direction1", {"start": v(-210.7, 26.8) * mm, "end": v(-198, 26.8) * mm, "construction": true});
            skLineSegment(sketch, "E13.direction2", {"start": v(-210.7, 26.8) * mm, "end": v(-210.9, 14.1) * mm, "construction": true});
            skCircle(sketch, "E14.0.1.0", {"center": v(-198, 26.8) * mm, "radius": 2.54 * mm});
            skCircle(sketch, "E14.0.1.1", {"center": v(-198.2, 14.1) * mm, "radius": 2.54 * mm});
            skCircle(sketch, "E14.0.1.2", {"center": v(-198.42, 1.4) * mm, "radius": 2.54 * mm});
            skCircle(sketch, "E14.0.1.3", {"center": v(-198.63, -11.3) * mm, "radius": 2.54 * mm});
            skCircle(sketch, "E14.0.1.4", {"center": v(-198.84, -24) * mm, "radius": 2.54 * mm});
            skCircle(sketch, "E14.0.2.0", {"center": v(-185.3, 26.8) * mm, "radius": 2.54 * mm});
            skCircle(sketch, "E14.0.2.1", {"center": v(-185.5, 14.1) * mm, "radius": 2.54 * mm});
            skCircle(sketch, "E14.0.2.2", {"center": v(-185.72, 1.4) * mm, "radius": 2.54 * mm});
            skCircle(sketch, "E14.0.2.3", {"center": v(-185.93, -11.3) * mm, "radius": 2.54 * mm});
            skCircle(sketch, "E14.0.2.4", {"center": v(-186.14, -24) * mm, "radius": 2.54 * mm});
            skCircle(sketch, "E14.0.3.0", {"center": v(-172.6, 26.8) * mm, "radius": 2.54 * mm});
            skCircle(sketch, "E14.0.3.1", {"center": v(-172.8, 14.1) * mm, "radius": 2.54 * mm});
            skCircle(sketch, "E14.0.3.2", {"center": v(-173.02, 1.4) * mm, "radius": 2.54 * mm});
            skCircle(sketch, "E14.0.3.3", {"center": v(-173.23, -11.3) * mm, "radius": 2.54 * mm});
            skCircle(sketch, "E14.0.3.4", {"center": v(-173.44, -24) * mm, "radius": 2.54 * mm});
            skCircle(sketch, "E14.0.4.0", {"center": v(-159.9, 26.8) * mm, "radius": 2.54 * mm});
            skCircle(sketch, "E14.0.4.1", {"center": v(-160.1, 14.1) * mm, "radius": 2.54 * mm});
            skCircle(sketch, "E14.0.4.2", {"center": v(-160.32, 1.4) * mm, "radius": 2.54 * mm});
            skCircle(sketch, "E14.0.4.3", {"center": v(-160.53, -11.3) * mm, "radius": 2.54 * mm});
            skCircle(sketch, "E14.0.4.4", {"center": v(-160.74, -24) * mm, "radius": 2.54 * mm});
            skCircle(sketch, "E14.0.5.0", {"center": v(-147.2, 26.8) * mm, "radius": 2.54 * mm});
            skCircle(sketch, "E14.0.5.1", {"center": v(-147.4, 14.1) * mm, "radius": 2.54 * mm});
            skCircle(sketch, "E14.0.5.2", {"center": v(-147.62, 1.4) * mm, "radius": 2.54 * mm});
            skCircle(sketch, "E14.0.5.3", {"center": v(-147.83, -11.3) * mm, "radius": 2.54 * mm});
            skCircle(sketch, "E14.0.5.4", {"center": v(-148.04, -24) * mm, "radius": 2.54 * mm});
            skCircle(sketch, "E14.0.6.0", {"center": v(-134.5, 26.8) * mm, "radius": 2.54 * mm});
            skCircle(sketch, "E14.0.6.1", {"center": v(-134.7, 14.1) * mm, "radius": 2.54 * mm});
            skCircle(sketch, "E14.0.6.2", {"center": v(-134.92, 1.4) * mm, "radius": 2.54 * mm});
            skCircle(sketch, "E14.0.6.3", {"center": v(-135.13, -11.3) * mm, "radius": 2.54 * mm});
            skCircle(sketch, "E14.0.6.4", {"center": v(-135.34, -24) * mm, "radius": 2.54 * mm});
            skCircle(sketch, "E14.0.7.0", {"center": v(-121.8, 26.8) * mm, "radius": 2.54 * mm});
            skCircle(sketch, "E14.0.7.1", {"center": v(-122, 14.1) * mm, "radius": 2.54 * mm});
            skCircle(sketch, "E14.0.7.2", {"center": v(-122.22, 1.4) * mm, "radius": 2.54 * mm});
            skCircle(sketch, "E14.0.7.3", {"center": v(-122.43, -11.3) * mm, "radius": 2.54 * mm});
            skCircle(sketch, "E14.0.7.4", {"center": v(-122.64, -24) * mm, "radius": 2.54 * mm});
            skCircle(sketch, "E14.0.8.0", {"center": v(-109.1, 26.8) * mm, "radius": 2.54 * mm});
            skCircle(sketch, "E14.0.8.1", {"center": v(-109.3, 14.1) * mm, "radius": 2.54 * mm});
            skCircle(sketch, "E14.0.8.2", {"center": v(-109.52, 1.4) * mm, "radius": 2.54 * mm});
            skCircle(sketch, "E14.0.8.3", {"center": v(-109.73, -11.3) * mm, "radius": 2.54 * mm});
            skCircle(sketch, "E14.0.8.4", {"center": v(-109.94, -24) * mm, "radius": 2.54 * mm});
            skCircle(sketch, "E14.0.9.0", {"center": v(-96.4, 26.8) * mm, "radius": 2.54 * mm});
            skCircle(sketch, "E14.0.9.1", {"center": v(-96.6, 14.1) * mm, "radius": 2.54 * mm});
            skCircle(sketch, "E14.0.9.2", {"center": v(-96.82, 1.4) * mm, "radius": 2.54 * mm});
            skCircle(sketch, "E14.0.9.3", {"center": v(-97.03, -11.3) * mm, "radius": 2.54 * mm});
            skCircle(sketch, "E14.0.9.4", {"center": v(-97.24, -24) * mm, "radius": 2.54 * mm});
            skCircle(sketch, "E14.0.10.0", {"center": v(-83.7, 26.8) * mm, "radius": 2.54 * mm});
            skCircle(sketch, "E14.0.10.1", {"center": v(-83.9, 14.1) * mm, "radius": 2.54 * mm});
            skCircle(sketch, "E14.0.10.2", {"center": v(-84.12, 1.4) * mm, "radius": 2.54 * mm});
            skCircle(sketch, "E14.0.10.3", {"center": v(-84.33, -11.3) * mm, "radius": 2.54 * mm});
            skCircle(sketch, "E14.0.10.4", {"center": v(-84.54, -24) * mm, "radius": 2.54 * mm});
            skCircle(sketch, "E14.0.11.0", {"center": v(-71, 26.8) * mm, "radius": 2.54 * mm});
            skCircle(sketch, "E14.0.11.1", {"center": v(-71.2, 14.1) * mm, "radius": 2.54 * mm});
            skCircle(sketch, "E14.0.11.2", {"center": v(-71.42, 1.4) * mm, "radius": 2.54 * mm});
            skCircle(sketch, "E14.0.11.3", {"center": v(-71.63, -11.3) * mm, "radius": 2.54 * mm});
            skCircle(sketch, "E14.0.11.4", {"center": v(-71.84, -24) * mm, "radius": 2.54 * mm});
            skCircle(sketch, "E14.0.12.0", {"center": v(-58.3, 26.8) * mm, "radius": 2.54 * mm});
            skCircle(sketch, "E14.0.12.1", {"center": v(-58.5, 14.1) * mm, "radius": 2.54 * mm});
            skCircle(sketch, "E14.0.12.2", {"center": v(-58.72, 1.4) * mm, "radius": 2.54 * mm});
            skCircle(sketch, "E14.0.12.3", {"center": v(-58.93, -11.3) * mm, "radius": 2.54 * mm});
            skCircle(sketch, "E14.0.12.4", {"center": v(-59.14, -24) * mm, "radius": 2.54 * mm});
            skCircle(sketch, "E14.0.13.0", {"center": v(-45.6, 26.8) * mm, "radius": 2.54 * mm});
            skCircle(sketch, "E14.0.13.1", {"center": v(-45.8, 14.1) * mm, "radius": 2.54 * mm});
            skCircle(sketch, "E14.0.13.2", {"center": v(-46.02, 1.4) * mm, "radius": 2.54 * mm});
            skCircle(sketch, "E14.0.13.3", {"center": v(-46.23, -11.3) * mm, "radius": 2.54 * mm});
            skCircle(sketch, "E14.0.13.4", {"center": v(-46.44, -24) * mm, "radius": 2.54 * mm});
            skCircle(sketch, "E14.0.14.0", {"center": v(-32.9, 26.8) * mm, "radius": 2.54 * mm});
            skCircle(sketch, "E14.0.14.1", {"center": v(-33.1, 14.1) * mm, "radius": 2.54 * mm});
            skCircle(sketch, "E14.0.14.2", {"center": v(-33.32, 1.4) * mm, "radius": 2.54 * mm});
            skCircle(sketch, "E14.0.14.3", {"center": v(-33.53, -11.3) * mm, "radius": 2.54 * mm});
            skCircle(sketch, "E14.0.14.4", {"center": v(-33.74, -24) * mm, "radius": 2.54 * mm});
            skCircle(sketch, "E14.0.15.0", {"center": v(-20.2, 26.8) * mm, "radius": 2.54 * mm});
            skCircle(sketch, "E14.0.15.1", {"center": v(-20.4, 14.1) * mm, "radius": 2.54 * mm});
            skCircle(sketch, "E14.0.15.2", {"center": v(-20.62, 1.4) * mm, "radius": 2.54 * mm});
            skCircle(sketch, "E14.0.15.3", {"center": v(-20.83, -11.3) * mm, "radius": 2.54 * mm});
            skCircle(sketch, "E14.0.15.4", {"center": v(-21.04, -24) * mm, "radius": 2.54 * mm});
            skCircle(sketch, "E14.0.16.0", {"center": v(-7.5, 26.8) * mm, "radius": 2.54 * mm});
            skCircle(sketch, "E14.0.16.1", {"center": v(-7.7, 14.1) * mm, "radius": 2.54 * mm});
            skCircle(sketch, "E14.0.16.2", {"center": v(-7.92, 1.4) * mm, "radius": 2.54 * mm});
            skCircle(sketch, "E14.0.16.3", {"center": v(-8.13, -11.3) * mm, "radius": 2.54 * mm});
            skCircle(sketch, "E14.0.16.4", {"center": v(-8.34, -24) * mm, "radius": 2.54 * mm});
            skCircle(sketch, "E14.0.17.0", {"center": v(5.2, 26.8) * mm, "radius": 2.54 * mm});
            skCircle(sketch, "E14.0.17.1", {"center": v(5, 14.1) * mm, "radius": 2.54 * mm});
            skCircle(sketch, "E14.0.17.2", {"center": v(4.78, 1.4) * mm, "radius": 2.54 * mm});
            skCircle(sketch, "E14.0.17.3", {"center": v(4.57, -11.3) * mm, "radius": 2.54 * mm});
            skCircle(sketch, "E14.0.17.4", {"center": v(4.36, -24) * mm, "radius": 2.54 * mm});
            skCircle(sketch, "E14.0.18.0", {"center": v(17.9, 26.8) * mm, "radius": 2.54 * mm});
            skCircle(sketch, "E14.0.18.1", {"center": v(17.7, 14.1) * mm, "radius": 2.54 * mm});
            skCircle(sketch, "E14.0.18.2", {"center": v(17.48, 1.4) * mm, "radius": 2.54 * mm});
            skCircle(sketch, "E14.0.18.3", {"center": v(17.27, -11.3) * mm, "radius": 2.54 * mm});
            skCircle(sketch, "E14.0.18.4", {"center": v(17.06, -24) * mm, "radius": 2.54 * mm});
            skCircle(sketch, "E14.0.19.0", {"center": v(30.6, 26.8) * mm, "radius": 2.54 * mm});
            skCircle(sketch, "E14.0.19.1", {"center": v(30.4, 14.1) * mm, "radius": 2.54 * mm});
            skCircle(sketch, "E14.0.19.2", {"center": v(30.18, 1.4) * mm, "radius": 2.54 * mm});
            skCircle(sketch, "E14.0.19.3", {"center": v(29.97, -11.3) * mm, "radius": 2.54 * mm});
            skCircle(sketch, "E14.0.19.4", {"center": v(29.76, -24) * mm, "radius": 2.54 * mm});
            skCircle(sketch, "E14.0.20.0", {"center": v(43.3, 26.8) * mm, "radius": 2.54 * mm});
            skCircle(sketch, "E14.0.20.1", {"center": v(43.1, 14.1) * mm, "radius": 2.54 * mm});
            skCircle(sketch, "E14.0.20.2", {"center": v(42.88, 1.4) * mm, "radius": 2.54 * mm});
            skCircle(sketch, "E14.0.20.3", {"center": v(42.67, -11.3) * mm, "radius": 2.54 * mm});
            skCircle(sketch, "E14.0.20.4", {"center": v(42.46, -24) * mm, "radius": 2.54 * mm});
            skCircle(sketch, "E14.0.21.0", {"center": v(56, 26.8) * mm, "radius": 2.54 * mm});
            skCircle(sketch, "E14.0.21.1", {"center": v(55.8, 14.1) * mm, "radius": 2.54 * mm});
            skCircle(sketch, "E14.0.21.2", {"center": v(55.58, 1.4) * mm, "radius": 2.54 * mm});
            skCircle(sketch, "E14.0.21.3", {"center": v(55.37, -11.3) * mm, "radius": 2.54 * mm});
            skCircle(sketch, "E14.0.21.4", {"center": v(55.16, -24) * mm, "radius": 2.54 * mm});
            skCircle(sketch, "E14.0.22.0", {"center": v(68.7, 26.8) * mm, "radius": 2.54 * mm});
            skCircle(sketch, "E14.0.22.1", {"center": v(68.5, 14.1) * mm, "radius": 2.54 * mm});
            skCircle(sketch, "E14.0.22.2", {"center": v(68.28, 1.4) * mm, "radius": 2.54 * mm});
            skCircle(sketch, "E14.0.22.3", {"center": v(68.07, -11.3) * mm, "radius": 2.54 * mm});
            skCircle(sketch, "E14.0.22.4", {"center": v(67.86, -24) * mm, "radius": 2.54 * mm});
            skCircle(sketch, "E14.0.23.0", {"center": v(81.4, 26.8) * mm, "radius": 2.54 * mm});
            skCircle(sketch, "E14.0.23.1", {"center": v(81.2, 14.1) * mm, "radius": 2.54 * mm});
            skCircle(sketch, "E14.0.23.2", {"center": v(80.98, 1.4) * mm, "radius": 2.54 * mm});
            skCircle(sketch, "E14.0.23.3", {"center": v(80.77, -11.3) * mm, "radius": 2.54 * mm});
            skCircle(sketch, "E14.0.23.4", {"center": v(80.56, -24) * mm, "radius": 2.54 * mm});
            skCircle(sketch, "E14.0.24.0", {"center": v(94.1, 26.8) * mm, "radius": 2.54 * mm});
            skCircle(sketch, "E14.0.24.1", {"center": v(93.9, 14.1) * mm, "radius": 2.54 * mm});
            skCircle(sketch, "E14.0.24.2", {"center": v(93.68, 1.4) * mm, "radius": 2.54 * mm});
            skCircle(sketch, "E14.0.24.3", {"center": v(93.47, -11.3) * mm, "radius": 2.54 * mm});
            skCircle(sketch, "E14.0.24.4", {"center": v(93.26, -24) * mm, "radius": 2.54 * mm});
            skCircle(sketch, "E14.0.25.0", {"center": v(106.8, 26.8) * mm, "radius": 2.54 * mm});
            skCircle(sketch, "E14.0.25.1", {"center": v(106.6, 14.1) * mm, "radius": 2.54 * mm});
            skCircle(sketch, "E14.0.25.2", {"center": v(106.38, 1.4) * mm, "radius": 2.54 * mm});
            skCircle(sketch, "E14.0.25.3", {"center": v(106.17, -11.3) * mm, "radius": 2.54 * mm});
            skCircle(sketch, "E14.0.25.4", {"center": v(105.96, -24) * mm, "radius": 2.54 * mm});
            skCircle(sketch, "E14.0.26.0", {"center": v(119.5, 26.8) * mm, "radius": 2.54 * mm});
            skCircle(sketch, "E14.0.26.1", {"center": v(119.3, 14.1) * mm, "radius": 2.54 * mm});
            skCircle(sketch, "E14.0.26.2", {"center": v(119.08, 1.4) * mm, "radius": 2.54 * mm});
            skCircle(sketch, "E14.0.26.3", {"center": v(118.87, -11.3) * mm, "radius": 2.54 * mm});
            skCircle(sketch, "E14.0.26.4", {"center": v(118.66, -24) * mm, "radius": 2.54 * mm});
            skCircle(sketch, "E14.0.27.0", {"center": v(132.2, 26.8) * mm, "radius": 2.54 * mm});
            skCircle(sketch, "E14.0.27.1", {"center": v(132, 14.1) * mm, "radius": 2.54 * mm});
            skCircle(sketch, "E14.0.27.2", {"center": v(131.78, 1.4) * mm, "radius": 2.54 * mm});
            skCircle(sketch, "E14.0.27.3", {"center": v(131.57, -11.3) * mm, "radius": 2.54 * mm});
            skCircle(sketch, "E14.0.27.4", {"center": v(131.36, -24) * mm, "radius": 2.54 * mm});
            skCircle(sketch, "E14.0.28.0", {"center": v(144.9, 26.8) * mm, "radius": 2.54 * mm});
            skCircle(sketch, "E14.0.28.1", {"center": v(144.7, 14.1) * mm, "radius": 2.54 * mm});
            skCircle(sketch, "E14.0.28.2", {"center": v(144.48, 1.4) * mm, "radius": 2.54 * mm});
            skCircle(sketch, "E14.0.28.3", {"center": v(144.27, -11.3) * mm, "radius": 2.54 * mm});
            skCircle(sketch, "E14.0.28.4", {"center": v(144.06, -24) * mm, "radius": 2.54 * mm});
            skCircle(sketch, "E14.0.29.0", {"center": v(157.6, 26.8) * mm, "radius": 2.54 * mm});
            skCircle(sketch, "E14.0.29.1", {"center": v(157.4, 14.1) * mm, "radius": 2.54 * mm});
            skCircle(sketch, "E14.0.29.2", {"center": v(157.18, 1.4) * mm, "radius": 2.54 * mm});
            skCircle(sketch, "E14.0.29.3", {"center": v(156.97, -11.3) * mm, "radius": 2.54 * mm});
            skCircle(sketch, "E14.0.29.4", {"center": v(156.76, -24) * mm, "radius": 2.54 * mm});
            skCircle(sketch, "E14.0.30.0", {"center": v(170.3, 26.8) * mm, "radius": 2.54 * mm});
            skCircle(sketch, "E14.0.30.1", {"center": v(170.1, 14.1) * mm, "radius": 2.54 * mm});
            skCircle(sketch, "E14.0.30.2", {"center": v(169.88, 1.4) * mm, "radius": 2.54 * mm});
            skCircle(sketch, "E14.0.30.3", {"center": v(169.67, -11.3) * mm, "radius": 2.54 * mm});
            skCircle(sketch, "E14.0.30.4", {"center": v(169.46, -24) * mm, "radius": 2.54 * mm});
            skCircle(sketch, "E14.0.31.0", {"center": v(183, 26.8) * mm, "radius": 2.54 * mm});
            skCircle(sketch, "E14.0.31.1", {"center": v(182.8, 14.1) * mm, "radius": 2.54 * mm});
            skCircle(sketch, "E14.0.31.2", {"center": v(182.58, 1.4) * mm, "radius": 2.54 * mm});
            skCircle(sketch, "E14.0.31.3", {"center": v(182.37, -11.3) * mm, "radius": 2.54 * mm});
            skCircle(sketch, "E14.0.31.4", {"center": v(182.16, -24) * mm, "radius": 2.54 * mm});
            skCircle(sketch, "E14.0.32.0", {"center": v(195.7, 26.8) * mm, "radius": 2.54 * mm});
            skCircle(sketch, "E14.0.32.1", {"center": v(195.5, 14.1) * mm, "radius": 2.54 * mm});
            skCircle(sketch, "E14.0.32.2", {"center": v(195.28, 1.4) * mm, "radius": 2.54 * mm});
            skCircle(sketch, "E14.0.32.3", {"center": v(195.07, -11.3) * mm, "radius": 2.54 * mm});
            skCircle(sketch, "E14.0.32.4", {"center": v(194.86, -24) * mm, "radius": 2.54 * mm});
            skCircle(sketch, "E15.0.33.0", {"center": v(208.4, 26.8) * mm, "radius": 2.54 * mm});
            skCircle(sketch, "E15.0.33.1", {"center": v(208.2, 14.1) * mm, "radius": 2.54 * mm});
            skCircle(sketch, "E15.0.33.2", {"center": v(207.98, 1.4) * mm, "radius": 2.54 * mm});
            skCircle(sketch, "E15.0.33.3", {"center": v(207.77, -11.3) * mm, "radius": 2.54 * mm});
            skCircle(sketch, "E15.0.33.4", {"center": v(207.56, -24) * mm, "radius": 2.54 * mm});
            skSolve(sketch);
        }
        {
            var Q0;
            Q0 = qSketchRegion(id + "F6", true);
            extrude(context, id + "F7", {"entities" : qUnion([Q0]), "operationType" : NewBodyOperationType.REMOVE, "endBound" : BoundingType.THROUGH_ALL, "oppositeDirection" : true, "depth" : 25.4 * mm, "offsetDistance" : 25.4 * mm});
        }
        {
            var Q0;
            Q0=makeQuery(id+"F1.opExtrude","SWEPT_FACE",FACE,{"disambiguationData":[OSD([sQuery(id+"F0.wireOp",EDGE,"E6.2"),sQuery(id+"F0.wireOp",EDGE,"E6.4")])]});
            var sketch = newSketch(context, id + "F8", { "sketchPlane" : qUnion([Q0])});
            skCircle(sketch, "E16", {"center": v(-27.98, 428.5) * mm, "radius": 2.54 * mm});
            skCircle(sketch, "E17.0.1.0", {"center": v(-27.97, 415.8) * mm, "radius": 2.54 * mm});
            skCircle(sketch, "E17.0.2.0", {"center": v(-27.95, 403.1) * mm, "radius": 2.54 * mm});
            skCircle(sketch, "E17.0.3.0", {"center": v(-27.94, 390.4) * mm, "radius": 2.54 * mm});
            skCircle(sketch, "E17.0.4.0", {"center": v(-27.92, 377.7) * mm, "radius": 2.54 * mm});
            skCircle(sketch, "E17.0.5.0", {"center": v(-27.9, 365) * mm, "radius": 2.54 * mm});
            skCircle(sketch, "E17.0.6.0", {"center": v(-27.9, 352.3) * mm, "radius": 2.54 * mm});
            skCircle(sketch, "E17.0.7.0", {"center": v(-27.88, 339.6) * mm, "radius": 2.54 * mm});
            skCircle(sketch, "E17.0.8.0", {"center": v(-27.86, 326.9) * mm, "radius": 2.54 * mm});
            skCircle(sketch, "E17.0.9.0", {"center": v(-27.85, 314.2) * mm, "radius": 2.54 * mm});
            skCircle(sketch, "E17.0.10.0", {"center": v(-27.83, 301.5) * mm, "radius": 2.54 * mm});
            skCircle(sketch, "E17.0.11.0", {"center": v(-27.82, 288.8) * mm, "radius": 2.54 * mm});
            skCircle(sketch, "E17.0.12.0", {"center": v(-27.8, 276.1) * mm, "radius": 2.54 * mm});
            skCircle(sketch, "E17.0.13.0", {"center": v(-27.79, 263.4) * mm, "radius": 2.54 * mm});
            skCircle(sketch, "E17.0.14.0", {"center": v(-27.77, 250.7) * mm, "radius": 2.54 * mm});
            skCircle(sketch, "E17.0.15.0", {"center": v(-27.76, 238) * mm, "radius": 2.54 * mm});
            skCircle(sketch, "E17.0.16.0", {"center": v(-27.74, 225.3) * mm, "radius": 2.54 * mm});
            skCircle(sketch, "E17.0.17.0", {"center": v(-27.73, 212.6) * mm, "radius": 2.54 * mm});
            skCircle(sketch, "E17.0.18.0", {"center": v(-27.71, 199.9) * mm, "radius": 2.54 * mm});
            skCircle(sketch, "E17.0.19.0", {"center": v(-27.7, 187.2) * mm, "radius": 2.54 * mm});
            skCircle(sketch, "E17.0.20.0", {"center": v(-27.68, 174.5) * mm, "radius": 2.54 * mm});
            skCircle(sketch, "E17.0.21.0", {"center": v(-27.66, 161.8) * mm, "radius": 2.54 * mm});
            skCircle(sketch, "E17.0.22.0", {"center": v(-27.65, 149.1) * mm, "radius": 2.54 * mm});
            skCircle(sketch, "E17.0.23.0", {"center": v(-27.63, 136.4) * mm, "radius": 2.54 * mm});
            skCircle(sketch, "E17.0.24.0", {"center": v(-27.62, 123.7) * mm, "radius": 2.54 * mm});
            skCircle(sketch, "E17.0.25.0", {"center": v(-27.6, 111) * mm, "radius": 2.54 * mm});
            skCircle(sketch, "E17.0.26.0", {"center": v(-27.59, 98.3) * mm, "radius": 2.54 * mm});
            skCircle(sketch, "E17.0.27.0", {"center": v(-27.57, 85.6) * mm, "radius": 2.54 * mm});
            skCircle(sketch, "E17.0.28.0", {"center": v(-27.56, 72.9) * mm, "radius": 2.54 * mm});
            skCircle(sketch, "E17.0.29.0", {"center": v(-27.54, 60.2) * mm, "radius": 2.54 * mm});
            skCircle(sketch, "E17.0.30.0", {"center": v(-27.53, 47.5) * mm, "radius": 2.54 * mm});
            skCircle(sketch, "E17.0.31.0", {"center": v(-27.51, 34.8) * mm, "radius": 2.54 * mm});
            skCircle(sketch, "E17.0.32.0", {"center": v(-27.5, 22.1) * mm, "radius": 2.54 * mm});
            skCircle(sketch, "E17.0.33.0", {"center": v(-27.48, 9.4) * mm, "radius": 2.54 * mm});
            skCircle(sketch, "E17.1.0.0", {"center": v(-15.28, 428.5) * mm, "radius": 2.54 * mm});
            skCircle(sketch, "E17.1.1.0", {"center": v(-15.27, 415.8) * mm, "radius": 2.54 * mm});
            skCircle(sketch, "E17.1.2.0", {"center": v(-15.25, 403.1) * mm, "radius": 2.54 * mm});
            skCircle(sketch, "E17.1.3.0", {"center": v(-15.24, 390.4) * mm, "radius": 2.54 * mm});
            skCircle(sketch, "E17.1.4.0", {"center": v(-15.22, 377.7) * mm, "radius": 2.54 * mm});
            skCircle(sketch, "E17.1.5.0", {"center": v(-15.2, 365) * mm, "radius": 2.54 * mm});
            skCircle(sketch, "E17.1.6.0", {"center": v(-15.2, 352.3) * mm, "radius": 2.54 * mm});
            skCircle(sketch, "E17.1.7.0", {"center": v(-15.18, 339.6) * mm, "radius": 2.54 * mm});
            skCircle(sketch, "E17.1.8.0", {"center": v(-15.16, 326.9) * mm, "radius": 2.54 * mm});
            skCircle(sketch, "E17.1.9.0", {"center": v(-15.15, 314.2) * mm, "radius": 2.54 * mm});
            skCircle(sketch, "E17.1.10.0", {"center": v(-15.13, 301.5) * mm, "radius": 2.54 * mm});
            skCircle(sketch, "E17.1.11.0", {"center": v(-15.12, 288.8) * mm, "radius": 2.54 * mm});
            skCircle(sketch, "E17.1.12.0", {"center": v(-15.1, 276.1) * mm, "radius": 2.54 * mm});
            skCircle(sketch, "E17.1.13.0", {"center": v(-15.09, 263.4) * mm, "radius": 2.54 * mm});
            skCircle(sketch, "E17.1.14.0", {"center": v(-15.07, 250.7) * mm, "radius": 2.54 * mm});
            skCircle(sketch, "E17.1.15.0", {"center": v(-15.06, 238) * mm, "radius": 2.54 * mm});
            skCircle(sketch, "E17.1.16.0", {"center": v(-15.04, 225.3) * mm, "radius": 2.54 * mm});
            skCircle(sketch, "E17.1.17.0", {"center": v(-15.03, 212.6) * mm, "radius": 2.54 * mm});
            skCircle(sketch, "E17.1.18.0", {"center": v(-15.01, 199.9) * mm, "radius": 2.54 * mm});
            skCircle(sketch, "E17.1.19.0", {"center": v(-15, 187.2) * mm, "radius": 2.54 * mm});
            skCircle(sketch, "E17.1.20.0", {"center": v(-14.98, 174.5) * mm, "radius": 2.54 * mm});
            skCircle(sketch, "E17.1.21.0", {"center": v(-14.96, 161.8) * mm, "radius": 2.54 * mm});
            skCircle(sketch, "E17.1.22.0", {"center": v(-14.95, 149.1) * mm, "radius": 2.54 * mm});
            skCircle(sketch, "E17.1.23.0", {"center": v(-14.93, 136.4) * mm, "radius": 2.54 * mm});
            skCircle(sketch, "E17.1.24.0", {"center": v(-14.92, 123.7) * mm, "radius": 2.54 * mm});
            skCircle(sketch, "E17.1.25.0", {"center": v(-14.9, 111) * mm, "radius": 2.54 * mm});
            skCircle(sketch, "E17.1.26.0", {"center": v(-14.89, 98.3) * mm, "radius": 2.54 * mm});
            skCircle(sketch, "E17.1.27.0", {"center": v(-14.87, 85.6) * mm, "radius": 2.54 * mm});
            skCircle(sketch, "E17.1.28.0", {"center": v(-14.86, 72.9) * mm, "radius": 2.54 * mm});
            skCircle(sketch, "E17.1.29.0", {"center": v(-14.84, 60.2) * mm, "radius": 2.54 * mm});
            skCircle(sketch, "E17.1.30.0", {"center": v(-14.83, 47.5) * mm, "radius": 2.54 * mm});
            skCircle(sketch, "E17.1.31.0", {"center": v(-14.81, 34.8) * mm, "radius": 2.54 * mm});
            skCircle(sketch, "E17.1.32.0", {"center": v(-14.8, 22.1) * mm, "radius": 2.54 * mm});
            skCircle(sketch, "E17.1.33.0", {"center": v(-14.78, 9.4) * mm, "radius": 2.54 * mm});
            skCircle(sketch, "E17.2.0.0", {"center": v(-2.58, 428.5) * mm, "radius": 2.54 * mm});
            skCircle(sketch, "E17.2.1.0", {"center": v(-2.57, 415.8) * mm, "radius": 2.54 * mm});
            skCircle(sketch, "E17.2.2.0", {"center": v(-2.55, 403.1) * mm, "radius": 2.54 * mm});
            skCircle(sketch, "E17.2.3.0", {"center": v(-2.54, 390.4) * mm, "radius": 2.54 * mm});
            skCircle(sketch, "E17.2.4.0", {"center": v(-2.52, 377.7) * mm, "radius": 2.54 * mm});
            skCircle(sketch, "E17.2.5.0", {"center": v(-2.5, 365) * mm, "radius": 2.54 * mm});
            skCircle(sketch, "E17.2.6.0", {"center": v(-2.5, 352.3) * mm, "radius": 2.54 * mm});
            skCircle(sketch, "E17.2.7.0", {"center": v(-2.48, 339.6) * mm, "radius": 2.54 * mm});
            skCircle(sketch, "E17.2.8.0", {"center": v(-2.46, 326.9) * mm, "radius": 2.54 * mm});
            skCircle(sketch, "E17.2.9.0", {"center": v(-2.45, 314.2) * mm, "radius": 2.54 * mm});
            skCircle(sketch, "E17.2.10.0", {"center": v(-2.43, 301.5) * mm, "radius": 2.54 * mm});
            skCircle(sketch, "E17.2.11.0", {"center": v(-2.42, 288.8) * mm, "radius": 2.54 * mm});
            skCircle(sketch, "E17.2.12.0", {"center": v(-2.4, 276.1) * mm, "radius": 2.54 * mm});
            skCircle(sketch, "E17.2.13.0", {"center": v(-2.39, 263.4) * mm, "radius": 2.54 * mm});
            skCircle(sketch, "E17.2.14.0", {"center": v(-2.37, 250.7) * mm, "radius": 2.54 * mm});
            skCircle(sketch, "E17.2.15.0", {"center": v(-2.36, 238) * mm, "radius": 2.54 * mm});
            skCircle(sketch, "E17.2.16.0", {"center": v(-2.34, 225.3) * mm, "radius": 2.54 * mm});
            skCircle(sketch, "E17.2.17.0", {"center": v(-2.33, 212.6) * mm, "radius": 2.54 * mm});
            skCircle(sketch, "E17.2.18.0", {"center": v(-2.31, 199.9) * mm, "radius": 2.54 * mm});
            skCircle(sketch, "E17.2.19.0", {"center": v(-2.3, 187.2) * mm, "radius": 2.54 * mm});
            skCircle(sketch, "E17.2.20.0", {"center": v(-2.28, 174.5) * mm, "radius": 2.54 * mm});
            skCircle(sketch, "E17.2.21.0", {"center": v(-2.26, 161.8) * mm, "radius": 2.54 * mm});
            skCircle(sketch, "E17.2.22.0", {"center": v(-2.25, 149.1) * mm, "radius": 2.54 * mm});
            skCircle(sketch, "E17.2.23.0", {"center": v(-2.23, 136.4) * mm, "radius": 2.54 * mm});
            skCircle(sketch, "E17.2.24.0", {"center": v(-2.22, 123.7) * mm, "radius": 2.54 * mm});
            skCircle(sketch, "E17.2.25.0", {"center": v(-2.2, 111) * mm, "radius": 2.54 * mm});
            skCircle(sketch, "E17.2.26.0", {"center": v(-2.19, 98.3) * mm, "radius": 2.54 * mm});
            skCircle(sketch, "E17.2.27.0", {"center": v(-2.17, 85.6) * mm, "radius": 2.54 * mm});
            skCircle(sketch, "E17.2.28.0", {"center": v(-2.16, 72.9) * mm, "radius": 2.54 * mm});
            skCircle(sketch, "E17.2.29.0", {"center": v(-2.14, 60.2) * mm, "radius": 2.54 * mm});
            skCircle(sketch, "E17.2.30.0", {"center": v(-2.13, 47.5) * mm, "radius": 2.54 * mm});
            skCircle(sketch, "E17.2.31.0", {"center": v(-2.11, 34.8) * mm, "radius": 2.54 * mm});
            skCircle(sketch, "E17.2.32.0", {"center": v(-2.1, 22.1) * mm, "radius": 2.54 * mm});
            skCircle(sketch, "E17.2.33.0", {"center": v(-2.08, 9.4) * mm, "radius": 2.54 * mm});
            skCircle(sketch, "E17.3.0.0", {"center": v(10.12, 428.5) * mm, "radius": 2.54 * mm});
            skCircle(sketch, "E17.3.1.0", {"center": v(10.13, 415.8) * mm, "radius": 2.54 * mm});
            skCircle(sketch, "E17.3.2.0", {"center": v(10.15, 403.1) * mm, "radius": 2.54 * mm});
            skCircle(sketch, "E17.3.3.0", {"center": v(10.16, 390.4) * mm, "radius": 2.54 * mm});
            skCircle(sketch, "E17.3.4.0", {"center": v(10.18, 377.7) * mm, "radius": 2.54 * mm});
            skCircle(sketch, "E17.3.5.0", {"center": v(10.2, 365) * mm, "radius": 2.54 * mm});
            skCircle(sketch, "E17.3.6.0", {"center": v(10.2, 352.3) * mm, "radius": 2.54 * mm});
            skCircle(sketch, "E17.3.7.0", {"center": v(10.22, 339.6) * mm, "radius": 2.54 * mm});
            skCircle(sketch, "E17.3.8.0", {"center": v(10.24, 326.9) * mm, "radius": 2.54 * mm});
            skCircle(sketch, "E17.3.9.0", {"center": v(10.25, 314.2) * mm, "radius": 2.54 * mm});
            skCircle(sketch, "E17.3.10.0", {"center": v(10.27, 301.5) * mm, "radius": 2.54 * mm});
            skCircle(sketch, "E17.3.11.0", {"center": v(10.28, 288.8) * mm, "radius": 2.54 * mm});
            skCircle(sketch, "E17.3.12.0", {"center": v(10.3, 276.1) * mm, "radius": 2.54 * mm});
            skCircle(sketch, "E17.3.13.0", {"center": v(10.31, 263.4) * mm, "radius": 2.54 * mm});
            skCircle(sketch, "E17.3.14.0", {"center": v(10.33, 250.7) * mm, "radius": 2.54 * mm});
            skCircle(sketch, "E17.3.15.0", {"center": v(10.34, 238) * mm, "radius": 2.54 * mm});
            skCircle(sketch, "E17.3.16.0", {"center": v(10.36, 225.3) * mm, "radius": 2.54 * mm});
            skCircle(sketch, "E17.3.17.0", {"center": v(10.37, 212.6) * mm, "radius": 2.54 * mm});
            skCircle(sketch, "E17.3.18.0", {"center": v(10.39, 199.9) * mm, "radius": 2.54 * mm});
            skCircle(sketch, "E17.3.19.0", {"center": v(10.4, 187.2) * mm, "radius": 2.54 * mm});
            skCircle(sketch, "E17.3.20.0", {"center": v(10.42, 174.5) * mm, "radius": 2.54 * mm});
            skCircle(sketch, "E17.3.21.0", {"center": v(10.44, 161.8) * mm, "radius": 2.54 * mm});
            skCircle(sketch, "E17.3.22.0", {"center": v(10.45, 149.1) * mm, "radius": 2.54 * mm});
            skCircle(sketch, "E17.3.23.0", {"center": v(10.47, 136.4) * mm, "radius": 2.54 * mm});
            skCircle(sketch, "E17.3.24.0", {"center": v(10.48, 123.7) * mm, "radius": 2.54 * mm});
            skCircle(sketch, "E17.3.25.0", {"center": v(10.5, 111) * mm, "radius": 2.54 * mm});
            skCircle(sketch, "E17.3.26.0", {"center": v(10.51, 98.3) * mm, "radius": 2.54 * mm});
            skCircle(sketch, "E17.3.27.0", {"center": v(10.53, 85.6) * mm, "radius": 2.54 * mm});
            skCircle(sketch, "E17.3.28.0", {"center": v(10.54, 72.9) * mm, "radius": 2.54 * mm});
            skCircle(sketch, "E17.3.29.0", {"center": v(10.56, 60.2) * mm, "radius": 2.54 * mm});
            skCircle(sketch, "E17.3.30.0", {"center": v(10.57, 47.5) * mm, "radius": 2.54 * mm});
            skCircle(sketch, "E17.3.31.0", {"center": v(10.59, 34.8) * mm, "radius": 2.54 * mm});
            skCircle(sketch, "E17.3.32.0", {"center": v(10.6, 22.1) * mm, "radius": 2.54 * mm});
            skCircle(sketch, "E17.3.33.0", {"center": v(10.62, 9.4) * mm, "radius": 2.54 * mm});
            skCircle(sketch, "E17.4.0.0", {"center": v(22.82, 428.5) * mm, "radius": 2.54 * mm});
            skCircle(sketch, "E17.4.1.0", {"center": v(22.83, 415.8) * mm, "radius": 2.54 * mm});
            skCircle(sketch, "E17.4.2.0", {"center": v(22.85, 403.1) * mm, "radius": 2.54 * mm});
            skCircle(sketch, "E17.4.3.0", {"center": v(22.86, 390.4) * mm, "radius": 2.54 * mm});
            skCircle(sketch, "E17.4.4.0", {"center": v(22.88, 377.7) * mm, "radius": 2.54 * mm});
            skCircle(sketch, "E17.4.5.0", {"center": v(22.9, 365) * mm, "radius": 2.54 * mm});
            skCircle(sketch, "E17.4.6.0", {"center": v(22.9, 352.3) * mm, "radius": 2.54 * mm});
            skCircle(sketch, "E17.4.7.0", {"center": v(22.92, 339.6) * mm, "radius": 2.54 * mm});
            skCircle(sketch, "E17.4.8.0", {"center": v(22.94, 326.9) * mm, "radius": 2.54 * mm});
            skCircle(sketch, "E17.4.9.0", {"center": v(22.95, 314.2) * mm, "radius": 2.54 * mm});
            skCircle(sketch, "E17.4.10.0", {"center": v(22.97, 301.5) * mm, "radius": 2.54 * mm});
            skCircle(sketch, "E17.4.11.0", {"center": v(22.98, 288.8) * mm, "radius": 2.54 * mm});
            skCircle(sketch, "E17.4.12.0", {"center": v(23, 276.1) * mm, "radius": 2.54 * mm});
            skCircle(sketch, "E17.4.13.0", {"center": v(23.01, 263.4) * mm, "radius": 2.54 * mm});
            skCircle(sketch, "E17.4.14.0", {"center": v(23.03, 250.7) * mm, "radius": 2.54 * mm});
            skCircle(sketch, "E17.4.15.0", {"center": v(23.04, 238) * mm, "radius": 2.54 * mm});
            skCircle(sketch, "E17.4.16.0", {"center": v(23.06, 225.3) * mm, "radius": 2.54 * mm});
            skCircle(sketch, "E17.4.17.0", {"center": v(23.07, 212.6) * mm, "radius": 2.54 * mm});
            skCircle(sketch, "E17.4.18.0", {"center": v(23.09, 199.9) * mm, "radius": 2.54 * mm});
            skCircle(sketch, "E17.4.19.0", {"center": v(23.1, 187.2) * mm, "radius": 2.54 * mm});
            skCircle(sketch, "E17.4.20.0", {"center": v(23.12, 174.5) * mm, "radius": 2.54 * mm});
            skCircle(sketch, "E17.4.21.0", {"center": v(23.14, 161.8) * mm, "radius": 2.54 * mm});
            skCircle(sketch, "E17.4.22.0", {"center": v(23.15, 149.1) * mm, "radius": 2.54 * mm});
            skCircle(sketch, "E17.4.23.0", {"center": v(23.17, 136.4) * mm, "radius": 2.54 * mm});
            skCircle(sketch, "E17.4.24.0", {"center": v(23.18, 123.7) * mm, "radius": 2.54 * mm});
            skCircle(sketch, "E17.4.25.0", {"center": v(23.2, 111) * mm, "radius": 2.54 * mm});
            skCircle(sketch, "E17.4.26.0", {"center": v(23.21, 98.3) * mm, "radius": 2.54 * mm});
            skCircle(sketch, "E17.4.27.0", {"center": v(23.23, 85.6) * mm, "radius": 2.54 * mm});
            skCircle(sketch, "E17.4.28.0", {"center": v(23.24, 72.9) * mm, "radius": 2.54 * mm});
            skCircle(sketch, "E17.4.29.0", {"center": v(23.26, 60.2) * mm, "radius": 2.54 * mm});
            skCircle(sketch, "E17.4.30.0", {"center": v(23.27, 47.5) * mm, "radius": 2.54 * mm});
            skCircle(sketch, "E17.4.31.0", {"center": v(23.29, 34.8) * mm, "radius": 2.54 * mm});
            skCircle(sketch, "E17.4.32.0", {"center": v(23.3, 22.1) * mm, "radius": 2.54 * mm});
            skCircle(sketch, "E17.4.33.0", {"center": v(23.32, 9.4) * mm, "radius": 2.54 * mm});
            skLineSegment(sketch, "E17.direction1", {"start": v(-27.98, 428.5) * mm, "end": v(-15.28, 428.5) * mm, "construction": true});
            skLineSegment(sketch, "E17.direction2", {"start": v(-27.98, 428.5) * mm, "end": v(-27.97, 415.8) * mm, "construction": true});
            skSolve(sketch);
        }
        {
            var Q0;
            Q0 = qSketchRegion(id + "F8", true);
            extrude(context, id + "F9", {"entities" : qUnion([Q0]), "operationType" : NewBodyOperationType.REMOVE, "oppositeDirection" : true, "depth" : 25.4 * mm, "offsetDistance" : 25.4 * mm});
        }
        {
            var Q0;
            {var subQ0=sQuery(id+"F0.wireOp",EDGE,"E1");var subQ1=sQuery(id+"F0.wireOp",EDGE,"E0");var subQ2=sQuery(id+"F0.wireOp",EDGE,"E6.3");var subQ3=sQuery(id+"F0.wireOp",EDGE,"E6.1");Q0=makeQuery(id+"F3.boolean.opBoolean","SPLIT",FACE,{"disambiguationData":[TD([makeQuery(id+"F1.opExtrude","SWEPT_FACE",FACE,{"disambiguationData":[OSD([subQ1,subQ0])]}),makeQuery(id+"F1.opExtrude","SWEPT_FACE",FACE,{"disambiguationData":[OSD([subQ3,subQ2])]}),makeQuery(id+"F3.opExtrude","SWEPT_FACE",FACE,{"disambiguationData":[OSD([sQuery(id+"F2.wireOp",EDGE,"E8.13.0.0")])]}),makeQuery(id+"F3.opExtrude","SWEPT_FACE",FACE,{"disambiguationData":[OSD([sQuery(id+"F2.wireOp",EDGE,"E8.14.0.0")])]})])],"derivedFrom":makeQuery(id+"F1.opExtrude","CAP_FACE",FACE,{"disambiguationData":[OSD([subQ1,subQ0,sQuery(id+"F0.wireOp",EDGE,"E2"),sQuery(id+"F0.wireOp",EDGE,"E3"),sQuery(id+"F0.wireOp",EDGE,"E4"),sQuery(id+"F0.wireOp",EDGE,"E5"),sQuery(id+"F0.wireOp",EDGE,"E6.0"),subQ3,sQuery(id+"F0.wireOp",EDGE,"E6.2"),subQ2,sQuery(id+"F0.wireOp",EDGE,"E6.4"),sQuery(id+"F0.wireOp",EDGE,"E6.5")])],"isStart":false})});}
            var sketch = newSketch(context, id + "F10", { "sketchPlane" : qUnion([Q0])});
            skLineSegment(sketch, "E18.bottom", {"start": v(215.9, -31.75) * mm, "end": v(-215.9, -31.75) * mm});
            skLineSegment(sketch, "E18.top", {"start": v(215.9, 31.75) * mm, "end": v(-215.9, 31.75) * mm});
            skLineSegment(sketch, "E18.left", {"start": v(215.9, -31.75) * mm, "end": v(215.9, 31.75) * mm});
            skLineSegment(sketch, "E18.right", {"start": v(-215.9, -31.75) * mm, "end": v(-215.9, 31.75) * mm});
            skLineSegment(sketch, "E19.bottom", {"start": v(-190.5, 6.35) * mm, "end": v(190.5, 6.35) * mm});
            skLineSegment(sketch, "E19.top", {"start": v(-190.5, -6.35) * mm, "end": v(190.5, -6.35) * mm});
            skLineSegment(sketch, "E19.left", {"start": v(-190.5, 6.35) * mm, "end": v(-190.5, -6.35) * mm});
            skLineSegment(sketch, "E19.right", {"start": v(190.5, 6.35) * mm, "end": v(190.5, -6.35) * mm});
            skSolve(sketch);
        }
        {
            var Q0;
            Q0 = qSketchRegion(id + "F10", true);
            extrude(context, id + "F11", {"entities" : qUnion([Q0]), "operationType" : NewBodyOperationType.ADD, "depth" : 2.54 * mm, "offsetDistance" : 25.4 * mm});
        }
    });
